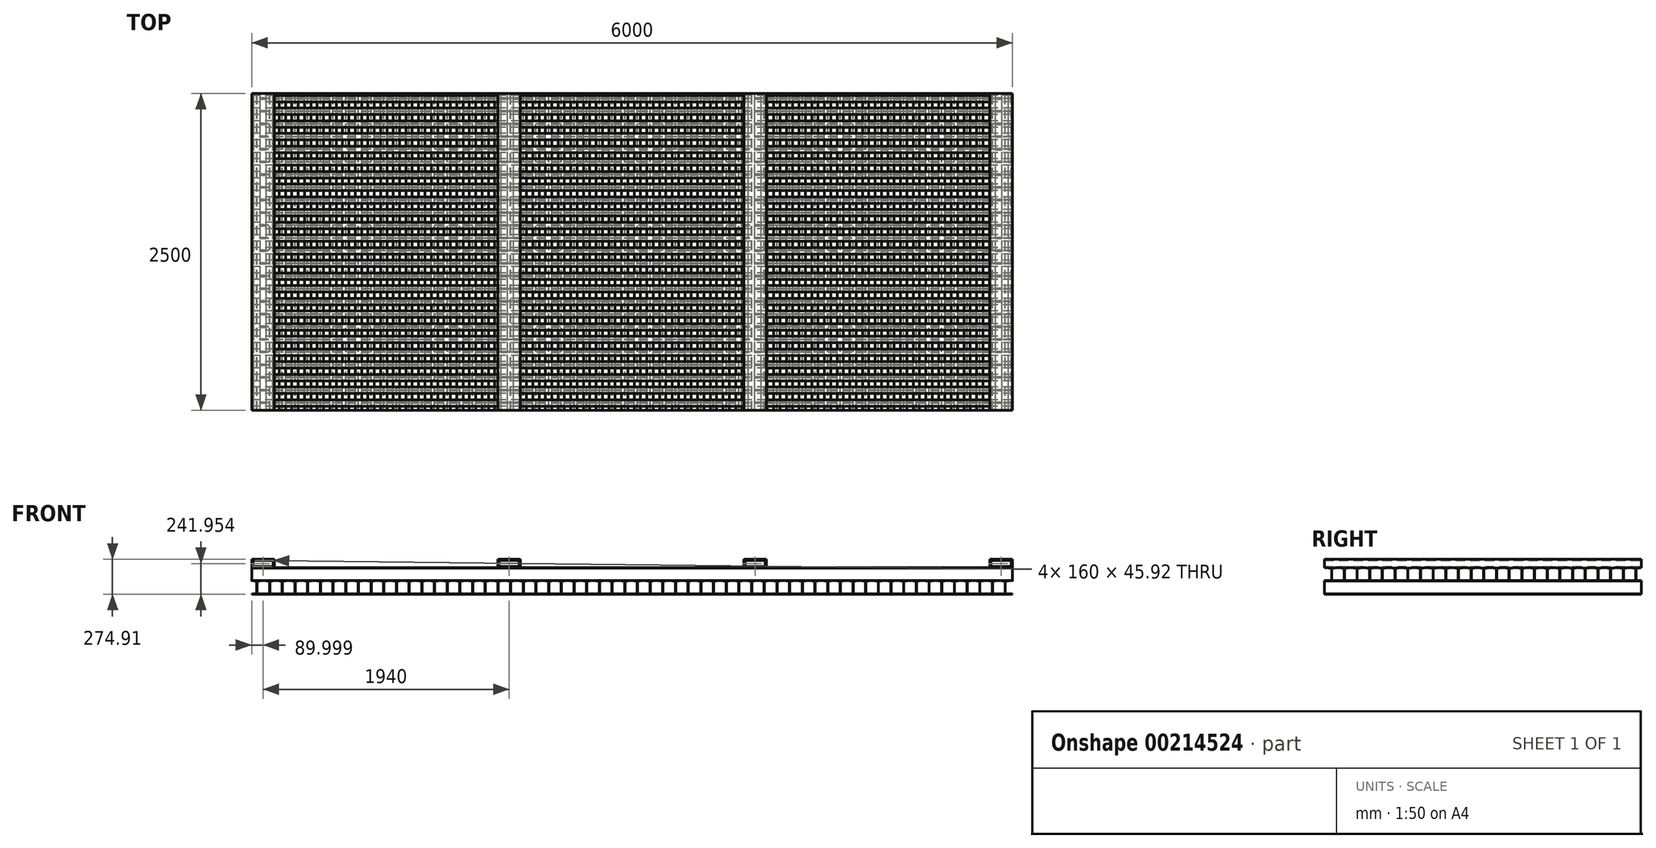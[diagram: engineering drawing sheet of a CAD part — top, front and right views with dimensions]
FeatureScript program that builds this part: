
annotation { "Feature Type Name" : "Feature", "Feature Type Description" : "" }
export const myFeature = defineFeature(function(context is Context, id is Id, definition is map)
    precondition{}
    {
        {
            var Q0;
            Q0=qCreatedBy(makeId("Front.planeOp"),FACE);
            var sketch = newSketch(context, id + "F0", { "sketchPlane" : qUnion([Q0])});
            skLineSegment(sketch, "E0.bottom", {"start": v(-13.61, -0.15) * mm, "end": v(5939.39, -0.15) * mm});
            skLineSegment(sketch, "E0.top", {"start": v(-60.61, -3.15) * mm, "end": v(5939.39, -3.15) * mm});
            skLineSegment(sketch, "E0.left", {"start": v(-60.61, -0.15) * mm, "end": v(-60.61, -3.15) * mm});
            skLineSegment(sketch, "E0.right", {"start": v(5939.39, -0.15) * mm, "end": v(5939.39, -3.15) * mm});
            skLineSegment(sketch, "E1.bottom", {"start": v(-44.11, 99.85) * mm, "end": v(-24.61, 99.85) * mm});
            skLineSegment(sketch, "E1.top", {"start": v(-60.61, -0.15) * mm, "end": v(-24.61, -0.15) * mm});
            skLineSegment(sketch, "E1.left", {"start": v(-20.61, 95.85) * mm, "end": v(-20.61, 3.85) * mm});
            skLineSegment(sketch, "E1.right", {"start": v(-17.61, 95.85) * mm, "end": v(-17.61, 3.85) * mm});
            skLineSegment(sketch, "E2.bottom", {"start": v(-13.61, 99.85) * mm, "end": v(5.89, 99.85) * mm});
            skLineSegment(sketch, "E2.top", {"start": v(-44.11, 102.85) * mm, "end": v(5.89, 102.85) * mm});
            skLineSegment(sketch, "E2.left", {"start": v(-44.11, 99.85) * mm, "end": v(-44.11, 102.85) * mm});
            skLineSegment(sketch, "E2.right", {"start": v(5.89, 99.85) * mm, "end": v(5.89, 102.85) * mm});
            skPoint(sketch, "E3.newPointB", {"position": v(-17.61, 96.07) * mm});
            skArc(sketch, "E3.filletArc", {"start": v(-13.61, 99.85) * mm, "mid": v(-16.44, 98.67) * mm, "end": v(-17.61, 95.85) * mm});
            skPoint(sketch, "E4.visualSharp", {"position": v(-20.61, 99.85) * mm});
            skArc(sketch, "E4.filletArc", {"start": v(-20.61, 95.85) * mm, "mid": v(-21.78, 98.67) * mm, "end": v(-24.61, 99.85) * mm});
            skArc(sketch, "E5.filletArc", {"start": v(-17.61, 3.85) * mm, "mid": v(-16.44, 1.02) * mm, "end": v(-13.61, -0.15) * mm});
            skPoint(sketch, "E6.visualSharp", {"position": v(-20.61, -0.15) * mm});
            skArc(sketch, "E6.filletArc", {"start": v(-24.61, -0.15) * mm, "mid": v(-21.78, 1.02) * mm, "end": v(-20.61, 3.85) * mm});
            skPoint(sketch, "E7.1.0.0", {"position": v(79.39, 99.85) * mm});
            skLineSegment(sketch, "E7.1.0.1", {"start": v(55.89, 99.85) * mm, "end": v(75.39, 99.85) * mm});
            skPoint(sketch, "E7.1.0.2", {"position": v(82.39, 96.07) * mm});
            skLineSegment(sketch, "E7.1.0.3", {"start": v(79.39, 95.85) * mm, "end": v(79.39, 3.85) * mm});
            skLineSegment(sketch, "E7.1.0.4", {"start": v(82.39, 95.85) * mm, "end": v(82.39, 3.85) * mm});
            skLineSegment(sketch, "E7.1.0.5", {"start": v(55.89, 102.85) * mm, "end": v(105.89, 102.85) * mm});
            skLineSegment(sketch, "E7.1.0.6", {"start": v(86.39, 99.85) * mm, "end": v(105.89, 99.85) * mm});
            skLineSegment(sketch, "E7.1.0.7", {"start": v(105.89, 99.85) * mm, "end": v(105.89, 102.85) * mm});
            skLineSegment(sketch, "E7.1.0.8", {"start": v(55.89, 99.85) * mm, "end": v(55.89, 102.85) * mm});
            skArc(sketch, "E7.1.0.9", {"start": v(86.39, 99.85) * mm, "mid": v(83.56, 98.67) * mm, "end": v(82.39, 95.85) * mm});
            skArc(sketch, "E7.1.0.10", {"start": v(79.39, 95.85) * mm, "mid": v(78.22, 98.67) * mm, "end": v(75.39, 99.85) * mm});
            skArc(sketch, "E7.1.0.11", {"start": v(75.39, -0.15) * mm, "mid": v(78.22, 1.02) * mm, "end": v(79.39, 3.85) * mm});
            skArc(sketch, "E7.1.0.12", {"start": v(82.39, 3.85) * mm, "mid": v(83.56, 1.02) * mm, "end": v(86.39, -0.15) * mm});
            skPoint(sketch, "E7.2.0.0", {"position": v(179.39, 99.85) * mm});
            skLineSegment(sketch, "E7.2.0.1", {"start": v(155.89, 99.85) * mm, "end": v(175.39, 99.85) * mm});
            skPoint(sketch, "E7.2.0.2", {"position": v(182.39, 96.07) * mm});
            skLineSegment(sketch, "E7.2.0.3", {"start": v(179.39, 95.85) * mm, "end": v(179.39, 3.85) * mm});
            skLineSegment(sketch, "E7.2.0.4", {"start": v(182.39, 95.85) * mm, "end": v(182.39, 3.85) * mm});
            skLineSegment(sketch, "E7.2.0.5", {"start": v(155.89, 102.85) * mm, "end": v(205.89, 102.85) * mm});
            skLineSegment(sketch, "E7.2.0.6", {"start": v(186.39, 99.85) * mm, "end": v(205.89, 99.85) * mm});
            skLineSegment(sketch, "E7.2.0.7", {"start": v(205.89, 99.85) * mm, "end": v(205.89, 102.85) * mm});
            skLineSegment(sketch, "E7.2.0.8", {"start": v(155.89, 99.85) * mm, "end": v(155.89, 102.85) * mm});
            skArc(sketch, "E7.2.0.9", {"start": v(186.39, 99.85) * mm, "mid": v(183.56, 98.67) * mm, "end": v(182.39, 95.85) * mm});
            skArc(sketch, "E7.2.0.10", {"start": v(179.39, 95.85) * mm, "mid": v(178.22, 98.67) * mm, "end": v(175.39, 99.85) * mm});
            skArc(sketch, "E7.2.0.11", {"start": v(175.39, -0.15) * mm, "mid": v(178.22, 1.02) * mm, "end": v(179.39, 3.85) * mm});
            skArc(sketch, "E7.2.0.12", {"start": v(182.39, 3.85) * mm, "mid": v(183.56, 1.02) * mm, "end": v(186.39, -0.15) * mm});
            skPoint(sketch, "E7.3.0.0", {"position": v(279.39, 99.85) * mm});
            skLineSegment(sketch, "E7.3.0.1", {"start": v(255.89, 99.85) * mm, "end": v(275.39, 99.85) * mm});
            skPoint(sketch, "E7.3.0.2", {"position": v(282.39, 96.07) * mm});
            skLineSegment(sketch, "E7.3.0.3", {"start": v(279.39, 95.85) * mm, "end": v(279.39, 3.85) * mm});
            skLineSegment(sketch, "E7.3.0.4", {"start": v(282.39, 95.85) * mm, "end": v(282.39, 3.85) * mm});
            skLineSegment(sketch, "E7.3.0.5", {"start": v(255.89, 102.85) * mm, "end": v(305.89, 102.85) * mm});
            skLineSegment(sketch, "E7.3.0.6", {"start": v(286.39, 99.85) * mm, "end": v(305.89, 99.85) * mm});
            skLineSegment(sketch, "E7.3.0.7", {"start": v(305.89, 99.85) * mm, "end": v(305.89, 102.85) * mm});
            skLineSegment(sketch, "E7.3.0.8", {"start": v(255.89, 99.85) * mm, "end": v(255.89, 102.85) * mm});
            skArc(sketch, "E7.3.0.9", {"start": v(286.39, 99.85) * mm, "mid": v(283.56, 98.67) * mm, "end": v(282.39, 95.85) * mm});
            skArc(sketch, "E7.3.0.10", {"start": v(279.39, 95.85) * mm, "mid": v(278.22, 98.67) * mm, "end": v(275.39, 99.85) * mm});
            skArc(sketch, "E7.3.0.11", {"start": v(275.39, -0.15) * mm, "mid": v(278.22, 1.02) * mm, "end": v(279.39, 3.85) * mm});
            skArc(sketch, "E7.3.0.12", {"start": v(282.39, 3.85) * mm, "mid": v(283.56, 1.02) * mm, "end": v(286.39, -0.15) * mm});
            skPoint(sketch, "E7.4.0.0", {"position": v(379.39, 99.85) * mm});
            skLineSegment(sketch, "E7.4.0.1", {"start": v(355.89, 99.85) * mm, "end": v(375.39, 99.85) * mm});
            skPoint(sketch, "E7.4.0.2", {"position": v(382.39, 96.07) * mm});
            skLineSegment(sketch, "E7.4.0.3", {"start": v(379.39, 95.85) * mm, "end": v(379.39, 3.85) * mm});
            skLineSegment(sketch, "E7.4.0.4", {"start": v(382.39, 95.85) * mm, "end": v(382.39, 3.85) * mm});
            skLineSegment(sketch, "E7.4.0.5", {"start": v(355.89, 102.85) * mm, "end": v(405.89, 102.85) * mm});
            skLineSegment(sketch, "E7.4.0.6", {"start": v(386.39, 99.85) * mm, "end": v(405.89, 99.85) * mm});
            skLineSegment(sketch, "E7.4.0.7", {"start": v(405.89, 99.85) * mm, "end": v(405.89, 102.85) * mm});
            skLineSegment(sketch, "E7.4.0.8", {"start": v(355.89, 99.85) * mm, "end": v(355.89, 102.85) * mm});
            skArc(sketch, "E7.4.0.9", {"start": v(386.39, 99.85) * mm, "mid": v(383.56, 98.67) * mm, "end": v(382.39, 95.85) * mm});
            skArc(sketch, "E7.4.0.10", {"start": v(379.39, 95.85) * mm, "mid": v(378.22, 98.67) * mm, "end": v(375.39, 99.85) * mm});
            skArc(sketch, "E7.4.0.11", {"start": v(375.39, -0.15) * mm, "mid": v(378.22, 1.02) * mm, "end": v(379.39, 3.85) * mm});
            skArc(sketch, "E7.4.0.12", {"start": v(382.39, 3.85) * mm, "mid": v(383.56, 1.02) * mm, "end": v(386.39, -0.15) * mm});
            skPoint(sketch, "E7.5.0.0", {"position": v(479.39, 99.85) * mm});
            skLineSegment(sketch, "E7.5.0.1", {"start": v(455.89, 99.85) * mm, "end": v(475.39, 99.85) * mm});
            skPoint(sketch, "E7.5.0.2", {"position": v(482.39, 96.07) * mm});
            skLineSegment(sketch, "E7.5.0.3", {"start": v(479.39, 95.85) * mm, "end": v(479.39, 3.85) * mm});
            skLineSegment(sketch, "E7.5.0.4", {"start": v(482.39, 95.85) * mm, "end": v(482.39, 3.85) * mm});
            skLineSegment(sketch, "E7.5.0.5", {"start": v(455.89, 102.85) * mm, "end": v(505.89, 102.85) * mm});
            skLineSegment(sketch, "E7.5.0.6", {"start": v(486.39, 99.85) * mm, "end": v(505.89, 99.85) * mm});
            skLineSegment(sketch, "E7.5.0.7", {"start": v(505.89, 99.85) * mm, "end": v(505.89, 102.85) * mm});
            skLineSegment(sketch, "E7.5.0.8", {"start": v(455.89, 99.85) * mm, "end": v(455.89, 102.85) * mm});
            skArc(sketch, "E7.5.0.9", {"start": v(486.39, 99.85) * mm, "mid": v(483.56, 98.67) * mm, "end": v(482.39, 95.85) * mm});
            skArc(sketch, "E7.5.0.10", {"start": v(479.39, 95.85) * mm, "mid": v(478.22, 98.67) * mm, "end": v(475.39, 99.85) * mm});
            skArc(sketch, "E7.5.0.11", {"start": v(475.39, -0.15) * mm, "mid": v(478.22, 1.02) * mm, "end": v(479.39, 3.85) * mm});
            skArc(sketch, "E7.5.0.12", {"start": v(482.39, 3.85) * mm, "mid": v(483.56, 1.02) * mm, "end": v(486.39, -0.15) * mm});
            skPoint(sketch, "E7.6.0.0", {"position": v(579.39, 99.85) * mm});
            skLineSegment(sketch, "E7.6.0.1", {"start": v(555.89, 99.85) * mm, "end": v(575.39, 99.85) * mm});
            skPoint(sketch, "E7.6.0.2", {"position": v(582.39, 96.07) * mm});
            skLineSegment(sketch, "E7.6.0.3", {"start": v(579.39, 95.85) * mm, "end": v(579.39, 3.85) * mm});
            skLineSegment(sketch, "E7.6.0.4", {"start": v(582.39, 95.85) * mm, "end": v(582.39, 3.85) * mm});
            skLineSegment(sketch, "E7.6.0.5", {"start": v(555.89, 102.85) * mm, "end": v(605.89, 102.85) * mm});
            skLineSegment(sketch, "E7.6.0.6", {"start": v(586.39, 99.85) * mm, "end": v(605.89, 99.85) * mm});
            skLineSegment(sketch, "E7.6.0.7", {"start": v(605.89, 99.85) * mm, "end": v(605.89, 102.85) * mm});
            skLineSegment(sketch, "E7.6.0.8", {"start": v(555.89, 99.85) * mm, "end": v(555.89, 102.85) * mm});
            skArc(sketch, "E7.6.0.9", {"start": v(586.39, 99.85) * mm, "mid": v(583.56, 98.67) * mm, "end": v(582.39, 95.85) * mm});
            skArc(sketch, "E7.6.0.10", {"start": v(579.39, 95.85) * mm, "mid": v(578.22, 98.67) * mm, "end": v(575.39, 99.85) * mm});
            skArc(sketch, "E7.6.0.11", {"start": v(575.39, -0.15) * mm, "mid": v(578.22, 1.02) * mm, "end": v(579.39, 3.85) * mm});
            skArc(sketch, "E7.6.0.12", {"start": v(582.39, 3.85) * mm, "mid": v(583.56, 1.02) * mm, "end": v(586.39, -0.15) * mm});
            skPoint(sketch, "E7.7.0.0", {"position": v(679.39, 99.85) * mm});
            skLineSegment(sketch, "E7.7.0.1", {"start": v(655.89, 99.85) * mm, "end": v(675.39, 99.85) * mm});
            skPoint(sketch, "E7.7.0.2", {"position": v(682.39, 96.07) * mm});
            skLineSegment(sketch, "E7.7.0.3", {"start": v(679.39, 95.85) * mm, "end": v(679.39, 3.85) * mm});
            skLineSegment(sketch, "E7.7.0.4", {"start": v(682.39, 95.85) * mm, "end": v(682.39, 3.85) * mm});
            skLineSegment(sketch, "E7.7.0.5", {"start": v(655.89, 102.85) * mm, "end": v(705.89, 102.85) * mm});
            skLineSegment(sketch, "E7.7.0.6", {"start": v(686.39, 99.85) * mm, "end": v(705.89, 99.85) * mm});
            skLineSegment(sketch, "E7.7.0.7", {"start": v(705.89, 99.85) * mm, "end": v(705.89, 102.85) * mm});
            skLineSegment(sketch, "E7.7.0.8", {"start": v(655.89, 99.85) * mm, "end": v(655.89, 102.85) * mm});
            skArc(sketch, "E7.7.0.9", {"start": v(686.39, 99.85) * mm, "mid": v(683.56, 98.67) * mm, "end": v(682.39, 95.85) * mm});
            skArc(sketch, "E7.7.0.10", {"start": v(679.39, 95.85) * mm, "mid": v(678.22, 98.67) * mm, "end": v(675.39, 99.85) * mm});
            skArc(sketch, "E7.7.0.11", {"start": v(675.39, -0.15) * mm, "mid": v(678.22, 1.02) * mm, "end": v(679.39, 3.85) * mm});
            skArc(sketch, "E7.7.0.12", {"start": v(682.39, 3.85) * mm, "mid": v(683.56, 1.02) * mm, "end": v(686.39, -0.15) * mm});
            skPoint(sketch, "E7.8.0.0", {"position": v(779.39, 99.85) * mm});
            skLineSegment(sketch, "E7.8.0.1", {"start": v(755.89, 99.85) * mm, "end": v(775.39, 99.85) * mm});
            skPoint(sketch, "E7.8.0.2", {"position": v(782.39, 96.07) * mm});
            skLineSegment(sketch, "E7.8.0.3", {"start": v(779.39, 95.85) * mm, "end": v(779.39, 3.85) * mm});
            skLineSegment(sketch, "E7.8.0.4", {"start": v(782.39, 95.85) * mm, "end": v(782.39, 3.85) * mm});
            skLineSegment(sketch, "E7.8.0.5", {"start": v(755.89, 102.85) * mm, "end": v(805.89, 102.85) * mm});
            skLineSegment(sketch, "E7.8.0.6", {"start": v(786.39, 99.85) * mm, "end": v(805.89, 99.85) * mm});
            skLineSegment(sketch, "E7.8.0.7", {"start": v(805.89, 99.85) * mm, "end": v(805.89, 102.85) * mm});
            skLineSegment(sketch, "E7.8.0.8", {"start": v(755.89, 99.85) * mm, "end": v(755.89, 102.85) * mm});
            skArc(sketch, "E7.8.0.9", {"start": v(786.39, 99.85) * mm, "mid": v(783.56, 98.67) * mm, "end": v(782.39, 95.85) * mm});
            skArc(sketch, "E7.8.0.10", {"start": v(779.39, 95.85) * mm, "mid": v(778.22, 98.67) * mm, "end": v(775.39, 99.85) * mm});
            skArc(sketch, "E7.8.0.11", {"start": v(775.39, -0.15) * mm, "mid": v(778.22, 1.02) * mm, "end": v(779.39, 3.85) * mm});
            skArc(sketch, "E7.8.0.12", {"start": v(782.39, 3.85) * mm, "mid": v(783.56, 1.02) * mm, "end": v(786.39, -0.15) * mm});
            skPoint(sketch, "E7.9.0.0", {"position": v(879.39, 99.85) * mm});
            skLineSegment(sketch, "E7.9.0.1", {"start": v(855.89, 99.85) * mm, "end": v(875.39, 99.85) * mm});
            skPoint(sketch, "E7.9.0.2", {"position": v(882.39, 96.07) * mm});
            skLineSegment(sketch, "E7.9.0.3", {"start": v(879.39, 95.85) * mm, "end": v(879.39, 3.85) * mm});
            skLineSegment(sketch, "E7.9.0.4", {"start": v(882.39, 95.85) * mm, "end": v(882.39, 3.85) * mm});
            skLineSegment(sketch, "E7.9.0.5", {"start": v(855.89, 102.85) * mm, "end": v(905.89, 102.85) * mm});
            skLineSegment(sketch, "E7.9.0.6", {"start": v(886.39, 99.85) * mm, "end": v(905.89, 99.85) * mm});
            skLineSegment(sketch, "E7.9.0.7", {"start": v(905.89, 99.85) * mm, "end": v(905.89, 102.85) * mm});
            skLineSegment(sketch, "E7.9.0.8", {"start": v(855.89, 99.85) * mm, "end": v(855.89, 102.85) * mm});
            skArc(sketch, "E7.9.0.9", {"start": v(886.39, 99.85) * mm, "mid": v(883.56, 98.67) * mm, "end": v(882.39, 95.85) * mm});
            skArc(sketch, "E7.9.0.10", {"start": v(879.39, 95.85) * mm, "mid": v(878.22, 98.67) * mm, "end": v(875.39, 99.85) * mm});
            skArc(sketch, "E7.9.0.11", {"start": v(875.39, -0.15) * mm, "mid": v(878.22, 1.02) * mm, "end": v(879.39, 3.85) * mm});
            skArc(sketch, "E7.9.0.12", {"start": v(882.39, 3.85) * mm, "mid": v(883.56, 1.02) * mm, "end": v(886.39, -0.15) * mm});
            skPoint(sketch, "E7.10.0.0", {"position": v(979.39, 99.85) * mm});
            skLineSegment(sketch, "E7.10.0.1", {"start": v(955.89, 99.85) * mm, "end": v(975.39, 99.85) * mm});
            skPoint(sketch, "E7.10.0.2", {"position": v(982.39, 96.07) * mm});
            skLineSegment(sketch, "E7.10.0.3", {"start": v(979.39, 95.85) * mm, "end": v(979.39, 3.85) * mm});
            skLineSegment(sketch, "E7.10.0.4", {"start": v(982.39, 95.85) * mm, "end": v(982.39, 3.85) * mm});
            skLineSegment(sketch, "E7.10.0.5", {"start": v(955.89, 102.85) * mm, "end": v(1005.89, 102.85) * mm});
            skLineSegment(sketch, "E7.10.0.6", {"start": v(986.39, 99.85) * mm, "end": v(1005.89, 99.85) * mm});
            skLineSegment(sketch, "E7.10.0.7", {"start": v(1005.89, 99.85) * mm, "end": v(1005.89, 102.85) * mm});
            skLineSegment(sketch, "E7.10.0.8", {"start": v(955.89, 99.85) * mm, "end": v(955.89, 102.85) * mm});
            skArc(sketch, "E7.10.0.9", {"start": v(986.39, 99.85) * mm, "mid": v(983.56, 98.67) * mm, "end": v(982.39, 95.85) * mm});
            skArc(sketch, "E7.10.0.10", {"start": v(979.39, 95.85) * mm, "mid": v(978.22, 98.67) * mm, "end": v(975.39, 99.85) * mm});
            skArc(sketch, "E7.10.0.11", {"start": v(975.39, -0.15) * mm, "mid": v(978.22, 1.02) * mm, "end": v(979.39, 3.85) * mm});
            skArc(sketch, "E7.10.0.12", {"start": v(982.39, 3.85) * mm, "mid": v(983.56, 1.02) * mm, "end": v(986.39, -0.15) * mm});
            skPoint(sketch, "E7.11.0.0", {"position": v(1079.39, 99.85) * mm});
            skLineSegment(sketch, "E7.11.0.1", {"start": v(1055.89, 99.85) * mm, "end": v(1075.39, 99.85) * mm});
            skPoint(sketch, "E7.11.0.2", {"position": v(1082.39, 96.07) * mm});
            skLineSegment(sketch, "E7.11.0.3", {"start": v(1079.39, 95.85) * mm, "end": v(1079.39, 3.85) * mm});
            skLineSegment(sketch, "E7.11.0.4", {"start": v(1082.39, 95.85) * mm, "end": v(1082.39, 3.85) * mm});
            skLineSegment(sketch, "E7.11.0.5", {"start": v(1055.89, 102.85) * mm, "end": v(1105.89, 102.85) * mm});
            skLineSegment(sketch, "E7.11.0.6", {"start": v(1086.39, 99.85) * mm, "end": v(1105.89, 99.85) * mm});
            skLineSegment(sketch, "E7.11.0.7", {"start": v(1105.89, 99.85) * mm, "end": v(1105.89, 102.85) * mm});
            skLineSegment(sketch, "E7.11.0.8", {"start": v(1055.89, 99.85) * mm, "end": v(1055.89, 102.85) * mm});
            skArc(sketch, "E7.11.0.9", {"start": v(1086.39, 99.85) * mm, "mid": v(1083.56, 98.67) * mm, "end": v(1082.39, 95.85) * mm});
            skArc(sketch, "E7.11.0.10", {"start": v(1079.39, 95.85) * mm, "mid": v(1078.22, 98.67) * mm, "end": v(1075.39, 99.85) * mm});
            skArc(sketch, "E7.11.0.11", {"start": v(1075.39, -0.15) * mm, "mid": v(1078.22, 1.02) * mm, "end": v(1079.39, 3.85) * mm});
            skArc(sketch, "E7.11.0.12", {"start": v(1082.39, 3.85) * mm, "mid": v(1083.56, 1.02) * mm, "end": v(1086.39, -0.15) * mm});
            skPoint(sketch, "E7.12.0.0", {"position": v(1179.39, 99.85) * mm});
            skLineSegment(sketch, "E7.12.0.1", {"start": v(1155.89, 99.85) * mm, "end": v(1175.39, 99.85) * mm});
            skPoint(sketch, "E7.12.0.2", {"position": v(1182.39, 96.07) * mm});
            skLineSegment(sketch, "E7.12.0.3", {"start": v(1179.39, 95.85) * mm, "end": v(1179.39, 3.85) * mm});
            skLineSegment(sketch, "E7.12.0.4", {"start": v(1182.39, 95.85) * mm, "end": v(1182.39, 3.85) * mm});
            skLineSegment(sketch, "E7.12.0.5", {"start": v(1155.89, 102.85) * mm, "end": v(1205.89, 102.85) * mm});
            skLineSegment(sketch, "E7.12.0.6", {"start": v(1186.39, 99.85) * mm, "end": v(1205.89, 99.85) * mm});
            skLineSegment(sketch, "E7.12.0.7", {"start": v(1205.89, 99.85) * mm, "end": v(1205.89, 102.85) * mm});
            skLineSegment(sketch, "E7.12.0.8", {"start": v(1155.89, 99.85) * mm, "end": v(1155.89, 102.85) * mm});
            skArc(sketch, "E7.12.0.9", {"start": v(1186.39, 99.85) * mm, "mid": v(1183.56, 98.67) * mm, "end": v(1182.39, 95.85) * mm});
            skArc(sketch, "E7.12.0.10", {"start": v(1179.39, 95.85) * mm, "mid": v(1178.22, 98.67) * mm, "end": v(1175.39, 99.85) * mm});
            skArc(sketch, "E7.12.0.11", {"start": v(1175.39, -0.15) * mm, "mid": v(1178.22, 1.02) * mm, "end": v(1179.39, 3.85) * mm});
            skArc(sketch, "E7.12.0.12", {"start": v(1182.39, 3.85) * mm, "mid": v(1183.56, 1.02) * mm, "end": v(1186.39, -0.15) * mm});
            skPoint(sketch, "E7.13.0.0", {"position": v(1279.39, 99.85) * mm});
            skLineSegment(sketch, "E7.13.0.1", {"start": v(1255.89, 99.85) * mm, "end": v(1275.39, 99.85) * mm});
            skPoint(sketch, "E7.13.0.2", {"position": v(1282.39, 96.07) * mm});
            skLineSegment(sketch, "E7.13.0.3", {"start": v(1279.39, 95.85) * mm, "end": v(1279.39, 3.85) * mm});
            skLineSegment(sketch, "E7.13.0.4", {"start": v(1282.39, 95.85) * mm, "end": v(1282.39, 3.85) * mm});
            skLineSegment(sketch, "E7.13.0.5", {"start": v(1255.89, 102.85) * mm, "end": v(1305.89, 102.85) * mm});
            skLineSegment(sketch, "E7.13.0.6", {"start": v(1286.39, 99.85) * mm, "end": v(1305.89, 99.85) * mm});
            skLineSegment(sketch, "E7.13.0.7", {"start": v(1305.89, 99.85) * mm, "end": v(1305.89, 102.85) * mm});
            skLineSegment(sketch, "E7.13.0.8", {"start": v(1255.89, 99.85) * mm, "end": v(1255.89, 102.85) * mm});
            skArc(sketch, "E7.13.0.9", {"start": v(1286.39, 99.85) * mm, "mid": v(1283.56, 98.67) * mm, "end": v(1282.39, 95.85) * mm});
            skArc(sketch, "E7.13.0.10", {"start": v(1279.39, 95.85) * mm, "mid": v(1278.22, 98.67) * mm, "end": v(1275.39, 99.85) * mm});
            skArc(sketch, "E7.13.0.11", {"start": v(1275.39, -0.15) * mm, "mid": v(1278.22, 1.02) * mm, "end": v(1279.39, 3.85) * mm});
            skArc(sketch, "E7.13.0.12", {"start": v(1282.39, 3.85) * mm, "mid": v(1283.56, 1.02) * mm, "end": v(1286.39, -0.15) * mm});
            skPoint(sketch, "E7.14.0.0", {"position": v(1379.39, 99.85) * mm});
            skLineSegment(sketch, "E7.14.0.1", {"start": v(1355.89, 99.85) * mm, "end": v(1375.39, 99.85) * mm});
            skPoint(sketch, "E7.14.0.2", {"position": v(1382.39, 96.07) * mm});
            skLineSegment(sketch, "E7.14.0.3", {"start": v(1379.39, 95.85) * mm, "end": v(1379.39, 3.85) * mm});
            skLineSegment(sketch, "E7.14.0.4", {"start": v(1382.39, 95.85) * mm, "end": v(1382.39, 3.85) * mm});
            skLineSegment(sketch, "E7.14.0.5", {"start": v(1355.89, 102.85) * mm, "end": v(1405.89, 102.85) * mm});
            skLineSegment(sketch, "E7.14.0.6", {"start": v(1386.39, 99.85) * mm, "end": v(1405.89, 99.85) * mm});
            skLineSegment(sketch, "E7.14.0.7", {"start": v(1405.89, 99.85) * mm, "end": v(1405.89, 102.85) * mm});
            skLineSegment(sketch, "E7.14.0.8", {"start": v(1355.89, 99.85) * mm, "end": v(1355.89, 102.85) * mm});
            skArc(sketch, "E7.14.0.9", {"start": v(1386.39, 99.85) * mm, "mid": v(1383.56, 98.67) * mm, "end": v(1382.39, 95.85) * mm});
            skArc(sketch, "E7.14.0.10", {"start": v(1379.39, 95.85) * mm, "mid": v(1378.22, 98.67) * mm, "end": v(1375.39, 99.85) * mm});
            skArc(sketch, "E7.14.0.11", {"start": v(1375.39, -0.15) * mm, "mid": v(1378.22, 1.02) * mm, "end": v(1379.39, 3.85) * mm});
            skArc(sketch, "E7.14.0.12", {"start": v(1382.39, 3.85) * mm, "mid": v(1383.56, 1.02) * mm, "end": v(1386.39, -0.15) * mm});
            skPoint(sketch, "E7.15.0.0", {"position": v(1479.39, 99.85) * mm});
            skLineSegment(sketch, "E7.15.0.1", {"start": v(1455.89, 99.85) * mm, "end": v(1475.39, 99.85) * mm});
            skPoint(sketch, "E7.15.0.2", {"position": v(1482.39, 96.07) * mm});
            skLineSegment(sketch, "E7.15.0.3", {"start": v(1479.39, 95.85) * mm, "end": v(1479.39, 3.85) * mm});
            skLineSegment(sketch, "E7.15.0.4", {"start": v(1482.39, 95.85) * mm, "end": v(1482.39, 3.85) * mm});
            skLineSegment(sketch, "E7.15.0.5", {"start": v(1455.89, 102.85) * mm, "end": v(1505.89, 102.85) * mm});
            skLineSegment(sketch, "E7.15.0.6", {"start": v(1486.39, 99.85) * mm, "end": v(1505.89, 99.85) * mm});
            skLineSegment(sketch, "E7.15.0.7", {"start": v(1505.89, 99.85) * mm, "end": v(1505.89, 102.85) * mm});
            skLineSegment(sketch, "E7.15.0.8", {"start": v(1455.89, 99.85) * mm, "end": v(1455.89, 102.85) * mm});
            skArc(sketch, "E7.15.0.9", {"start": v(1486.39, 99.85) * mm, "mid": v(1483.56, 98.67) * mm, "end": v(1482.39, 95.85) * mm});
            skArc(sketch, "E7.15.0.10", {"start": v(1479.39, 95.85) * mm, "mid": v(1478.22, 98.67) * mm, "end": v(1475.39, 99.85) * mm});
            skArc(sketch, "E7.15.0.11", {"start": v(1475.39, -0.15) * mm, "mid": v(1478.22, 1.02) * mm, "end": v(1479.39, 3.85) * mm});
            skArc(sketch, "E7.15.0.12", {"start": v(1482.39, 3.85) * mm, "mid": v(1483.56, 1.02) * mm, "end": v(1486.39, -0.15) * mm});
            skPoint(sketch, "E7.16.0.0", {"position": v(1579.39, 99.85) * mm});
            skLineSegment(sketch, "E7.16.0.1", {"start": v(1555.89, 99.85) * mm, "end": v(1575.39, 99.85) * mm});
            skPoint(sketch, "E7.16.0.2", {"position": v(1582.39, 96.07) * mm});
            skLineSegment(sketch, "E7.16.0.3", {"start": v(1579.39, 95.85) * mm, "end": v(1579.39, 3.85) * mm});
            skLineSegment(sketch, "E7.16.0.4", {"start": v(1582.39, 95.85) * mm, "end": v(1582.39, 3.85) * mm});
            skLineSegment(sketch, "E7.16.0.5", {"start": v(1555.89, 102.85) * mm, "end": v(1605.89, 102.85) * mm});
            skLineSegment(sketch, "E7.16.0.6", {"start": v(1586.39, 99.85) * mm, "end": v(1605.89, 99.85) * mm});
            skLineSegment(sketch, "E7.16.0.7", {"start": v(1605.89, 99.85) * mm, "end": v(1605.89, 102.85) * mm});
            skLineSegment(sketch, "E7.16.0.8", {"start": v(1555.89, 99.85) * mm, "end": v(1555.89, 102.85) * mm});
            skArc(sketch, "E7.16.0.9", {"start": v(1586.39, 99.85) * mm, "mid": v(1583.56, 98.67) * mm, "end": v(1582.39, 95.85) * mm});
            skArc(sketch, "E7.16.0.10", {"start": v(1579.39, 95.85) * mm, "mid": v(1578.22, 98.67) * mm, "end": v(1575.39, 99.85) * mm});
            skArc(sketch, "E7.16.0.11", {"start": v(1575.39, -0.15) * mm, "mid": v(1578.22, 1.02) * mm, "end": v(1579.39, 3.85) * mm});
            skArc(sketch, "E7.16.0.12", {"start": v(1582.39, 3.85) * mm, "mid": v(1583.56, 1.02) * mm, "end": v(1586.39, -0.15) * mm});
            skPoint(sketch, "E7.17.0.0", {"position": v(1679.39, 99.85) * mm});
            skLineSegment(sketch, "E7.17.0.1", {"start": v(1655.89, 99.85) * mm, "end": v(1675.39, 99.85) * mm});
            skPoint(sketch, "E7.17.0.2", {"position": v(1682.39, 96.07) * mm});
            skLineSegment(sketch, "E7.17.0.3", {"start": v(1679.39, 95.85) * mm, "end": v(1679.39, 3.85) * mm});
            skLineSegment(sketch, "E7.17.0.4", {"start": v(1682.39, 95.85) * mm, "end": v(1682.39, 3.85) * mm});
            skLineSegment(sketch, "E7.17.0.5", {"start": v(1655.89, 102.85) * mm, "end": v(1705.89, 102.85) * mm});
            skLineSegment(sketch, "E7.17.0.6", {"start": v(1686.39, 99.85) * mm, "end": v(1705.89, 99.85) * mm});
            skLineSegment(sketch, "E7.17.0.7", {"start": v(1705.89, 99.85) * mm, "end": v(1705.89, 102.85) * mm});
            skLineSegment(sketch, "E7.17.0.8", {"start": v(1655.89, 99.85) * mm, "end": v(1655.89, 102.85) * mm});
            skArc(sketch, "E7.17.0.9", {"start": v(1686.39, 99.85) * mm, "mid": v(1683.56, 98.67) * mm, "end": v(1682.39, 95.85) * mm});
            skArc(sketch, "E7.17.0.10", {"start": v(1679.39, 95.85) * mm, "mid": v(1678.22, 98.67) * mm, "end": v(1675.39, 99.85) * mm});
            skArc(sketch, "E7.17.0.11", {"start": v(1675.39, -0.15) * mm, "mid": v(1678.22, 1.02) * mm, "end": v(1679.39, 3.85) * mm});
            skArc(sketch, "E7.17.0.12", {"start": v(1682.39, 3.85) * mm, "mid": v(1683.56, 1.02) * mm, "end": v(1686.39, -0.15) * mm});
            skPoint(sketch, "E7.18.0.0", {"position": v(1779.39, 99.85) * mm});
            skLineSegment(sketch, "E7.18.0.1", {"start": v(1755.89, 99.85) * mm, "end": v(1775.39, 99.85) * mm});
            skPoint(sketch, "E7.18.0.2", {"position": v(1782.39, 96.07) * mm});
            skLineSegment(sketch, "E7.18.0.3", {"start": v(1779.39, 95.85) * mm, "end": v(1779.39, 3.85) * mm});
            skLineSegment(sketch, "E7.18.0.4", {"start": v(1782.39, 95.85) * mm, "end": v(1782.39, 3.85) * mm});
            skLineSegment(sketch, "E7.18.0.5", {"start": v(1755.89, 102.85) * mm, "end": v(1805.89, 102.85) * mm});
            skLineSegment(sketch, "E7.18.0.6", {"start": v(1786.39, 99.85) * mm, "end": v(1805.89, 99.85) * mm});
            skLineSegment(sketch, "E7.18.0.7", {"start": v(1805.89, 99.85) * mm, "end": v(1805.89, 102.85) * mm});
            skLineSegment(sketch, "E7.18.0.8", {"start": v(1755.89, 99.85) * mm, "end": v(1755.89, 102.85) * mm});
            skArc(sketch, "E7.18.0.9", {"start": v(1786.39, 99.85) * mm, "mid": v(1783.56, 98.67) * mm, "end": v(1782.39, 95.85) * mm});
            skArc(sketch, "E7.18.0.10", {"start": v(1779.39, 95.85) * mm, "mid": v(1778.22, 98.67) * mm, "end": v(1775.39, 99.85) * mm});
            skArc(sketch, "E7.18.0.11", {"start": v(1775.39, -0.15) * mm, "mid": v(1778.22, 1.02) * mm, "end": v(1779.39, 3.85) * mm});
            skArc(sketch, "E7.18.0.12", {"start": v(1782.39, 3.85) * mm, "mid": v(1783.56, 1.02) * mm, "end": v(1786.39, -0.15) * mm});
            skPoint(sketch, "E7.19.0.0", {"position": v(1879.39, 99.85) * mm});
            skLineSegment(sketch, "E7.19.0.1", {"start": v(1855.89, 99.85) * mm, "end": v(1875.39, 99.85) * mm});
            skPoint(sketch, "E7.19.0.2", {"position": v(1882.39, 96.07) * mm});
            skLineSegment(sketch, "E7.19.0.3", {"start": v(1879.39, 95.85) * mm, "end": v(1879.39, 3.85) * mm});
            skLineSegment(sketch, "E7.19.0.4", {"start": v(1882.39, 95.85) * mm, "end": v(1882.39, 3.85) * mm});
            skLineSegment(sketch, "E7.19.0.5", {"start": v(1855.89, 102.85) * mm, "end": v(1905.89, 102.85) * mm});
            skLineSegment(sketch, "E7.19.0.6", {"start": v(1886.39, 99.85) * mm, "end": v(1905.89, 99.85) * mm});
            skLineSegment(sketch, "E7.19.0.7", {"start": v(1905.89, 99.85) * mm, "end": v(1905.89, 102.85) * mm});
            skLineSegment(sketch, "E7.19.0.8", {"start": v(1855.89, 99.85) * mm, "end": v(1855.89, 102.85) * mm});
            skArc(sketch, "E7.19.0.9", {"start": v(1886.39, 99.85) * mm, "mid": v(1883.56, 98.67) * mm, "end": v(1882.39, 95.85) * mm});
            skArc(sketch, "E7.19.0.10", {"start": v(1879.39, 95.85) * mm, "mid": v(1878.22, 98.67) * mm, "end": v(1875.39, 99.85) * mm});
            skArc(sketch, "E7.19.0.11", {"start": v(1875.39, -0.15) * mm, "mid": v(1878.22, 1.02) * mm, "end": v(1879.39, 3.85) * mm});
            skArc(sketch, "E7.19.0.12", {"start": v(1882.39, 3.85) * mm, "mid": v(1883.56, 1.02) * mm, "end": v(1886.39, -0.15) * mm});
            skPoint(sketch, "E7.20.0.0", {"position": v(1979.39, 99.85) * mm});
            skLineSegment(sketch, "E7.20.0.1", {"start": v(1955.89, 99.85) * mm, "end": v(1975.39, 99.85) * mm});
            skPoint(sketch, "E7.20.0.2", {"position": v(1982.39, 96.07) * mm});
            skLineSegment(sketch, "E7.20.0.3", {"start": v(1979.39, 95.85) * mm, "end": v(1979.39, 3.85) * mm});
            skLineSegment(sketch, "E7.20.0.4", {"start": v(1982.39, 95.85) * mm, "end": v(1982.39, 3.85) * mm});
            skLineSegment(sketch, "E7.20.0.5", {"start": v(1955.89, 102.85) * mm, "end": v(2005.89, 102.85) * mm});
            skLineSegment(sketch, "E7.20.0.6", {"start": v(1986.39, 99.85) * mm, "end": v(2005.89, 99.85) * mm});
            skLineSegment(sketch, "E7.20.0.7", {"start": v(2005.89, 99.85) * mm, "end": v(2005.89, 102.85) * mm});
            skLineSegment(sketch, "E7.20.0.8", {"start": v(1955.89, 99.85) * mm, "end": v(1955.89, 102.85) * mm});
            skArc(sketch, "E7.20.0.9", {"start": v(1986.39, 99.85) * mm, "mid": v(1983.56, 98.67) * mm, "end": v(1982.39, 95.85) * mm});
            skArc(sketch, "E7.20.0.10", {"start": v(1979.39, 95.85) * mm, "mid": v(1978.22, 98.67) * mm, "end": v(1975.39, 99.85) * mm});
            skArc(sketch, "E7.20.0.11", {"start": v(1975.39, -0.15) * mm, "mid": v(1978.22, 1.02) * mm, "end": v(1979.39, 3.85) * mm});
            skArc(sketch, "E7.20.0.12", {"start": v(1982.39, 3.85) * mm, "mid": v(1983.56, 1.02) * mm, "end": v(1986.39, -0.15) * mm});
            skPoint(sketch, "E7.21.0.0", {"position": v(2079.39, 99.85) * mm});
            skLineSegment(sketch, "E7.21.0.1", {"start": v(2055.89, 99.85) * mm, "end": v(2075.39, 99.85) * mm});
            skPoint(sketch, "E7.21.0.2", {"position": v(2082.39, 96.07) * mm});
            skLineSegment(sketch, "E7.21.0.3", {"start": v(2079.39, 95.85) * mm, "end": v(2079.39, 3.85) * mm});
            skLineSegment(sketch, "E7.21.0.4", {"start": v(2082.39, 95.85) * mm, "end": v(2082.39, 3.85) * mm});
            skLineSegment(sketch, "E7.21.0.5", {"start": v(2055.89, 102.85) * mm, "end": v(2105.89, 102.85) * mm});
            skLineSegment(sketch, "E7.21.0.6", {"start": v(2086.39, 99.85) * mm, "end": v(2105.89, 99.85) * mm});
            skLineSegment(sketch, "E7.21.0.7", {"start": v(2105.89, 99.85) * mm, "end": v(2105.89, 102.85) * mm});
            skLineSegment(sketch, "E7.21.0.8", {"start": v(2055.89, 99.85) * mm, "end": v(2055.89, 102.85) * mm});
            skArc(sketch, "E7.21.0.9", {"start": v(2086.39, 99.85) * mm, "mid": v(2083.56, 98.67) * mm, "end": v(2082.39, 95.85) * mm});
            skArc(sketch, "E7.21.0.10", {"start": v(2079.39, 95.85) * mm, "mid": v(2078.22, 98.67) * mm, "end": v(2075.39, 99.85) * mm});
            skArc(sketch, "E7.21.0.11", {"start": v(2075.39, -0.15) * mm, "mid": v(2078.22, 1.02) * mm, "end": v(2079.39, 3.85) * mm});
            skArc(sketch, "E7.21.0.12", {"start": v(2082.39, 3.85) * mm, "mid": v(2083.56, 1.02) * mm, "end": v(2086.39, -0.15) * mm});
            skPoint(sketch, "E7.22.0.0", {"position": v(2179.39, 99.85) * mm});
            skLineSegment(sketch, "E7.22.0.1", {"start": v(2155.89, 99.85) * mm, "end": v(2175.39, 99.85) * mm});
            skPoint(sketch, "E7.22.0.2", {"position": v(2182.39, 96.07) * mm});
            skLineSegment(sketch, "E7.22.0.3", {"start": v(2179.39, 95.85) * mm, "end": v(2179.39, 3.85) * mm});
            skLineSegment(sketch, "E7.22.0.4", {"start": v(2182.39, 95.85) * mm, "end": v(2182.39, 3.85) * mm});
            skLineSegment(sketch, "E7.22.0.5", {"start": v(2155.89, 102.85) * mm, "end": v(2205.89, 102.85) * mm});
            skLineSegment(sketch, "E7.22.0.6", {"start": v(2186.39, 99.85) * mm, "end": v(2205.89, 99.85) * mm});
            skLineSegment(sketch, "E7.22.0.7", {"start": v(2205.89, 99.85) * mm, "end": v(2205.89, 102.85) * mm});
            skLineSegment(sketch, "E7.22.0.8", {"start": v(2155.89, 99.85) * mm, "end": v(2155.89, 102.85) * mm});
            skArc(sketch, "E7.22.0.9", {"start": v(2186.39, 99.85) * mm, "mid": v(2183.56, 98.67) * mm, "end": v(2182.39, 95.85) * mm});
            skArc(sketch, "E7.22.0.10", {"start": v(2179.39, 95.85) * mm, "mid": v(2178.22, 98.67) * mm, "end": v(2175.39, 99.85) * mm});
            skArc(sketch, "E7.22.0.11", {"start": v(2175.39, -0.15) * mm, "mid": v(2178.22, 1.02) * mm, "end": v(2179.39, 3.85) * mm});
            skArc(sketch, "E7.22.0.12", {"start": v(2182.39, 3.85) * mm, "mid": v(2183.56, 1.02) * mm, "end": v(2186.39, -0.15) * mm});
            skPoint(sketch, "E7.23.0.0", {"position": v(2279.39, 99.85) * mm});
            skLineSegment(sketch, "E7.23.0.1", {"start": v(2255.89, 99.85) * mm, "end": v(2275.39, 99.85) * mm});
            skPoint(sketch, "E7.23.0.2", {"position": v(2282.39, 96.07) * mm});
            skLineSegment(sketch, "E7.23.0.3", {"start": v(2279.39, 95.85) * mm, "end": v(2279.39, 3.85) * mm});
            skLineSegment(sketch, "E7.23.0.4", {"start": v(2282.39, 95.85) * mm, "end": v(2282.39, 3.85) * mm});
            skLineSegment(sketch, "E7.23.0.5", {"start": v(2255.89, 102.85) * mm, "end": v(2305.89, 102.85) * mm});
            skLineSegment(sketch, "E7.23.0.6", {"start": v(2286.39, 99.85) * mm, "end": v(2305.89, 99.85) * mm});
            skLineSegment(sketch, "E7.23.0.7", {"start": v(2305.89, 99.85) * mm, "end": v(2305.89, 102.85) * mm});
            skLineSegment(sketch, "E7.23.0.8", {"start": v(2255.89, 99.85) * mm, "end": v(2255.89, 102.85) * mm});
            skArc(sketch, "E7.23.0.9", {"start": v(2286.39, 99.85) * mm, "mid": v(2283.56, 98.67) * mm, "end": v(2282.39, 95.85) * mm});
            skArc(sketch, "E7.23.0.10", {"start": v(2279.39, 95.85) * mm, "mid": v(2278.22, 98.67) * mm, "end": v(2275.39, 99.85) * mm});
            skArc(sketch, "E7.23.0.11", {"start": v(2275.39, -0.15) * mm, "mid": v(2278.22, 1.02) * mm, "end": v(2279.39, 3.85) * mm});
            skArc(sketch, "E7.23.0.12", {"start": v(2282.39, 3.85) * mm, "mid": v(2283.56, 1.02) * mm, "end": v(2286.39, -0.15) * mm});
            skPoint(sketch, "E7.24.0.0", {"position": v(2379.39, 99.85) * mm});
            skLineSegment(sketch, "E7.24.0.1", {"start": v(2355.89, 99.85) * mm, "end": v(2375.39, 99.85) * mm});
            skPoint(sketch, "E7.24.0.2", {"position": v(2382.39, 96.07) * mm});
            skLineSegment(sketch, "E7.24.0.3", {"start": v(2379.39, 95.85) * mm, "end": v(2379.39, 3.85) * mm});
            skLineSegment(sketch, "E7.24.0.4", {"start": v(2382.39, 95.85) * mm, "end": v(2382.39, 3.85) * mm});
            skLineSegment(sketch, "E7.24.0.5", {"start": v(2355.89, 102.85) * mm, "end": v(2405.89, 102.85) * mm});
            skLineSegment(sketch, "E7.24.0.6", {"start": v(2386.39, 99.85) * mm, "end": v(2405.89, 99.85) * mm});
            skLineSegment(sketch, "E7.24.0.7", {"start": v(2405.89, 99.85) * mm, "end": v(2405.89, 102.85) * mm});
            skLineSegment(sketch, "E7.24.0.8", {"start": v(2355.89, 99.85) * mm, "end": v(2355.89, 102.85) * mm});
            skArc(sketch, "E7.24.0.9", {"start": v(2386.39, 99.85) * mm, "mid": v(2383.56, 98.67) * mm, "end": v(2382.39, 95.85) * mm});
            skArc(sketch, "E7.24.0.10", {"start": v(2379.39, 95.85) * mm, "mid": v(2378.22, 98.67) * mm, "end": v(2375.39, 99.85) * mm});
            skArc(sketch, "E7.24.0.11", {"start": v(2375.39, -0.15) * mm, "mid": v(2378.22, 1.02) * mm, "end": v(2379.39, 3.85) * mm});
            skArc(sketch, "E7.24.0.12", {"start": v(2382.39, 3.85) * mm, "mid": v(2383.56, 1.02) * mm, "end": v(2386.39, -0.15) * mm});
            skPoint(sketch, "E7.25.0.0", {"position": v(2479.39, 99.85) * mm});
            skLineSegment(sketch, "E7.25.0.1", {"start": v(2455.89, 99.85) * mm, "end": v(2475.39, 99.85) * mm});
            skPoint(sketch, "E7.25.0.2", {"position": v(2482.39, 96.07) * mm});
            skLineSegment(sketch, "E7.25.0.3", {"start": v(2479.39, 95.85) * mm, "end": v(2479.39, 3.85) * mm});
            skLineSegment(sketch, "E7.25.0.4", {"start": v(2482.39, 95.85) * mm, "end": v(2482.39, 3.85) * mm});
            skLineSegment(sketch, "E7.25.0.5", {"start": v(2455.89, 102.85) * mm, "end": v(2505.89, 102.85) * mm});
            skLineSegment(sketch, "E7.25.0.6", {"start": v(2486.39, 99.85) * mm, "end": v(2505.89, 99.85) * mm});
            skLineSegment(sketch, "E7.25.0.7", {"start": v(2505.89, 99.85) * mm, "end": v(2505.89, 102.85) * mm});
            skLineSegment(sketch, "E7.25.0.8", {"start": v(2455.89, 99.85) * mm, "end": v(2455.89, 102.85) * mm});
            skArc(sketch, "E7.25.0.9", {"start": v(2486.39, 99.85) * mm, "mid": v(2483.56, 98.67) * mm, "end": v(2482.39, 95.85) * mm});
            skArc(sketch, "E7.25.0.10", {"start": v(2479.39, 95.85) * mm, "mid": v(2478.22, 98.67) * mm, "end": v(2475.39, 99.85) * mm});
            skArc(sketch, "E7.25.0.11", {"start": v(2475.39, -0.15) * mm, "mid": v(2478.22, 1.02) * mm, "end": v(2479.39, 3.85) * mm});
            skArc(sketch, "E7.25.0.12", {"start": v(2482.39, 3.85) * mm, "mid": v(2483.56, 1.02) * mm, "end": v(2486.39, -0.15) * mm});
            skPoint(sketch, "E7.26.0.0", {"position": v(2579.39, 99.85) * mm});
            skLineSegment(sketch, "E7.26.0.1", {"start": v(2555.89, 99.85) * mm, "end": v(2575.39, 99.85) * mm});
            skPoint(sketch, "E7.26.0.2", {"position": v(2582.39, 96.07) * mm});
            skLineSegment(sketch, "E7.26.0.3", {"start": v(2579.39, 95.85) * mm, "end": v(2579.39, 3.85) * mm});
            skLineSegment(sketch, "E7.26.0.4", {"start": v(2582.39, 95.85) * mm, "end": v(2582.39, 3.85) * mm});
            skLineSegment(sketch, "E7.26.0.5", {"start": v(2555.89, 102.85) * mm, "end": v(2605.89, 102.85) * mm});
            skLineSegment(sketch, "E7.26.0.6", {"start": v(2586.39, 99.85) * mm, "end": v(2605.89, 99.85) * mm});
            skLineSegment(sketch, "E7.26.0.7", {"start": v(2605.89, 99.85) * mm, "end": v(2605.89, 102.85) * mm});
            skLineSegment(sketch, "E7.26.0.8", {"start": v(2555.89, 99.85) * mm, "end": v(2555.89, 102.85) * mm});
            skArc(sketch, "E7.26.0.9", {"start": v(2586.39, 99.85) * mm, "mid": v(2583.56, 98.67) * mm, "end": v(2582.39, 95.85) * mm});
            skArc(sketch, "E7.26.0.10", {"start": v(2579.39, 95.85) * mm, "mid": v(2578.22, 98.67) * mm, "end": v(2575.39, 99.85) * mm});
            skArc(sketch, "E7.26.0.11", {"start": v(2575.39, -0.15) * mm, "mid": v(2578.22, 1.02) * mm, "end": v(2579.39, 3.85) * mm});
            skArc(sketch, "E7.26.0.12", {"start": v(2582.39, 3.85) * mm, "mid": v(2583.56, 1.02) * mm, "end": v(2586.39, -0.15) * mm});
            skPoint(sketch, "E7.27.0.0", {"position": v(2679.39, 99.85) * mm});
            skLineSegment(sketch, "E7.27.0.1", {"start": v(2655.89, 99.85) * mm, "end": v(2675.39, 99.85) * mm});
            skPoint(sketch, "E7.27.0.2", {"position": v(2682.39, 96.07) * mm});
            skLineSegment(sketch, "E7.27.0.3", {"start": v(2679.39, 95.85) * mm, "end": v(2679.39, 3.85) * mm});
            skLineSegment(sketch, "E7.27.0.4", {"start": v(2682.39, 95.85) * mm, "end": v(2682.39, 3.85) * mm});
            skLineSegment(sketch, "E7.27.0.5", {"start": v(2655.89, 102.85) * mm, "end": v(2705.89, 102.85) * mm});
            skLineSegment(sketch, "E7.27.0.6", {"start": v(2686.39, 99.85) * mm, "end": v(2705.89, 99.85) * mm});
            skLineSegment(sketch, "E7.27.0.7", {"start": v(2705.89, 99.85) * mm, "end": v(2705.89, 102.85) * mm});
            skLineSegment(sketch, "E7.27.0.8", {"start": v(2655.89, 99.85) * mm, "end": v(2655.89, 102.85) * mm});
            skArc(sketch, "E7.27.0.9", {"start": v(2686.39, 99.85) * mm, "mid": v(2683.56, 98.67) * mm, "end": v(2682.39, 95.85) * mm});
            skArc(sketch, "E7.27.0.10", {"start": v(2679.39, 95.85) * mm, "mid": v(2678.22, 98.67) * mm, "end": v(2675.39, 99.85) * mm});
            skArc(sketch, "E7.27.0.11", {"start": v(2675.39, -0.15) * mm, "mid": v(2678.22, 1.02) * mm, "end": v(2679.39, 3.85) * mm});
            skArc(sketch, "E7.27.0.12", {"start": v(2682.39, 3.85) * mm, "mid": v(2683.56, 1.02) * mm, "end": v(2686.39, -0.15) * mm});
            skPoint(sketch, "E7.28.0.0", {"position": v(2779.39, 99.85) * mm});
            skLineSegment(sketch, "E7.28.0.1", {"start": v(2755.89, 99.85) * mm, "end": v(2775.39, 99.85) * mm});
            skPoint(sketch, "E7.28.0.2", {"position": v(2782.39, 96.07) * mm});
            skLineSegment(sketch, "E7.28.0.3", {"start": v(2779.39, 95.85) * mm, "end": v(2779.39, 3.85) * mm});
            skLineSegment(sketch, "E7.28.0.4", {"start": v(2782.39, 95.85) * mm, "end": v(2782.39, 3.85) * mm});
            skLineSegment(sketch, "E7.28.0.5", {"start": v(2755.89, 102.85) * mm, "end": v(2805.89, 102.85) * mm});
            skLineSegment(sketch, "E7.28.0.6", {"start": v(2786.39, 99.85) * mm, "end": v(2805.89, 99.85) * mm});
            skLineSegment(sketch, "E7.28.0.7", {"start": v(2805.89, 99.85) * mm, "end": v(2805.89, 102.85) * mm});
            skLineSegment(sketch, "E7.28.0.8", {"start": v(2755.89, 99.85) * mm, "end": v(2755.89, 102.85) * mm});
            skArc(sketch, "E7.28.0.9", {"start": v(2786.39, 99.85) * mm, "mid": v(2783.56, 98.67) * mm, "end": v(2782.39, 95.85) * mm});
            skArc(sketch, "E7.28.0.10", {"start": v(2779.39, 95.85) * mm, "mid": v(2778.22, 98.67) * mm, "end": v(2775.39, 99.85) * mm});
            skArc(sketch, "E7.28.0.11", {"start": v(2775.39, -0.15) * mm, "mid": v(2778.22, 1.02) * mm, "end": v(2779.39, 3.85) * mm});
            skArc(sketch, "E7.28.0.12", {"start": v(2782.39, 3.85) * mm, "mid": v(2783.56, 1.02) * mm, "end": v(2786.39, -0.15) * mm});
            skPoint(sketch, "E7.29.0.0", {"position": v(2879.39, 99.85) * mm});
            skLineSegment(sketch, "E7.29.0.1", {"start": v(2855.89, 99.85) * mm, "end": v(2875.39, 99.85) * mm});
            skPoint(sketch, "E7.29.0.2", {"position": v(2882.39, 96.07) * mm});
            skLineSegment(sketch, "E7.29.0.3", {"start": v(2879.39, 95.85) * mm, "end": v(2879.39, 3.85) * mm});
            skLineSegment(sketch, "E7.29.0.4", {"start": v(2882.39, 95.85) * mm, "end": v(2882.39, 3.85) * mm});
            skLineSegment(sketch, "E7.29.0.5", {"start": v(2855.89, 102.85) * mm, "end": v(2905.89, 102.85) * mm});
            skLineSegment(sketch, "E7.29.0.6", {"start": v(2886.39, 99.85) * mm, "end": v(2905.89, 99.85) * mm});
            skLineSegment(sketch, "E7.29.0.7", {"start": v(2905.89, 99.85) * mm, "end": v(2905.89, 102.85) * mm});
            skLineSegment(sketch, "E7.29.0.8", {"start": v(2855.89, 99.85) * mm, "end": v(2855.89, 102.85) * mm});
            skArc(sketch, "E7.29.0.9", {"start": v(2886.39, 99.85) * mm, "mid": v(2883.56, 98.67) * mm, "end": v(2882.39, 95.85) * mm});
            skArc(sketch, "E7.29.0.10", {"start": v(2879.39, 95.85) * mm, "mid": v(2878.22, 98.67) * mm, "end": v(2875.39, 99.85) * mm});
            skArc(sketch, "E7.29.0.11", {"start": v(2875.39, -0.15) * mm, "mid": v(2878.22, 1.02) * mm, "end": v(2879.39, 3.85) * mm});
            skArc(sketch, "E7.29.0.12", {"start": v(2882.39, 3.85) * mm, "mid": v(2883.56, 1.02) * mm, "end": v(2886.39, -0.15) * mm});
            skPoint(sketch, "E7.30.0.0", {"position": v(2979.39, 99.85) * mm});
            skLineSegment(sketch, "E7.30.0.1", {"start": v(2955.89, 99.85) * mm, "end": v(2975.39, 99.85) * mm});
            skPoint(sketch, "E7.30.0.2", {"position": v(2982.39, 96.07) * mm});
            skLineSegment(sketch, "E7.30.0.3", {"start": v(2979.39, 95.85) * mm, "end": v(2979.39, 3.85) * mm});
            skLineSegment(sketch, "E7.30.0.4", {"start": v(2982.39, 95.85) * mm, "end": v(2982.39, 3.85) * mm});
            skLineSegment(sketch, "E7.30.0.5", {"start": v(2955.89, 102.85) * mm, "end": v(3005.89, 102.85) * mm});
            skLineSegment(sketch, "E7.30.0.6", {"start": v(2986.39, 99.85) * mm, "end": v(3005.89, 99.85) * mm});
            skLineSegment(sketch, "E7.30.0.7", {"start": v(3005.89, 99.85) * mm, "end": v(3005.89, 102.85) * mm});
            skLineSegment(sketch, "E7.30.0.8", {"start": v(2955.89, 99.85) * mm, "end": v(2955.89, 102.85) * mm});
            skArc(sketch, "E7.30.0.9", {"start": v(2986.39, 99.85) * mm, "mid": v(2983.56, 98.67) * mm, "end": v(2982.39, 95.85) * mm});
            skArc(sketch, "E7.30.0.10", {"start": v(2979.39, 95.85) * mm, "mid": v(2978.22, 98.67) * mm, "end": v(2975.39, 99.85) * mm});
            skArc(sketch, "E7.30.0.11", {"start": v(2975.39, -0.15) * mm, "mid": v(2978.22, 1.02) * mm, "end": v(2979.39, 3.85) * mm});
            skArc(sketch, "E7.30.0.12", {"start": v(2982.39, 3.85) * mm, "mid": v(2983.56, 1.02) * mm, "end": v(2986.39, -0.15) * mm});
            skPoint(sketch, "E7.31.0.0", {"position": v(3079.39, 99.85) * mm});
            skLineSegment(sketch, "E7.31.0.1", {"start": v(3055.89, 99.85) * mm, "end": v(3075.39, 99.85) * mm});
            skPoint(sketch, "E7.31.0.2", {"position": v(3082.39, 96.07) * mm});
            skLineSegment(sketch, "E7.31.0.3", {"start": v(3079.39, 95.85) * mm, "end": v(3079.39, 3.85) * mm});
            skLineSegment(sketch, "E7.31.0.4", {"start": v(3082.39, 95.85) * mm, "end": v(3082.39, 3.85) * mm});
            skLineSegment(sketch, "E7.31.0.5", {"start": v(3055.89, 102.85) * mm, "end": v(3105.89, 102.85) * mm});
            skLineSegment(sketch, "E7.31.0.6", {"start": v(3086.39, 99.85) * mm, "end": v(3105.89, 99.85) * mm});
            skLineSegment(sketch, "E7.31.0.7", {"start": v(3105.89, 99.85) * mm, "end": v(3105.89, 102.85) * mm});
            skLineSegment(sketch, "E7.31.0.8", {"start": v(3055.89, 99.85) * mm, "end": v(3055.89, 102.85) * mm});
            skArc(sketch, "E7.31.0.9", {"start": v(3086.39, 99.85) * mm, "mid": v(3083.56, 98.67) * mm, "end": v(3082.39, 95.85) * mm});
            skArc(sketch, "E7.31.0.10", {"start": v(3079.39, 95.85) * mm, "mid": v(3078.22, 98.67) * mm, "end": v(3075.39, 99.85) * mm});
            skArc(sketch, "E7.31.0.11", {"start": v(3075.39, -0.15) * mm, "mid": v(3078.22, 1.02) * mm, "end": v(3079.39, 3.85) * mm});
            skArc(sketch, "E7.31.0.12", {"start": v(3082.39, 3.85) * mm, "mid": v(3083.56, 1.02) * mm, "end": v(3086.39, -0.15) * mm});
            skPoint(sketch, "E7.32.0.0", {"position": v(3179.39, 99.85) * mm});
            skLineSegment(sketch, "E7.32.0.1", {"start": v(3155.89, 99.85) * mm, "end": v(3175.39, 99.85) * mm});
            skPoint(sketch, "E7.32.0.2", {"position": v(3182.39, 96.07) * mm});
            skLineSegment(sketch, "E7.32.0.3", {"start": v(3179.39, 95.85) * mm, "end": v(3179.39, 3.85) * mm});
            skLineSegment(sketch, "E7.32.0.4", {"start": v(3182.39, 95.85) * mm, "end": v(3182.39, 3.85) * mm});
            skLineSegment(sketch, "E7.32.0.5", {"start": v(3155.89, 102.85) * mm, "end": v(3205.89, 102.85) * mm});
            skLineSegment(sketch, "E7.32.0.6", {"start": v(3186.39, 99.85) * mm, "end": v(3205.89, 99.85) * mm});
            skLineSegment(sketch, "E7.32.0.7", {"start": v(3205.89, 99.85) * mm, "end": v(3205.89, 102.85) * mm});
            skLineSegment(sketch, "E7.32.0.8", {"start": v(3155.89, 99.85) * mm, "end": v(3155.89, 102.85) * mm});
            skArc(sketch, "E7.32.0.9", {"start": v(3186.39, 99.85) * mm, "mid": v(3183.56, 98.67) * mm, "end": v(3182.39, 95.85) * mm});
            skArc(sketch, "E7.32.0.10", {"start": v(3179.39, 95.85) * mm, "mid": v(3178.22, 98.67) * mm, "end": v(3175.39, 99.85) * mm});
            skArc(sketch, "E7.32.0.11", {"start": v(3175.39, -0.15) * mm, "mid": v(3178.22, 1.02) * mm, "end": v(3179.39, 3.85) * mm});
            skArc(sketch, "E7.32.0.12", {"start": v(3182.39, 3.85) * mm, "mid": v(3183.56, 1.02) * mm, "end": v(3186.39, -0.15) * mm});
            skPoint(sketch, "E7.33.0.0", {"position": v(3279.39, 99.85) * mm});
            skLineSegment(sketch, "E7.33.0.1", {"start": v(3255.89, 99.85) * mm, "end": v(3275.39, 99.85) * mm});
            skPoint(sketch, "E7.33.0.2", {"position": v(3282.39, 96.07) * mm});
            skLineSegment(sketch, "E7.33.0.3", {"start": v(3279.39, 95.85) * mm, "end": v(3279.39, 3.85) * mm});
            skLineSegment(sketch, "E7.33.0.4", {"start": v(3282.39, 95.85) * mm, "end": v(3282.39, 3.85) * mm});
            skLineSegment(sketch, "E7.33.0.5", {"start": v(3255.89, 102.85) * mm, "end": v(3305.89, 102.85) * mm});
            skLineSegment(sketch, "E7.33.0.6", {"start": v(3286.39, 99.85) * mm, "end": v(3305.89, 99.85) * mm});
            skLineSegment(sketch, "E7.33.0.7", {"start": v(3305.89, 99.85) * mm, "end": v(3305.89, 102.85) * mm});
            skLineSegment(sketch, "E7.33.0.8", {"start": v(3255.89, 99.85) * mm, "end": v(3255.89, 102.85) * mm});
            skArc(sketch, "E7.33.0.9", {"start": v(3286.39, 99.85) * mm, "mid": v(3283.56, 98.67) * mm, "end": v(3282.39, 95.85) * mm});
            skArc(sketch, "E7.33.0.10", {"start": v(3279.39, 95.85) * mm, "mid": v(3278.22, 98.67) * mm, "end": v(3275.39, 99.85) * mm});
            skArc(sketch, "E7.33.0.11", {"start": v(3275.39, -0.15) * mm, "mid": v(3278.22, 1.02) * mm, "end": v(3279.39, 3.85) * mm});
            skArc(sketch, "E7.33.0.12", {"start": v(3282.39, 3.85) * mm, "mid": v(3283.56, 1.02) * mm, "end": v(3286.39, -0.15) * mm});
            skPoint(sketch, "E7.34.0.0", {"position": v(3379.39, 99.85) * mm});
            skLineSegment(sketch, "E7.34.0.1", {"start": v(3355.89, 99.85) * mm, "end": v(3375.39, 99.85) * mm});
            skPoint(sketch, "E7.34.0.2", {"position": v(3382.39, 96.07) * mm});
            skLineSegment(sketch, "E7.34.0.3", {"start": v(3379.39, 95.85) * mm, "end": v(3379.39, 3.85) * mm});
            skLineSegment(sketch, "E7.34.0.4", {"start": v(3382.39, 95.85) * mm, "end": v(3382.39, 3.85) * mm});
            skLineSegment(sketch, "E7.34.0.5", {"start": v(3355.89, 102.85) * mm, "end": v(3405.89, 102.85) * mm});
            skLineSegment(sketch, "E7.34.0.6", {"start": v(3386.39, 99.85) * mm, "end": v(3405.89, 99.85) * mm});
            skLineSegment(sketch, "E7.34.0.7", {"start": v(3405.89, 99.85) * mm, "end": v(3405.89, 102.85) * mm});
            skLineSegment(sketch, "E7.34.0.8", {"start": v(3355.89, 99.85) * mm, "end": v(3355.89, 102.85) * mm});
            skArc(sketch, "E7.34.0.9", {"start": v(3386.39, 99.85) * mm, "mid": v(3383.56, 98.67) * mm, "end": v(3382.39, 95.85) * mm});
            skArc(sketch, "E7.34.0.10", {"start": v(3379.39, 95.85) * mm, "mid": v(3378.22, 98.67) * mm, "end": v(3375.39, 99.85) * mm});
            skArc(sketch, "E7.34.0.11", {"start": v(3375.39, -0.15) * mm, "mid": v(3378.22, 1.02) * mm, "end": v(3379.39, 3.85) * mm});
            skArc(sketch, "E7.34.0.12", {"start": v(3382.39, 3.85) * mm, "mid": v(3383.56, 1.02) * mm, "end": v(3386.39, -0.15) * mm});
            skPoint(sketch, "E7.35.0.0", {"position": v(3479.39, 99.85) * mm});
            skLineSegment(sketch, "E7.35.0.1", {"start": v(3455.89, 99.85) * mm, "end": v(3475.39, 99.85) * mm});
            skPoint(sketch, "E7.35.0.2", {"position": v(3482.39, 96.07) * mm});
            skLineSegment(sketch, "E7.35.0.3", {"start": v(3479.39, 95.85) * mm, "end": v(3479.39, 3.85) * mm});
            skLineSegment(sketch, "E7.35.0.4", {"start": v(3482.39, 95.85) * mm, "end": v(3482.39, 3.85) * mm});
            skLineSegment(sketch, "E7.35.0.5", {"start": v(3455.89, 102.85) * mm, "end": v(3505.89, 102.85) * mm});
            skLineSegment(sketch, "E7.35.0.6", {"start": v(3486.39, 99.85) * mm, "end": v(3505.89, 99.85) * mm});
            skLineSegment(sketch, "E7.35.0.7", {"start": v(3505.89, 99.85) * mm, "end": v(3505.89, 102.85) * mm});
            skLineSegment(sketch, "E7.35.0.8", {"start": v(3455.89, 99.85) * mm, "end": v(3455.89, 102.85) * mm});
            skArc(sketch, "E7.35.0.9", {"start": v(3486.39, 99.85) * mm, "mid": v(3483.56, 98.67) * mm, "end": v(3482.39, 95.85) * mm});
            skArc(sketch, "E7.35.0.10", {"start": v(3479.39, 95.85) * mm, "mid": v(3478.22, 98.67) * mm, "end": v(3475.39, 99.85) * mm});
            skArc(sketch, "E7.35.0.11", {"start": v(3475.39, -0.15) * mm, "mid": v(3478.22, 1.02) * mm, "end": v(3479.39, 3.85) * mm});
            skArc(sketch, "E7.35.0.12", {"start": v(3482.39, 3.85) * mm, "mid": v(3483.56, 1.02) * mm, "end": v(3486.39, -0.15) * mm});
            skPoint(sketch, "E7.36.0.0", {"position": v(3579.39, 99.85) * mm});
            skLineSegment(sketch, "E7.36.0.1", {"start": v(3555.89, 99.85) * mm, "end": v(3575.39, 99.85) * mm});
            skPoint(sketch, "E7.36.0.2", {"position": v(3582.39, 96.07) * mm});
            skLineSegment(sketch, "E7.36.0.3", {"start": v(3579.39, 95.85) * mm, "end": v(3579.39, 3.85) * mm});
            skLineSegment(sketch, "E7.36.0.4", {"start": v(3582.39, 95.85) * mm, "end": v(3582.39, 3.85) * mm});
            skLineSegment(sketch, "E7.36.0.5", {"start": v(3555.89, 102.85) * mm, "end": v(3605.89, 102.85) * mm});
            skLineSegment(sketch, "E7.36.0.6", {"start": v(3586.39, 99.85) * mm, "end": v(3605.89, 99.85) * mm});
            skLineSegment(sketch, "E7.36.0.7", {"start": v(3605.89, 99.85) * mm, "end": v(3605.89, 102.85) * mm});
            skLineSegment(sketch, "E7.36.0.8", {"start": v(3555.89, 99.85) * mm, "end": v(3555.89, 102.85) * mm});
            skArc(sketch, "E7.36.0.9", {"start": v(3586.39, 99.85) * mm, "mid": v(3583.56, 98.67) * mm, "end": v(3582.39, 95.85) * mm});
            skArc(sketch, "E7.36.0.10", {"start": v(3579.39, 95.85) * mm, "mid": v(3578.22, 98.67) * mm, "end": v(3575.39, 99.85) * mm});
            skArc(sketch, "E7.36.0.11", {"start": v(3575.39, -0.15) * mm, "mid": v(3578.22, 1.02) * mm, "end": v(3579.39, 3.85) * mm});
            skArc(sketch, "E7.36.0.12", {"start": v(3582.39, 3.85) * mm, "mid": v(3583.56, 1.02) * mm, "end": v(3586.39, -0.15) * mm});
            skPoint(sketch, "E7.37.0.0", {"position": v(3679.39, 99.85) * mm});
            skLineSegment(sketch, "E7.37.0.1", {"start": v(3655.89, 99.85) * mm, "end": v(3675.39, 99.85) * mm});
            skPoint(sketch, "E7.37.0.2", {"position": v(3682.39, 96.07) * mm});
            skLineSegment(sketch, "E7.37.0.3", {"start": v(3679.39, 95.85) * mm, "end": v(3679.39, 3.85) * mm});
            skLineSegment(sketch, "E7.37.0.4", {"start": v(3682.39, 95.85) * mm, "end": v(3682.39, 3.85) * mm});
            skLineSegment(sketch, "E7.37.0.5", {"start": v(3655.89, 102.85) * mm, "end": v(3705.89, 102.85) * mm});
            skLineSegment(sketch, "E7.37.0.6", {"start": v(3686.39, 99.85) * mm, "end": v(3705.89, 99.85) * mm});
            skLineSegment(sketch, "E7.37.0.7", {"start": v(3705.89, 99.85) * mm, "end": v(3705.89, 102.85) * mm});
            skLineSegment(sketch, "E7.37.0.8", {"start": v(3655.89, 99.85) * mm, "end": v(3655.89, 102.85) * mm});
            skArc(sketch, "E7.37.0.9", {"start": v(3686.39, 99.85) * mm, "mid": v(3683.56, 98.67) * mm, "end": v(3682.39, 95.85) * mm});
            skArc(sketch, "E7.37.0.10", {"start": v(3679.39, 95.85) * mm, "mid": v(3678.22, 98.67) * mm, "end": v(3675.39, 99.85) * mm});
            skArc(sketch, "E7.37.0.11", {"start": v(3675.39, -0.15) * mm, "mid": v(3678.22, 1.02) * mm, "end": v(3679.39, 3.85) * mm});
            skArc(sketch, "E7.37.0.12", {"start": v(3682.39, 3.85) * mm, "mid": v(3683.56, 1.02) * mm, "end": v(3686.39, -0.15) * mm});
            skPoint(sketch, "E7.38.0.0", {"position": v(3779.39, 99.85) * mm});
            skLineSegment(sketch, "E7.38.0.1", {"start": v(3755.89, 99.85) * mm, "end": v(3775.39, 99.85) * mm});
            skPoint(sketch, "E7.38.0.2", {"position": v(3782.39, 96.07) * mm});
            skLineSegment(sketch, "E7.38.0.3", {"start": v(3779.39, 95.85) * mm, "end": v(3779.39, 3.85) * mm});
            skLineSegment(sketch, "E7.38.0.4", {"start": v(3782.39, 95.85) * mm, "end": v(3782.39, 3.85) * mm});
            skLineSegment(sketch, "E7.38.0.5", {"start": v(3755.89, 102.85) * mm, "end": v(3805.89, 102.85) * mm});
            skLineSegment(sketch, "E7.38.0.6", {"start": v(3786.39, 99.85) * mm, "end": v(3805.89, 99.85) * mm});
            skLineSegment(sketch, "E7.38.0.7", {"start": v(3805.89, 99.85) * mm, "end": v(3805.89, 102.85) * mm});
            skLineSegment(sketch, "E7.38.0.8", {"start": v(3755.89, 99.85) * mm, "end": v(3755.89, 102.85) * mm});
            skArc(sketch, "E7.38.0.9", {"start": v(3786.39, 99.85) * mm, "mid": v(3783.56, 98.67) * mm, "end": v(3782.39, 95.85) * mm});
            skArc(sketch, "E7.38.0.10", {"start": v(3779.39, 95.85) * mm, "mid": v(3778.22, 98.67) * mm, "end": v(3775.39, 99.85) * mm});
            skArc(sketch, "E7.38.0.11", {"start": v(3775.39, -0.15) * mm, "mid": v(3778.22, 1.02) * mm, "end": v(3779.39, 3.85) * mm});
            skArc(sketch, "E7.38.0.12", {"start": v(3782.39, 3.85) * mm, "mid": v(3783.56, 1.02) * mm, "end": v(3786.39, -0.15) * mm});
            skPoint(sketch, "E7.39.0.0", {"position": v(3879.39, 99.85) * mm});
            skLineSegment(sketch, "E7.39.0.1", {"start": v(3855.89, 99.85) * mm, "end": v(3875.39, 99.85) * mm});
            skPoint(sketch, "E7.39.0.2", {"position": v(3882.39, 96.07) * mm});
            skLineSegment(sketch, "E7.39.0.3", {"start": v(3879.39, 95.85) * mm, "end": v(3879.39, 3.85) * mm});
            skLineSegment(sketch, "E7.39.0.4", {"start": v(3882.39, 95.85) * mm, "end": v(3882.39, 3.85) * mm});
            skLineSegment(sketch, "E7.39.0.5", {"start": v(3855.89, 102.85) * mm, "end": v(3905.89, 102.85) * mm});
            skLineSegment(sketch, "E7.39.0.6", {"start": v(3886.39, 99.85) * mm, "end": v(3905.89, 99.85) * mm});
            skLineSegment(sketch, "E7.39.0.7", {"start": v(3905.89, 99.85) * mm, "end": v(3905.89, 102.85) * mm});
            skLineSegment(sketch, "E7.39.0.8", {"start": v(3855.89, 99.85) * mm, "end": v(3855.89, 102.85) * mm});
            skArc(sketch, "E7.39.0.9", {"start": v(3886.39, 99.85) * mm, "mid": v(3883.56, 98.67) * mm, "end": v(3882.39, 95.85) * mm});
            skArc(sketch, "E7.39.0.10", {"start": v(3879.39, 95.85) * mm, "mid": v(3878.22, 98.67) * mm, "end": v(3875.39, 99.85) * mm});
            skArc(sketch, "E7.39.0.11", {"start": v(3875.39, -0.15) * mm, "mid": v(3878.22, 1.02) * mm, "end": v(3879.39, 3.85) * mm});
            skArc(sketch, "E7.39.0.12", {"start": v(3882.39, 3.85) * mm, "mid": v(3883.56, 1.02) * mm, "end": v(3886.39, -0.15) * mm});
            skPoint(sketch, "E7.40.0.0", {"position": v(3979.39, 99.85) * mm});
            skLineSegment(sketch, "E7.40.0.1", {"start": v(3955.89, 99.85) * mm, "end": v(3975.39, 99.85) * mm});
            skPoint(sketch, "E7.40.0.2", {"position": v(3982.39, 96.07) * mm});
            skLineSegment(sketch, "E7.40.0.3", {"start": v(3979.39, 95.85) * mm, "end": v(3979.39, 3.85) * mm});
            skLineSegment(sketch, "E7.40.0.4", {"start": v(3982.39, 95.85) * mm, "end": v(3982.39, 3.85) * mm});
            skLineSegment(sketch, "E7.40.0.5", {"start": v(3955.89, 102.85) * mm, "end": v(4005.89, 102.85) * mm});
            skLineSegment(sketch, "E7.40.0.6", {"start": v(3986.39, 99.85) * mm, "end": v(4005.89, 99.85) * mm});
            skLineSegment(sketch, "E7.40.0.7", {"start": v(4005.89, 99.85) * mm, "end": v(4005.89, 102.85) * mm});
            skLineSegment(sketch, "E7.40.0.8", {"start": v(3955.89, 99.85) * mm, "end": v(3955.89, 102.85) * mm});
            skArc(sketch, "E7.40.0.9", {"start": v(3986.39, 99.85) * mm, "mid": v(3983.56, 98.67) * mm, "end": v(3982.39, 95.85) * mm});
            skArc(sketch, "E7.40.0.10", {"start": v(3979.39, 95.85) * mm, "mid": v(3978.22, 98.67) * mm, "end": v(3975.39, 99.85) * mm});
            skArc(sketch, "E7.40.0.11", {"start": v(3975.39, -0.15) * mm, "mid": v(3978.22, 1.02) * mm, "end": v(3979.39, 3.85) * mm});
            skArc(sketch, "E7.40.0.12", {"start": v(3982.39, 3.85) * mm, "mid": v(3983.56, 1.02) * mm, "end": v(3986.39, -0.15) * mm});
            skPoint(sketch, "E7.41.0.0", {"position": v(4079.39, 99.85) * mm});
            skLineSegment(sketch, "E7.41.0.1", {"start": v(4055.89, 99.85) * mm, "end": v(4075.39, 99.85) * mm});
            skPoint(sketch, "E7.41.0.2", {"position": v(4082.39, 96.07) * mm});
            skLineSegment(sketch, "E7.41.0.3", {"start": v(4079.39, 95.85) * mm, "end": v(4079.39, 3.85) * mm});
            skLineSegment(sketch, "E7.41.0.4", {"start": v(4082.39, 95.85) * mm, "end": v(4082.39, 3.85) * mm});
            skLineSegment(sketch, "E7.41.0.5", {"start": v(4055.89, 102.85) * mm, "end": v(4105.89, 102.85) * mm});
            skLineSegment(sketch, "E7.41.0.6", {"start": v(4086.39, 99.85) * mm, "end": v(4105.89, 99.85) * mm});
            skLineSegment(sketch, "E7.41.0.7", {"start": v(4105.89, 99.85) * mm, "end": v(4105.89, 102.85) * mm});
            skLineSegment(sketch, "E7.41.0.8", {"start": v(4055.89, 99.85) * mm, "end": v(4055.89, 102.85) * mm});
            skArc(sketch, "E7.41.0.9", {"start": v(4086.39, 99.85) * mm, "mid": v(4083.56, 98.67) * mm, "end": v(4082.39, 95.85) * mm});
            skArc(sketch, "E7.41.0.10", {"start": v(4079.39, 95.85) * mm, "mid": v(4078.22, 98.67) * mm, "end": v(4075.39, 99.85) * mm});
            skArc(sketch, "E7.41.0.11", {"start": v(4075.39, -0.15) * mm, "mid": v(4078.22, 1.02) * mm, "end": v(4079.39, 3.85) * mm});
            skArc(sketch, "E7.41.0.12", {"start": v(4082.39, 3.85) * mm, "mid": v(4083.56, 1.02) * mm, "end": v(4086.39, -0.15) * mm});
            skPoint(sketch, "E7.42.0.0", {"position": v(4179.39, 99.85) * mm});
            skLineSegment(sketch, "E7.42.0.1", {"start": v(4155.89, 99.85) * mm, "end": v(4175.39, 99.85) * mm});
            skPoint(sketch, "E7.42.0.2", {"position": v(4182.39, 96.07) * mm});
            skLineSegment(sketch, "E7.42.0.3", {"start": v(4179.39, 95.85) * mm, "end": v(4179.39, 3.85) * mm});
            skLineSegment(sketch, "E7.42.0.4", {"start": v(4182.39, 95.85) * mm, "end": v(4182.39, 3.85) * mm});
            skLineSegment(sketch, "E7.42.0.5", {"start": v(4155.89, 102.85) * mm, "end": v(4205.89, 102.85) * mm});
            skLineSegment(sketch, "E7.42.0.6", {"start": v(4186.39, 99.85) * mm, "end": v(4205.89, 99.85) * mm});
            skLineSegment(sketch, "E7.42.0.7", {"start": v(4205.89, 99.85) * mm, "end": v(4205.89, 102.85) * mm});
            skLineSegment(sketch, "E7.42.0.8", {"start": v(4155.89, 99.85) * mm, "end": v(4155.89, 102.85) * mm});
            skArc(sketch, "E7.42.0.9", {"start": v(4186.39, 99.85) * mm, "mid": v(4183.56, 98.67) * mm, "end": v(4182.39, 95.85) * mm});
            skArc(sketch, "E7.42.0.10", {"start": v(4179.39, 95.85) * mm, "mid": v(4178.22, 98.67) * mm, "end": v(4175.39, 99.85) * mm});
            skArc(sketch, "E7.42.0.11", {"start": v(4175.39, -0.15) * mm, "mid": v(4178.22, 1.02) * mm, "end": v(4179.39, 3.85) * mm});
            skArc(sketch, "E7.42.0.12", {"start": v(4182.39, 3.85) * mm, "mid": v(4183.56, 1.02) * mm, "end": v(4186.39, -0.15) * mm});
            skPoint(sketch, "E7.43.0.0", {"position": v(4279.39, 99.85) * mm});
            skLineSegment(sketch, "E7.43.0.1", {"start": v(4255.89, 99.85) * mm, "end": v(4275.39, 99.85) * mm});
            skPoint(sketch, "E7.43.0.2", {"position": v(4282.39, 96.07) * mm});
            skLineSegment(sketch, "E7.43.0.3", {"start": v(4279.39, 95.85) * mm, "end": v(4279.39, 3.85) * mm});
            skLineSegment(sketch, "E7.43.0.4", {"start": v(4282.39, 95.85) * mm, "end": v(4282.39, 3.85) * mm});
            skLineSegment(sketch, "E7.43.0.5", {"start": v(4255.89, 102.85) * mm, "end": v(4305.89, 102.85) * mm});
            skLineSegment(sketch, "E7.43.0.6", {"start": v(4286.39, 99.85) * mm, "end": v(4305.89, 99.85) * mm});
            skLineSegment(sketch, "E7.43.0.7", {"start": v(4305.89, 99.85) * mm, "end": v(4305.89, 102.85) * mm});
            skLineSegment(sketch, "E7.43.0.8", {"start": v(4255.89, 99.85) * mm, "end": v(4255.89, 102.85) * mm});
            skArc(sketch, "E7.43.0.9", {"start": v(4286.39, 99.85) * mm, "mid": v(4283.56, 98.67) * mm, "end": v(4282.39, 95.85) * mm});
            skArc(sketch, "E7.43.0.10", {"start": v(4279.39, 95.85) * mm, "mid": v(4278.22, 98.67) * mm, "end": v(4275.39, 99.85) * mm});
            skArc(sketch, "E7.43.0.11", {"start": v(4275.39, -0.15) * mm, "mid": v(4278.22, 1.02) * mm, "end": v(4279.39, 3.85) * mm});
            skArc(sketch, "E7.43.0.12", {"start": v(4282.39, 3.85) * mm, "mid": v(4283.56, 1.02) * mm, "end": v(4286.39, -0.15) * mm});
            skPoint(sketch, "E7.44.0.0", {"position": v(4379.39, 99.85) * mm});
            skLineSegment(sketch, "E7.44.0.1", {"start": v(4355.89, 99.85) * mm, "end": v(4375.39, 99.85) * mm});
            skPoint(sketch, "E7.44.0.2", {"position": v(4382.39, 96.07) * mm});
            skLineSegment(sketch, "E7.44.0.3", {"start": v(4379.39, 95.85) * mm, "end": v(4379.39, 3.85) * mm});
            skLineSegment(sketch, "E7.44.0.4", {"start": v(4382.39, 95.85) * mm, "end": v(4382.39, 3.85) * mm});
            skLineSegment(sketch, "E7.44.0.5", {"start": v(4355.89, 102.85) * mm, "end": v(4405.89, 102.85) * mm});
            skLineSegment(sketch, "E7.44.0.6", {"start": v(4386.39, 99.85) * mm, "end": v(4405.89, 99.85) * mm});
            skLineSegment(sketch, "E7.44.0.7", {"start": v(4405.89, 99.85) * mm, "end": v(4405.89, 102.85) * mm});
            skLineSegment(sketch, "E7.44.0.8", {"start": v(4355.89, 99.85) * mm, "end": v(4355.89, 102.85) * mm});
            skArc(sketch, "E7.44.0.9", {"start": v(4386.39, 99.85) * mm, "mid": v(4383.56, 98.67) * mm, "end": v(4382.39, 95.85) * mm});
            skArc(sketch, "E7.44.0.10", {"start": v(4379.39, 95.85) * mm, "mid": v(4378.22, 98.67) * mm, "end": v(4375.39, 99.85) * mm});
            skArc(sketch, "E7.44.0.11", {"start": v(4375.39, -0.15) * mm, "mid": v(4378.22, 1.02) * mm, "end": v(4379.39, 3.85) * mm});
            skArc(sketch, "E7.44.0.12", {"start": v(4382.39, 3.85) * mm, "mid": v(4383.56, 1.02) * mm, "end": v(4386.39, -0.15) * mm});
            skPoint(sketch, "E7.45.0.0", {"position": v(4479.39, 99.85) * mm});
            skLineSegment(sketch, "E7.45.0.1", {"start": v(4455.89, 99.85) * mm, "end": v(4475.39, 99.85) * mm});
            skPoint(sketch, "E7.45.0.2", {"position": v(4482.39, 96.07) * mm});
            skLineSegment(sketch, "E7.45.0.3", {"start": v(4479.39, 95.85) * mm, "end": v(4479.39, 3.85) * mm});
            skLineSegment(sketch, "E7.45.0.4", {"start": v(4482.39, 95.85) * mm, "end": v(4482.39, 3.85) * mm});
            skLineSegment(sketch, "E7.45.0.5", {"start": v(4455.89, 102.85) * mm, "end": v(4505.89, 102.85) * mm});
            skLineSegment(sketch, "E7.45.0.6", {"start": v(4486.39, 99.85) * mm, "end": v(4505.89, 99.85) * mm});
            skLineSegment(sketch, "E7.45.0.7", {"start": v(4505.89, 99.85) * mm, "end": v(4505.89, 102.85) * mm});
            skLineSegment(sketch, "E7.45.0.8", {"start": v(4455.89, 99.85) * mm, "end": v(4455.89, 102.85) * mm});
            skArc(sketch, "E7.45.0.9", {"start": v(4486.39, 99.85) * mm, "mid": v(4483.56, 98.67) * mm, "end": v(4482.39, 95.85) * mm});
            skArc(sketch, "E7.45.0.10", {"start": v(4479.39, 95.85) * mm, "mid": v(4478.22, 98.67) * mm, "end": v(4475.39, 99.85) * mm});
            skArc(sketch, "E7.45.0.11", {"start": v(4475.39, -0.15) * mm, "mid": v(4478.22, 1.02) * mm, "end": v(4479.39, 3.85) * mm});
            skArc(sketch, "E7.45.0.12", {"start": v(4482.39, 3.85) * mm, "mid": v(4483.56, 1.02) * mm, "end": v(4486.39, -0.15) * mm});
            skPoint(sketch, "E7.46.0.0", {"position": v(4579.39, 99.85) * mm});
            skLineSegment(sketch, "E7.46.0.1", {"start": v(4555.89, 99.85) * mm, "end": v(4575.39, 99.85) * mm});
            skPoint(sketch, "E7.46.0.2", {"position": v(4582.39, 96.07) * mm});
            skLineSegment(sketch, "E7.46.0.3", {"start": v(4579.39, 95.85) * mm, "end": v(4579.39, 3.85) * mm});
            skLineSegment(sketch, "E7.46.0.4", {"start": v(4582.39, 95.85) * mm, "end": v(4582.39, 3.85) * mm});
            skLineSegment(sketch, "E7.46.0.5", {"start": v(4555.89, 102.85) * mm, "end": v(4605.89, 102.85) * mm});
            skLineSegment(sketch, "E7.46.0.6", {"start": v(4586.39, 99.85) * mm, "end": v(4605.89, 99.85) * mm});
            skLineSegment(sketch, "E7.46.0.7", {"start": v(4605.89, 99.85) * mm, "end": v(4605.89, 102.85) * mm});
            skLineSegment(sketch, "E7.46.0.8", {"start": v(4555.89, 99.85) * mm, "end": v(4555.89, 102.85) * mm});
            skArc(sketch, "E7.46.0.9", {"start": v(4586.39, 99.85) * mm, "mid": v(4583.56, 98.67) * mm, "end": v(4582.39, 95.85) * mm});
            skArc(sketch, "E7.46.0.10", {"start": v(4579.39, 95.85) * mm, "mid": v(4578.22, 98.67) * mm, "end": v(4575.39, 99.85) * mm});
            skArc(sketch, "E7.46.0.11", {"start": v(4575.39, -0.15) * mm, "mid": v(4578.22, 1.02) * mm, "end": v(4579.39, 3.85) * mm});
            skArc(sketch, "E7.46.0.12", {"start": v(4582.39, 3.85) * mm, "mid": v(4583.56, 1.02) * mm, "end": v(4586.39, -0.15) * mm});
            skPoint(sketch, "E7.47.0.0", {"position": v(4679.39, 99.85) * mm});
            skLineSegment(sketch, "E7.47.0.1", {"start": v(4655.89, 99.85) * mm, "end": v(4675.39, 99.85) * mm});
            skPoint(sketch, "E7.47.0.2", {"position": v(4682.39, 96.07) * mm});
            skLineSegment(sketch, "E7.47.0.3", {"start": v(4679.39, 95.85) * mm, "end": v(4679.39, 3.85) * mm});
            skLineSegment(sketch, "E7.47.0.4", {"start": v(4682.39, 95.85) * mm, "end": v(4682.39, 3.85) * mm});
            skLineSegment(sketch, "E7.47.0.5", {"start": v(4655.89, 102.85) * mm, "end": v(4705.89, 102.85) * mm});
            skLineSegment(sketch, "E7.47.0.6", {"start": v(4686.39, 99.85) * mm, "end": v(4705.89, 99.85) * mm});
            skLineSegment(sketch, "E7.47.0.7", {"start": v(4705.89, 99.85) * mm, "end": v(4705.89, 102.85) * mm});
            skLineSegment(sketch, "E7.47.0.8", {"start": v(4655.89, 99.85) * mm, "end": v(4655.89, 102.85) * mm});
            skArc(sketch, "E7.47.0.9", {"start": v(4686.39, 99.85) * mm, "mid": v(4683.56, 98.67) * mm, "end": v(4682.39, 95.85) * mm});
            skArc(sketch, "E7.47.0.10", {"start": v(4679.39, 95.85) * mm, "mid": v(4678.22, 98.67) * mm, "end": v(4675.39, 99.85) * mm});
            skArc(sketch, "E7.47.0.11", {"start": v(4675.39, -0.15) * mm, "mid": v(4678.22, 1.02) * mm, "end": v(4679.39, 3.85) * mm});
            skArc(sketch, "E7.47.0.12", {"start": v(4682.39, 3.85) * mm, "mid": v(4683.56, 1.02) * mm, "end": v(4686.39, -0.15) * mm});
            skPoint(sketch, "E7.48.0.0", {"position": v(4779.39, 99.85) * mm});
            skLineSegment(sketch, "E7.48.0.1", {"start": v(4755.89, 99.85) * mm, "end": v(4775.39, 99.85) * mm});
            skPoint(sketch, "E7.48.0.2", {"position": v(4782.39, 96.07) * mm});
            skLineSegment(sketch, "E7.48.0.3", {"start": v(4779.39, 95.85) * mm, "end": v(4779.39, 3.85) * mm});
            skLineSegment(sketch, "E7.48.0.4", {"start": v(4782.39, 95.85) * mm, "end": v(4782.39, 3.85) * mm});
            skLineSegment(sketch, "E7.48.0.5", {"start": v(4755.89, 102.85) * mm, "end": v(4805.89, 102.85) * mm});
            skLineSegment(sketch, "E7.48.0.6", {"start": v(4786.39, 99.85) * mm, "end": v(4805.89, 99.85) * mm});
            skLineSegment(sketch, "E7.48.0.7", {"start": v(4805.89, 99.85) * mm, "end": v(4805.89, 102.85) * mm});
            skLineSegment(sketch, "E7.48.0.8", {"start": v(4755.89, 99.85) * mm, "end": v(4755.89, 102.85) * mm});
            skArc(sketch, "E7.48.0.9", {"start": v(4786.39, 99.85) * mm, "mid": v(4783.56, 98.67) * mm, "end": v(4782.39, 95.85) * mm});
            skArc(sketch, "E7.48.0.10", {"start": v(4779.39, 95.85) * mm, "mid": v(4778.22, 98.67) * mm, "end": v(4775.39, 99.85) * mm});
            skArc(sketch, "E7.48.0.11", {"start": v(4775.39, -0.15) * mm, "mid": v(4778.22, 1.02) * mm, "end": v(4779.39, 3.85) * mm});
            skArc(sketch, "E7.48.0.12", {"start": v(4782.39, 3.85) * mm, "mid": v(4783.56, 1.02) * mm, "end": v(4786.39, -0.15) * mm});
            skPoint(sketch, "E7.49.0.0", {"position": v(4879.39, 99.85) * mm});
            skLineSegment(sketch, "E7.49.0.1", {"start": v(4855.89, 99.85) * mm, "end": v(4875.39, 99.85) * mm});
            skPoint(sketch, "E7.49.0.2", {"position": v(4882.39, 96.07) * mm});
            skLineSegment(sketch, "E7.49.0.3", {"start": v(4879.39, 95.85) * mm, "end": v(4879.39, 3.85) * mm});
            skLineSegment(sketch, "E7.49.0.4", {"start": v(4882.39, 95.85) * mm, "end": v(4882.39, 3.85) * mm});
            skLineSegment(sketch, "E7.49.0.5", {"start": v(4855.89, 102.85) * mm, "end": v(4905.89, 102.85) * mm});
            skLineSegment(sketch, "E7.49.0.6", {"start": v(4886.39, 99.85) * mm, "end": v(4905.89, 99.85) * mm});
            skLineSegment(sketch, "E7.49.0.7", {"start": v(4905.89, 99.85) * mm, "end": v(4905.89, 102.85) * mm});
            skLineSegment(sketch, "E7.49.0.8", {"start": v(4855.89, 99.85) * mm, "end": v(4855.89, 102.85) * mm});
            skArc(sketch, "E7.49.0.9", {"start": v(4886.39, 99.85) * mm, "mid": v(4883.56, 98.67) * mm, "end": v(4882.39, 95.85) * mm});
            skArc(sketch, "E7.49.0.10", {"start": v(4879.39, 95.85) * mm, "mid": v(4878.22, 98.67) * mm, "end": v(4875.39, 99.85) * mm});
            skArc(sketch, "E7.49.0.11", {"start": v(4875.39, -0.15) * mm, "mid": v(4878.22, 1.02) * mm, "end": v(4879.39, 3.85) * mm});
            skArc(sketch, "E7.49.0.12", {"start": v(4882.39, 3.85) * mm, "mid": v(4883.56, 1.02) * mm, "end": v(4886.39, -0.15) * mm});
            skPoint(sketch, "E7.50.0.0", {"position": v(4979.39, 99.85) * mm});
            skLineSegment(sketch, "E7.50.0.1", {"start": v(4955.89, 99.85) * mm, "end": v(4975.39, 99.85) * mm});
            skPoint(sketch, "E7.50.0.2", {"position": v(4982.39, 96.07) * mm});
            skLineSegment(sketch, "E7.50.0.3", {"start": v(4979.39, 95.85) * mm, "end": v(4979.39, 3.85) * mm});
            skLineSegment(sketch, "E7.50.0.4", {"start": v(4982.39, 95.85) * mm, "end": v(4982.39, 3.85) * mm});
            skLineSegment(sketch, "E7.50.0.5", {"start": v(4955.89, 102.85) * mm, "end": v(5005.89, 102.85) * mm});
            skLineSegment(sketch, "E7.50.0.6", {"start": v(4986.39, 99.85) * mm, "end": v(5005.89, 99.85) * mm});
            skLineSegment(sketch, "E7.50.0.7", {"start": v(5005.89, 99.85) * mm, "end": v(5005.89, 102.85) * mm});
            skLineSegment(sketch, "E7.50.0.8", {"start": v(4955.89, 99.85) * mm, "end": v(4955.89, 102.85) * mm});
            skArc(sketch, "E7.50.0.9", {"start": v(4986.39, 99.85) * mm, "mid": v(4983.56, 98.67) * mm, "end": v(4982.39, 95.85) * mm});
            skArc(sketch, "E7.50.0.10", {"start": v(4979.39, 95.85) * mm, "mid": v(4978.22, 98.67) * mm, "end": v(4975.39, 99.85) * mm});
            skArc(sketch, "E7.50.0.11", {"start": v(4975.39, -0.15) * mm, "mid": v(4978.22, 1.02) * mm, "end": v(4979.39, 3.85) * mm});
            skArc(sketch, "E7.50.0.12", {"start": v(4982.39, 3.85) * mm, "mid": v(4983.56, 1.02) * mm, "end": v(4986.39, -0.15) * mm});
            skPoint(sketch, "E7.51.0.0", {"position": v(5079.39, 99.85) * mm});
            skLineSegment(sketch, "E7.51.0.1", {"start": v(5055.89, 99.85) * mm, "end": v(5075.39, 99.85) * mm});
            skPoint(sketch, "E7.51.0.2", {"position": v(5082.39, 96.07) * mm});
            skLineSegment(sketch, "E7.51.0.3", {"start": v(5079.39, 95.85) * mm, "end": v(5079.39, 3.85) * mm});
            skLineSegment(sketch, "E7.51.0.4", {"start": v(5082.39, 95.85) * mm, "end": v(5082.39, 3.85) * mm});
            skLineSegment(sketch, "E7.51.0.5", {"start": v(5055.89, 102.85) * mm, "end": v(5105.89, 102.85) * mm});
            skLineSegment(sketch, "E7.51.0.6", {"start": v(5086.39, 99.85) * mm, "end": v(5105.89, 99.85) * mm});
            skLineSegment(sketch, "E7.51.0.7", {"start": v(5105.89, 99.85) * mm, "end": v(5105.89, 102.85) * mm});
            skLineSegment(sketch, "E7.51.0.8", {"start": v(5055.89, 99.85) * mm, "end": v(5055.89, 102.85) * mm});
            skArc(sketch, "E7.51.0.9", {"start": v(5086.39, 99.85) * mm, "mid": v(5083.56, 98.67) * mm, "end": v(5082.39, 95.85) * mm});
            skArc(sketch, "E7.51.0.10", {"start": v(5079.39, 95.85) * mm, "mid": v(5078.22, 98.67) * mm, "end": v(5075.39, 99.85) * mm});
            skArc(sketch, "E7.51.0.11", {"start": v(5075.39, -0.15) * mm, "mid": v(5078.22, 1.02) * mm, "end": v(5079.39, 3.85) * mm});
            skArc(sketch, "E7.51.0.12", {"start": v(5082.39, 3.85) * mm, "mid": v(5083.56, 1.02) * mm, "end": v(5086.39, -0.15) * mm});
            skPoint(sketch, "E7.52.0.0", {"position": v(5179.39, 99.85) * mm});
            skLineSegment(sketch, "E7.52.0.1", {"start": v(5155.89, 99.85) * mm, "end": v(5175.39, 99.85) * mm});
            skPoint(sketch, "E7.52.0.2", {"position": v(5182.39, 96.07) * mm});
            skLineSegment(sketch, "E7.52.0.3", {"start": v(5179.39, 95.85) * mm, "end": v(5179.39, 3.85) * mm});
            skLineSegment(sketch, "E7.52.0.4", {"start": v(5182.39, 95.85) * mm, "end": v(5182.39, 3.85) * mm});
            skLineSegment(sketch, "E7.52.0.5", {"start": v(5155.89, 102.85) * mm, "end": v(5205.89, 102.85) * mm});
            skLineSegment(sketch, "E7.52.0.6", {"start": v(5186.39, 99.85) * mm, "end": v(5205.89, 99.85) * mm});
            skLineSegment(sketch, "E7.52.0.7", {"start": v(5205.89, 99.85) * mm, "end": v(5205.89, 102.85) * mm});
            skLineSegment(sketch, "E7.52.0.8", {"start": v(5155.89, 99.85) * mm, "end": v(5155.89, 102.85) * mm});
            skArc(sketch, "E7.52.0.9", {"start": v(5186.39, 99.85) * mm, "mid": v(5183.56, 98.67) * mm, "end": v(5182.39, 95.85) * mm});
            skArc(sketch, "E7.52.0.10", {"start": v(5179.39, 95.85) * mm, "mid": v(5178.22, 98.67) * mm, "end": v(5175.39, 99.85) * mm});
            skArc(sketch, "E7.52.0.11", {"start": v(5175.39, -0.15) * mm, "mid": v(5178.22, 1.02) * mm, "end": v(5179.39, 3.85) * mm});
            skArc(sketch, "E7.52.0.12", {"start": v(5182.39, 3.85) * mm, "mid": v(5183.56, 1.02) * mm, "end": v(5186.39, -0.15) * mm});
            skPoint(sketch, "E7.53.0.0", {"position": v(5279.39, 99.85) * mm});
            skLineSegment(sketch, "E7.53.0.1", {"start": v(5255.89, 99.85) * mm, "end": v(5275.39, 99.85) * mm});
            skPoint(sketch, "E7.53.0.2", {"position": v(5282.39, 96.07) * mm});
            skLineSegment(sketch, "E7.53.0.3", {"start": v(5279.39, 95.85) * mm, "end": v(5279.39, 3.85) * mm});
            skLineSegment(sketch, "E7.53.0.4", {"start": v(5282.39, 95.85) * mm, "end": v(5282.39, 3.85) * mm});
            skLineSegment(sketch, "E7.53.0.5", {"start": v(5255.89, 102.85) * mm, "end": v(5305.89, 102.85) * mm});
            skLineSegment(sketch, "E7.53.0.6", {"start": v(5286.39, 99.85) * mm, "end": v(5305.89, 99.85) * mm});
            skLineSegment(sketch, "E7.53.0.7", {"start": v(5305.89, 99.85) * mm, "end": v(5305.89, 102.85) * mm});
            skLineSegment(sketch, "E7.53.0.8", {"start": v(5255.89, 99.85) * mm, "end": v(5255.89, 102.85) * mm});
            skArc(sketch, "E7.53.0.9", {"start": v(5286.39, 99.85) * mm, "mid": v(5283.56, 98.67) * mm, "end": v(5282.39, 95.85) * mm});
            skArc(sketch, "E7.53.0.10", {"start": v(5279.39, 95.85) * mm, "mid": v(5278.22, 98.67) * mm, "end": v(5275.39, 99.85) * mm});
            skArc(sketch, "E7.53.0.11", {"start": v(5275.39, -0.15) * mm, "mid": v(5278.22, 1.02) * mm, "end": v(5279.39, 3.85) * mm});
            skArc(sketch, "E7.53.0.12", {"start": v(5282.39, 3.85) * mm, "mid": v(5283.56, 1.02) * mm, "end": v(5286.39, -0.15) * mm});
            skPoint(sketch, "E7.54.0.0", {"position": v(5379.39, 99.85) * mm});
            skLineSegment(sketch, "E7.54.0.1", {"start": v(5355.89, 99.85) * mm, "end": v(5375.39, 99.85) * mm});
            skPoint(sketch, "E7.54.0.2", {"position": v(5382.39, 96.07) * mm});
            skLineSegment(sketch, "E7.54.0.3", {"start": v(5379.39, 95.85) * mm, "end": v(5379.39, 3.85) * mm});
            skLineSegment(sketch, "E7.54.0.4", {"start": v(5382.39, 95.85) * mm, "end": v(5382.39, 3.85) * mm});
            skLineSegment(sketch, "E7.54.0.5", {"start": v(5355.89, 102.85) * mm, "end": v(5405.89, 102.85) * mm});
            skLineSegment(sketch, "E7.54.0.6", {"start": v(5386.39, 99.85) * mm, "end": v(5405.89, 99.85) * mm});
            skLineSegment(sketch, "E7.54.0.7", {"start": v(5405.89, 99.85) * mm, "end": v(5405.89, 102.85) * mm});
            skLineSegment(sketch, "E7.54.0.8", {"start": v(5355.89, 99.85) * mm, "end": v(5355.89, 102.85) * mm});
            skArc(sketch, "E7.54.0.9", {"start": v(5386.39, 99.85) * mm, "mid": v(5383.56, 98.67) * mm, "end": v(5382.39, 95.85) * mm});
            skArc(sketch, "E7.54.0.10", {"start": v(5379.39, 95.85) * mm, "mid": v(5378.22, 98.67) * mm, "end": v(5375.39, 99.85) * mm});
            skArc(sketch, "E7.54.0.11", {"start": v(5375.39, -0.15) * mm, "mid": v(5378.22, 1.02) * mm, "end": v(5379.39, 3.85) * mm});
            skArc(sketch, "E7.54.0.12", {"start": v(5382.39, 3.85) * mm, "mid": v(5383.56, 1.02) * mm, "end": v(5386.39, -0.15) * mm});
            skPoint(sketch, "E7.55.0.0", {"position": v(5479.39, 99.85) * mm});
            skLineSegment(sketch, "E7.55.0.1", {"start": v(5455.89, 99.85) * mm, "end": v(5475.39, 99.85) * mm});
            skPoint(sketch, "E7.55.0.2", {"position": v(5482.39, 96.07) * mm});
            skLineSegment(sketch, "E7.55.0.3", {"start": v(5479.39, 95.85) * mm, "end": v(5479.39, 3.85) * mm});
            skLineSegment(sketch, "E7.55.0.4", {"start": v(5482.39, 95.85) * mm, "end": v(5482.39, 3.85) * mm});
            skLineSegment(sketch, "E7.55.0.5", {"start": v(5455.89, 102.85) * mm, "end": v(5505.89, 102.85) * mm});
            skLineSegment(sketch, "E7.55.0.6", {"start": v(5486.39, 99.85) * mm, "end": v(5505.89, 99.85) * mm});
            skLineSegment(sketch, "E7.55.0.7", {"start": v(5505.89, 99.85) * mm, "end": v(5505.89, 102.85) * mm});
            skLineSegment(sketch, "E7.55.0.8", {"start": v(5455.89, 99.85) * mm, "end": v(5455.89, 102.85) * mm});
            skArc(sketch, "E7.55.0.9", {"start": v(5486.39, 99.85) * mm, "mid": v(5483.56, 98.67) * mm, "end": v(5482.39, 95.85) * mm});
            skArc(sketch, "E7.55.0.10", {"start": v(5479.39, 95.85) * mm, "mid": v(5478.22, 98.67) * mm, "end": v(5475.39, 99.85) * mm});
            skArc(sketch, "E7.55.0.11", {"start": v(5475.39, -0.15) * mm, "mid": v(5478.22, 1.02) * mm, "end": v(5479.39, 3.85) * mm});
            skArc(sketch, "E7.55.0.12", {"start": v(5482.39, 3.85) * mm, "mid": v(5483.56, 1.02) * mm, "end": v(5486.39, -0.15) * mm});
            skPoint(sketch, "E7.56.0.0", {"position": v(5579.39, 99.85) * mm});
            skLineSegment(sketch, "E7.56.0.1", {"start": v(5555.89, 99.85) * mm, "end": v(5575.39, 99.85) * mm});
            skPoint(sketch, "E7.56.0.2", {"position": v(5582.39, 96.07) * mm});
            skLineSegment(sketch, "E7.56.0.3", {"start": v(5579.39, 95.85) * mm, "end": v(5579.39, 3.85) * mm});
            skLineSegment(sketch, "E7.56.0.4", {"start": v(5582.39, 95.85) * mm, "end": v(5582.39, 3.85) * mm});
            skLineSegment(sketch, "E7.56.0.5", {"start": v(5555.89, 102.85) * mm, "end": v(5605.89, 102.85) * mm});
            skLineSegment(sketch, "E7.56.0.6", {"start": v(5586.39, 99.85) * mm, "end": v(5605.89, 99.85) * mm});
            skLineSegment(sketch, "E7.56.0.7", {"start": v(5605.89, 99.85) * mm, "end": v(5605.89, 102.85) * mm});
            skLineSegment(sketch, "E7.56.0.8", {"start": v(5555.89, 99.85) * mm, "end": v(5555.89, 102.85) * mm});
            skArc(sketch, "E7.56.0.9", {"start": v(5586.39, 99.85) * mm, "mid": v(5583.56, 98.67) * mm, "end": v(5582.39, 95.85) * mm});
            skArc(sketch, "E7.56.0.10", {"start": v(5579.39, 95.85) * mm, "mid": v(5578.22, 98.67) * mm, "end": v(5575.39, 99.85) * mm});
            skArc(sketch, "E7.56.0.11", {"start": v(5575.39, -0.15) * mm, "mid": v(5578.22, 1.02) * mm, "end": v(5579.39, 3.85) * mm});
            skArc(sketch, "E7.56.0.12", {"start": v(5582.39, 3.85) * mm, "mid": v(5583.56, 1.02) * mm, "end": v(5586.39, -0.15) * mm});
            skPoint(sketch, "E7.57.0.0", {"position": v(5679.39, 99.85) * mm});
            skLineSegment(sketch, "E7.57.0.1", {"start": v(5655.89, 99.85) * mm, "end": v(5675.39, 99.85) * mm});
            skPoint(sketch, "E7.57.0.2", {"position": v(5682.39, 96.07) * mm});
            skLineSegment(sketch, "E7.57.0.3", {"start": v(5679.39, 95.85) * mm, "end": v(5679.39, 3.85) * mm});
            skLineSegment(sketch, "E7.57.0.4", {"start": v(5682.39, 95.85) * mm, "end": v(5682.39, 3.85) * mm});
            skLineSegment(sketch, "E7.57.0.5", {"start": v(5655.89, 102.85) * mm, "end": v(5705.89, 102.85) * mm});
            skLineSegment(sketch, "E7.57.0.6", {"start": v(5686.39, 99.85) * mm, "end": v(5705.89, 99.85) * mm});
            skLineSegment(sketch, "E7.57.0.7", {"start": v(5705.89, 99.85) * mm, "end": v(5705.89, 102.85) * mm});
            skLineSegment(sketch, "E7.57.0.8", {"start": v(5655.89, 99.85) * mm, "end": v(5655.89, 102.85) * mm});
            skArc(sketch, "E7.57.0.9", {"start": v(5686.39, 99.85) * mm, "mid": v(5683.56, 98.67) * mm, "end": v(5682.39, 95.85) * mm});
            skArc(sketch, "E7.57.0.10", {"start": v(5679.39, 95.85) * mm, "mid": v(5678.22, 98.67) * mm, "end": v(5675.39, 99.85) * mm});
            skArc(sketch, "E7.57.0.11", {"start": v(5675.39, -0.15) * mm, "mid": v(5678.22, 1.02) * mm, "end": v(5679.39, 3.85) * mm});
            skArc(sketch, "E7.57.0.12", {"start": v(5682.39, 3.85) * mm, "mid": v(5683.56, 1.02) * mm, "end": v(5686.39, -0.15) * mm});
            skPoint(sketch, "E7.58.0.0", {"position": v(5779.39, 99.85) * mm});
            skLineSegment(sketch, "E7.58.0.1", {"start": v(5755.89, 99.85) * mm, "end": v(5775.39, 99.85) * mm});
            skPoint(sketch, "E7.58.0.2", {"position": v(5782.39, 96.07) * mm});
            skLineSegment(sketch, "E7.58.0.3", {"start": v(5779.39, 95.85) * mm, "end": v(5779.39, 3.85) * mm});
            skLineSegment(sketch, "E7.58.0.4", {"start": v(5782.39, 95.85) * mm, "end": v(5782.39, 3.85) * mm});
            skLineSegment(sketch, "E7.58.0.5", {"start": v(5755.89, 102.85) * mm, "end": v(5805.89, 102.85) * mm});
            skLineSegment(sketch, "E7.58.0.6", {"start": v(5786.39, 99.85) * mm, "end": v(5805.89, 99.85) * mm});
            skLineSegment(sketch, "E7.58.0.7", {"start": v(5805.89, 99.85) * mm, "end": v(5805.89, 102.85) * mm});
            skLineSegment(sketch, "E7.58.0.8", {"start": v(5755.89, 99.85) * mm, "end": v(5755.89, 102.85) * mm});
            skArc(sketch, "E7.58.0.9", {"start": v(5786.39, 99.85) * mm, "mid": v(5783.56, 98.67) * mm, "end": v(5782.39, 95.85) * mm});
            skArc(sketch, "E7.58.0.10", {"start": v(5779.39, 95.85) * mm, "mid": v(5778.22, 98.67) * mm, "end": v(5775.39, 99.85) * mm});
            skArc(sketch, "E7.58.0.11", {"start": v(5775.39, -0.15) * mm, "mid": v(5778.22, 1.02) * mm, "end": v(5779.39, 3.85) * mm});
            skArc(sketch, "E7.58.0.12", {"start": v(5782.39, 3.85) * mm, "mid": v(5783.56, 1.02) * mm, "end": v(5786.39, -0.15) * mm});
            skPoint(sketch, "E7.59.0.0", {"position": v(5879.39, 99.85) * mm});
            skLineSegment(sketch, "E7.59.0.1", {"start": v(5855.89, 99.85) * mm, "end": v(5875.39, 99.85) * mm});
            skPoint(sketch, "E7.59.0.2", {"position": v(5882.39, 96.07) * mm});
            skLineSegment(sketch, "E7.59.0.3", {"start": v(5879.39, 95.85) * mm, "end": v(5879.39, 3.85) * mm});
            skLineSegment(sketch, "E7.59.0.4", {"start": v(5882.39, 95.85) * mm, "end": v(5882.39, 3.85) * mm});
            skLineSegment(sketch, "E7.59.0.5", {"start": v(5855.89, 102.85) * mm, "end": v(5905.89, 102.85) * mm});
            skLineSegment(sketch, "E7.59.0.6", {"start": v(5886.39, 99.85) * mm, "end": v(5905.89, 99.85) * mm});
            skLineSegment(sketch, "E7.59.0.7", {"start": v(5905.89, 99.85) * mm, "end": v(5905.89, 102.85) * mm});
            skLineSegment(sketch, "E7.59.0.8", {"start": v(5855.89, 99.85) * mm, "end": v(5855.89, 102.85) * mm});
            skArc(sketch, "E7.59.0.9", {"start": v(5886.39, 99.85) * mm, "mid": v(5883.56, 98.67) * mm, "end": v(5882.39, 95.85) * mm});
            skArc(sketch, "E7.59.0.10", {"start": v(5879.39, 95.85) * mm, "mid": v(5878.22, 98.67) * mm, "end": v(5875.39, 99.85) * mm});
            skArc(sketch, "E7.59.0.11", {"start": v(5875.39, -0.15) * mm, "mid": v(5878.22, 1.02) * mm, "end": v(5879.39, 3.85) * mm});
            skArc(sketch, "E7.59.0.12", {"start": v(5882.39, 3.85) * mm, "mid": v(5883.56, 1.02) * mm, "end": v(5886.39, -0.15) * mm});
            skLineSegment(sketch, "E7.direction1", {"start": v(-24.61, -0.15) * mm, "end": v(75.39, -0.15) * mm, "construction": true});
            skLineSegment(sketch, "E8.bottom", {"start": v(5939.39, -0.15) * mm, "end": v(5936.39, -0.15) * mm});
            skLineSegment(sketch, "E9.bottom", {"start": v(-60.61, -0.15) * mm, "end": v(-57.61, -0.15) * mm});
            skSolve(sketch);
        }
        {
            var Q0;
            Q0 = qSketchRegion(id + "F0", true);
            extrude(context, id + "F1", {"entities" : qUnion([Q0]), "depth" : 2500 * mm});
        }
        {
            var Q0;
            Q0=makeQuery(id+"F1.opExtrude","SWEPT_FACE",FACE,{"disambiguationData":[OSD([sQuery(id+"F0.wireOp",EDGE,"E0.left")])]});
            var sketch = newSketch(context, id + "F2", { "sketchPlane" : qUnion([Q0])});
            skLineSegment(sketch, "E10.bottom", {"start": v(40, 102.85) * mm, "end": v(43, 102.85) * mm});
            skLineSegment(sketch, "E10.top", {"start": v(47, 202.85) * mm, "end": v(66.5, 202.85) * mm});
            skLineSegment(sketch, "E10.left", {"start": v(40, 106.85) * mm, "end": v(40, 198.85) * mm});
            skLineSegment(sketch, "E10.right", {"start": v(43, 106.85) * mm, "end": v(43, 198.85) * mm});
            skLineSegment(sketch, "E11.bottom", {"start": v(16.5, 202.85) * mm, "end": v(36, 202.85) * mm});
            skLineSegment(sketch, "E11.top", {"start": v(16.5, 205.85) * mm, "end": v(66.5, 205.85) * mm});
            skLineSegment(sketch, "E11.left", {"start": v(16.5, 202.85) * mm, "end": v(16.5, 205.85) * mm});
            skLineSegment(sketch, "E11.right", {"start": v(66.5, 202.85) * mm, "end": v(66.5, 205.85) * mm});
            skArc(sketch, "E12.filletArc", {"start": v(40, 198.85) * mm, "mid": v(38.83, 201.67) * mm, "end": v(36, 202.85) * mm});
            skPoint(sketch, "E13.visualSharp", {"position": v(43, 202.85) * mm});
            skArc(sketch, "E13.filletArc", {"start": v(47, 202.85) * mm, "mid": v(44.17, 201.67) * mm, "end": v(43, 198.85) * mm});
            skLineSegment(sketch, "E14", {"start": v(36, 102.85) * mm, "end": v(0, 102.85) * mm});
            skLineSegment(sketch, "E15", {"start": v(47, 102.85) * mm, "end": v(2500, 102.85) * mm});
            skPoint(sketch, "E16.visualSharp", {"position": v(40, 102.85) * mm});
            skArc(sketch, "E16.filletArc", {"start": v(36, 102.85) * mm, "mid": v(38.83, 104.02) * mm, "end": v(40, 106.85) * mm});
            skPoint(sketch, "E17.visualSharp", {"position": v(43, 102.85) * mm});
            skArc(sketch, "E17.filletArc", {"start": v(43, 106.85) * mm, "mid": v(44.17, 104.02) * mm, "end": v(47, 102.85) * mm});
            skLineSegment(sketch, "E18.1.0.0", {"start": v(116.5, 202.85) * mm, "end": v(136, 202.85) * mm});
            skLineSegment(sketch, "E18.1.0.1", {"start": v(143, 106.85) * mm, "end": v(143, 198.85) * mm});
            skLineSegment(sketch, "E18.1.0.2", {"start": v(140, 106.85) * mm, "end": v(140, 198.85) * mm});
            skPoint(sketch, "E18.1.0.3", {"position": v(143, 202.85) * mm});
            skLineSegment(sketch, "E18.1.0.4", {"start": v(116.5, 202.85) * mm, "end": v(116.5, 205.85) * mm});
            skArc(sketch, "E18.1.0.5", {"start": v(140, 198.85) * mm, "mid": v(138.83, 201.67) * mm, "end": v(136, 202.85) * mm});
            skArc(sketch, "E18.1.0.6", {"start": v(147, 202.85) * mm, "mid": v(144.17, 201.67) * mm, "end": v(143, 198.85) * mm});
            skLineSegment(sketch, "E18.1.0.7", {"start": v(166.5, 202.85) * mm, "end": v(166.5, 205.85) * mm});
            skLineSegment(sketch, "E18.1.0.8", {"start": v(116.5, 205.85) * mm, "end": v(166.5, 205.85) * mm});
            skLineSegment(sketch, "E18.1.0.9", {"start": v(147, 202.85) * mm, "end": v(166.5, 202.85) * mm});
            skArc(sketch, "E18.1.0.10", {"start": v(136, 102.85) * mm, "mid": v(138.83, 104.02) * mm, "end": v(140, 106.85) * mm});
            skArc(sketch, "E18.1.0.11", {"start": v(143, 106.85) * mm, "mid": v(144.17, 104.02) * mm, "end": v(147, 102.85) * mm});
            skLineSegment(sketch, "E18.2.0.0", {"start": v(216.5, 202.85) * mm, "end": v(236, 202.85) * mm});
            skLineSegment(sketch, "E18.2.0.1", {"start": v(243, 106.85) * mm, "end": v(243, 198.85) * mm});
            skLineSegment(sketch, "E18.2.0.2", {"start": v(240, 106.85) * mm, "end": v(240, 198.85) * mm});
            skPoint(sketch, "E18.2.0.3", {"position": v(243, 202.85) * mm});
            skLineSegment(sketch, "E18.2.0.4", {"start": v(216.5, 202.85) * mm, "end": v(216.5, 205.85) * mm});
            skArc(sketch, "E18.2.0.5", {"start": v(240, 198.85) * mm, "mid": v(238.83, 201.67) * mm, "end": v(236, 202.85) * mm});
            skArc(sketch, "E18.2.0.6", {"start": v(247, 202.85) * mm, "mid": v(244.17, 201.67) * mm, "end": v(243, 198.85) * mm});
            skLineSegment(sketch, "E18.2.0.7", {"start": v(266.5, 202.85) * mm, "end": v(266.5, 205.85) * mm});
            skLineSegment(sketch, "E18.2.0.8", {"start": v(216.5, 205.85) * mm, "end": v(266.5, 205.85) * mm});
            skLineSegment(sketch, "E18.2.0.9", {"start": v(247, 202.85) * mm, "end": v(266.5, 202.85) * mm});
            skArc(sketch, "E18.2.0.10", {"start": v(236, 102.85) * mm, "mid": v(238.83, 104.02) * mm, "end": v(240, 106.85) * mm});
            skArc(sketch, "E18.2.0.11", {"start": v(243, 106.85) * mm, "mid": v(244.17, 104.02) * mm, "end": v(247, 102.85) * mm});
            skLineSegment(sketch, "E18.3.0.0", {"start": v(316.5, 202.85) * mm, "end": v(336, 202.85) * mm});
            skLineSegment(sketch, "E18.3.0.1", {"start": v(343, 106.85) * mm, "end": v(343, 198.85) * mm});
            skLineSegment(sketch, "E18.3.0.2", {"start": v(340, 106.85) * mm, "end": v(340, 198.85) * mm});
            skPoint(sketch, "E18.3.0.3", {"position": v(343, 202.85) * mm});
            skLineSegment(sketch, "E18.3.0.4", {"start": v(316.5, 202.85) * mm, "end": v(316.5, 205.85) * mm});
            skArc(sketch, "E18.3.0.5", {"start": v(340, 198.85) * mm, "mid": v(338.83, 201.67) * mm, "end": v(336, 202.85) * mm});
            skArc(sketch, "E18.3.0.6", {"start": v(347, 202.85) * mm, "mid": v(344.17, 201.67) * mm, "end": v(343, 198.85) * mm});
            skLineSegment(sketch, "E18.3.0.7", {"start": v(366.5, 202.85) * mm, "end": v(366.5, 205.85) * mm});
            skLineSegment(sketch, "E18.3.0.8", {"start": v(316.5, 205.85) * mm, "end": v(366.5, 205.85) * mm});
            skLineSegment(sketch, "E18.3.0.9", {"start": v(347, 202.85) * mm, "end": v(366.5, 202.85) * mm});
            skArc(sketch, "E18.3.0.10", {"start": v(336, 102.85) * mm, "mid": v(338.83, 104.02) * mm, "end": v(340, 106.85) * mm});
            skArc(sketch, "E18.3.0.11", {"start": v(343, 106.85) * mm, "mid": v(344.17, 104.02) * mm, "end": v(347, 102.85) * mm});
            skLineSegment(sketch, "E18.4.0.0", {"start": v(416.5, 202.85) * mm, "end": v(436, 202.85) * mm});
            skLineSegment(sketch, "E18.4.0.1", {"start": v(443, 106.85) * mm, "end": v(443, 198.85) * mm});
            skLineSegment(sketch, "E18.4.0.2", {"start": v(440, 106.85) * mm, "end": v(440, 198.85) * mm});
            skPoint(sketch, "E18.4.0.3", {"position": v(443, 202.85) * mm});
            skLineSegment(sketch, "E18.4.0.4", {"start": v(416.5, 202.85) * mm, "end": v(416.5, 205.85) * mm});
            skArc(sketch, "E18.4.0.5", {"start": v(440, 198.85) * mm, "mid": v(438.83, 201.67) * mm, "end": v(436, 202.85) * mm});
            skArc(sketch, "E18.4.0.6", {"start": v(447, 202.85) * mm, "mid": v(444.17, 201.67) * mm, "end": v(443, 198.85) * mm});
            skLineSegment(sketch, "E18.4.0.7", {"start": v(466.5, 202.85) * mm, "end": v(466.5, 205.85) * mm});
            skLineSegment(sketch, "E18.4.0.8", {"start": v(416.5, 205.85) * mm, "end": v(466.5, 205.85) * mm});
            skLineSegment(sketch, "E18.4.0.9", {"start": v(447, 202.85) * mm, "end": v(466.5, 202.85) * mm});
            skArc(sketch, "E18.4.0.10", {"start": v(436, 102.85) * mm, "mid": v(438.83, 104.02) * mm, "end": v(440, 106.85) * mm});
            skArc(sketch, "E18.4.0.11", {"start": v(443, 106.85) * mm, "mid": v(444.17, 104.02) * mm, "end": v(447, 102.85) * mm});
            skLineSegment(sketch, "E18.5.0.0", {"start": v(516.5, 202.85) * mm, "end": v(536, 202.85) * mm});
            skLineSegment(sketch, "E18.5.0.1", {"start": v(543, 106.85) * mm, "end": v(543, 198.85) * mm});
            skLineSegment(sketch, "E18.5.0.2", {"start": v(540, 106.85) * mm, "end": v(540, 198.85) * mm});
            skPoint(sketch, "E18.5.0.3", {"position": v(543, 202.85) * mm});
            skLineSegment(sketch, "E18.5.0.4", {"start": v(516.5, 202.85) * mm, "end": v(516.5, 205.85) * mm});
            skArc(sketch, "E18.5.0.5", {"start": v(540, 198.85) * mm, "mid": v(538.83, 201.67) * mm, "end": v(536, 202.85) * mm});
            skArc(sketch, "E18.5.0.6", {"start": v(547, 202.85) * mm, "mid": v(544.17, 201.67) * mm, "end": v(543, 198.85) * mm});
            skLineSegment(sketch, "E18.5.0.7", {"start": v(566.5, 202.85) * mm, "end": v(566.5, 205.85) * mm});
            skLineSegment(sketch, "E18.5.0.8", {"start": v(516.5, 205.85) * mm, "end": v(566.5, 205.85) * mm});
            skLineSegment(sketch, "E18.5.0.9", {"start": v(547, 202.85) * mm, "end": v(566.5, 202.85) * mm});
            skArc(sketch, "E18.5.0.10", {"start": v(536, 102.85) * mm, "mid": v(538.83, 104.02) * mm, "end": v(540, 106.85) * mm});
            skArc(sketch, "E18.5.0.11", {"start": v(543, 106.85) * mm, "mid": v(544.17, 104.02) * mm, "end": v(547, 102.85) * mm});
            skLineSegment(sketch, "E18.6.0.0", {"start": v(616.5, 202.85) * mm, "end": v(636, 202.85) * mm});
            skLineSegment(sketch, "E18.6.0.1", {"start": v(643, 106.85) * mm, "end": v(643, 198.85) * mm});
            skLineSegment(sketch, "E18.6.0.2", {"start": v(640, 106.85) * mm, "end": v(640, 198.85) * mm});
            skPoint(sketch, "E18.6.0.3", {"position": v(643, 202.85) * mm});
            skLineSegment(sketch, "E18.6.0.4", {"start": v(616.5, 202.85) * mm, "end": v(616.5, 205.85) * mm});
            skArc(sketch, "E18.6.0.5", {"start": v(640, 198.85) * mm, "mid": v(638.83, 201.67) * mm, "end": v(636, 202.85) * mm});
            skArc(sketch, "E18.6.0.6", {"start": v(647, 202.85) * mm, "mid": v(644.17, 201.67) * mm, "end": v(643, 198.85) * mm});
            skLineSegment(sketch, "E18.6.0.7", {"start": v(666.5, 202.85) * mm, "end": v(666.5, 205.85) * mm});
            skLineSegment(sketch, "E18.6.0.8", {"start": v(616.5, 205.85) * mm, "end": v(666.5, 205.85) * mm});
            skLineSegment(sketch, "E18.6.0.9", {"start": v(647, 202.85) * mm, "end": v(666.5, 202.85) * mm});
            skArc(sketch, "E18.6.0.10", {"start": v(636, 102.85) * mm, "mid": v(638.83, 104.02) * mm, "end": v(640, 106.85) * mm});
            skArc(sketch, "E18.6.0.11", {"start": v(643, 106.85) * mm, "mid": v(644.17, 104.02) * mm, "end": v(647, 102.85) * mm});
            skLineSegment(sketch, "E18.7.0.0", {"start": v(716.5, 202.85) * mm, "end": v(736, 202.85) * mm});
            skLineSegment(sketch, "E18.7.0.1", {"start": v(743, 106.85) * mm, "end": v(743, 198.85) * mm});
            skLineSegment(sketch, "E18.7.0.2", {"start": v(740, 106.85) * mm, "end": v(740, 198.85) * mm});
            skPoint(sketch, "E18.7.0.3", {"position": v(743, 202.85) * mm});
            skLineSegment(sketch, "E18.7.0.4", {"start": v(716.5, 202.85) * mm, "end": v(716.5, 205.85) * mm});
            skArc(sketch, "E18.7.0.5", {"start": v(740, 198.85) * mm, "mid": v(738.83, 201.67) * mm, "end": v(736, 202.85) * mm});
            skArc(sketch, "E18.7.0.6", {"start": v(747, 202.85) * mm, "mid": v(744.17, 201.67) * mm, "end": v(743, 198.85) * mm});
            skLineSegment(sketch, "E18.7.0.7", {"start": v(766.5, 202.85) * mm, "end": v(766.5, 205.85) * mm});
            skLineSegment(sketch, "E18.7.0.8", {"start": v(716.5, 205.85) * mm, "end": v(766.5, 205.85) * mm});
            skLineSegment(sketch, "E18.7.0.9", {"start": v(747, 202.85) * mm, "end": v(766.5, 202.85) * mm});
            skArc(sketch, "E18.7.0.10", {"start": v(736, 102.85) * mm, "mid": v(738.83, 104.02) * mm, "end": v(740, 106.85) * mm});
            skArc(sketch, "E18.7.0.11", {"start": v(743, 106.85) * mm, "mid": v(744.17, 104.02) * mm, "end": v(747, 102.85) * mm});
            skLineSegment(sketch, "E18.8.0.0", {"start": v(816.5, 202.85) * mm, "end": v(836, 202.85) * mm});
            skLineSegment(sketch, "E18.8.0.1", {"start": v(843, 106.85) * mm, "end": v(843, 198.85) * mm});
            skLineSegment(sketch, "E18.8.0.2", {"start": v(840, 106.85) * mm, "end": v(840, 198.85) * mm});
            skPoint(sketch, "E18.8.0.3", {"position": v(843, 202.85) * mm});
            skLineSegment(sketch, "E18.8.0.4", {"start": v(816.5, 202.85) * mm, "end": v(816.5, 205.85) * mm});
            skArc(sketch, "E18.8.0.5", {"start": v(840, 198.85) * mm, "mid": v(838.83, 201.67) * mm, "end": v(836, 202.85) * mm});
            skArc(sketch, "E18.8.0.6", {"start": v(847, 202.85) * mm, "mid": v(844.17, 201.67) * mm, "end": v(843, 198.85) * mm});
            skLineSegment(sketch, "E18.8.0.7", {"start": v(866.5, 202.85) * mm, "end": v(866.5, 205.85) * mm});
            skLineSegment(sketch, "E18.8.0.8", {"start": v(816.5, 205.85) * mm, "end": v(866.5, 205.85) * mm});
            skLineSegment(sketch, "E18.8.0.9", {"start": v(847, 202.85) * mm, "end": v(866.5, 202.85) * mm});
            skArc(sketch, "E18.8.0.10", {"start": v(836, 102.85) * mm, "mid": v(838.83, 104.02) * mm, "end": v(840, 106.85) * mm});
            skArc(sketch, "E18.8.0.11", {"start": v(843, 106.85) * mm, "mid": v(844.17, 104.02) * mm, "end": v(847, 102.85) * mm});
            skLineSegment(sketch, "E18.9.0.0", {"start": v(916.5, 202.85) * mm, "end": v(936, 202.85) * mm});
            skLineSegment(sketch, "E18.9.0.1", {"start": v(943, 106.85) * mm, "end": v(943, 198.85) * mm});
            skLineSegment(sketch, "E18.9.0.2", {"start": v(940, 106.85) * mm, "end": v(940, 198.85) * mm});
            skPoint(sketch, "E18.9.0.3", {"position": v(943, 202.85) * mm});
            skLineSegment(sketch, "E18.9.0.4", {"start": v(916.5, 202.85) * mm, "end": v(916.5, 205.85) * mm});
            skArc(sketch, "E18.9.0.5", {"start": v(940, 198.85) * mm, "mid": v(938.83, 201.67) * mm, "end": v(936, 202.85) * mm});
            skArc(sketch, "E18.9.0.6", {"start": v(947, 202.85) * mm, "mid": v(944.17, 201.67) * mm, "end": v(943, 198.85) * mm});
            skLineSegment(sketch, "E18.9.0.7", {"start": v(966.5, 202.85) * mm, "end": v(966.5, 205.85) * mm});
            skLineSegment(sketch, "E18.9.0.8", {"start": v(916.5, 205.85) * mm, "end": v(966.5, 205.85) * mm});
            skLineSegment(sketch, "E18.9.0.9", {"start": v(947, 202.85) * mm, "end": v(966.5, 202.85) * mm});
            skArc(sketch, "E18.9.0.10", {"start": v(936, 102.85) * mm, "mid": v(938.83, 104.02) * mm, "end": v(940, 106.85) * mm});
            skArc(sketch, "E18.9.0.11", {"start": v(943, 106.85) * mm, "mid": v(944.17, 104.02) * mm, "end": v(947, 102.85) * mm});
            skLineSegment(sketch, "E18.10.0.0", {"start": v(1016.5, 202.85) * mm, "end": v(1036, 202.85) * mm});
            skLineSegment(sketch, "E18.10.0.1", {"start": v(1043, 106.85) * mm, "end": v(1043, 198.85) * mm});
            skLineSegment(sketch, "E18.10.0.2", {"start": v(1040, 106.85) * mm, "end": v(1040, 198.85) * mm});
            skPoint(sketch, "E18.10.0.3", {"position": v(1043, 202.85) * mm});
            skLineSegment(sketch, "E18.10.0.4", {"start": v(1016.5, 202.85) * mm, "end": v(1016.5, 205.85) * mm});
            skArc(sketch, "E18.10.0.5", {"start": v(1040, 198.85) * mm, "mid": v(1038.83, 201.67) * mm, "end": v(1036, 202.85) * mm});
            skArc(sketch, "E18.10.0.6", {"start": v(1047, 202.85) * mm, "mid": v(1044.17, 201.67) * mm, "end": v(1043, 198.85) * mm});
            skLineSegment(sketch, "E18.10.0.7", {"start": v(1066.5, 202.85) * mm, "end": v(1066.5, 205.85) * mm});
            skLineSegment(sketch, "E18.10.0.8", {"start": v(1016.5, 205.85) * mm, "end": v(1066.5, 205.85) * mm});
            skLineSegment(sketch, "E18.10.0.9", {"start": v(1047, 202.85) * mm, "end": v(1066.5, 202.85) * mm});
            skArc(sketch, "E18.10.0.10", {"start": v(1036, 102.85) * mm, "mid": v(1038.83, 104.02) * mm, "end": v(1040, 106.85) * mm});
            skArc(sketch, "E18.10.0.11", {"start": v(1043, 106.85) * mm, "mid": v(1044.17, 104.02) * mm, "end": v(1047, 102.85) * mm});
            skLineSegment(sketch, "E18.11.0.0", {"start": v(1116.5, 202.85) * mm, "end": v(1136, 202.85) * mm});
            skLineSegment(sketch, "E18.11.0.1", {"start": v(1143, 106.85) * mm, "end": v(1143, 198.85) * mm});
            skLineSegment(sketch, "E18.11.0.2", {"start": v(1140, 106.85) * mm, "end": v(1140, 198.85) * mm});
            skPoint(sketch, "E18.11.0.3", {"position": v(1143, 202.85) * mm});
            skLineSegment(sketch, "E18.11.0.4", {"start": v(1116.5, 202.85) * mm, "end": v(1116.5, 205.85) * mm});
            skArc(sketch, "E18.11.0.5", {"start": v(1140, 198.85) * mm, "mid": v(1138.83, 201.67) * mm, "end": v(1136, 202.85) * mm});
            skArc(sketch, "E18.11.0.6", {"start": v(1147, 202.85) * mm, "mid": v(1144.17, 201.67) * mm, "end": v(1143, 198.85) * mm});
            skLineSegment(sketch, "E18.11.0.7", {"start": v(1166.5, 202.85) * mm, "end": v(1166.5, 205.85) * mm});
            skLineSegment(sketch, "E18.11.0.8", {"start": v(1116.5, 205.85) * mm, "end": v(1166.5, 205.85) * mm});
            skLineSegment(sketch, "E18.11.0.9", {"start": v(1147, 202.85) * mm, "end": v(1166.5, 202.85) * mm});
            skArc(sketch, "E18.11.0.10", {"start": v(1136, 102.85) * mm, "mid": v(1138.83, 104.02) * mm, "end": v(1140, 106.85) * mm});
            skArc(sketch, "E18.11.0.11", {"start": v(1143, 106.85) * mm, "mid": v(1144.17, 104.02) * mm, "end": v(1147, 102.85) * mm});
            skLineSegment(sketch, "E18.12.0.0", {"start": v(1216.5, 202.85) * mm, "end": v(1236, 202.85) * mm});
            skLineSegment(sketch, "E18.12.0.1", {"start": v(1243, 106.85) * mm, "end": v(1243, 198.85) * mm});
            skLineSegment(sketch, "E18.12.0.2", {"start": v(1240, 106.85) * mm, "end": v(1240, 198.85) * mm});
            skPoint(sketch, "E18.12.0.3", {"position": v(1243, 202.85) * mm});
            skLineSegment(sketch, "E18.12.0.4", {"start": v(1216.5, 202.85) * mm, "end": v(1216.5, 205.85) * mm});
            skArc(sketch, "E18.12.0.5", {"start": v(1240, 198.85) * mm, "mid": v(1238.83, 201.67) * mm, "end": v(1236, 202.85) * mm});
            skArc(sketch, "E18.12.0.6", {"start": v(1247, 202.85) * mm, "mid": v(1244.17, 201.67) * mm, "end": v(1243, 198.85) * mm});
            skLineSegment(sketch, "E18.12.0.7", {"start": v(1266.5, 202.85) * mm, "end": v(1266.5, 205.85) * mm});
            skLineSegment(sketch, "E18.12.0.8", {"start": v(1216.5, 205.85) * mm, "end": v(1266.5, 205.85) * mm});
            skLineSegment(sketch, "E18.12.0.9", {"start": v(1247, 202.85) * mm, "end": v(1266.5, 202.85) * mm});
            skArc(sketch, "E18.12.0.10", {"start": v(1236, 102.85) * mm, "mid": v(1238.83, 104.02) * mm, "end": v(1240, 106.85) * mm});
            skArc(sketch, "E18.12.0.11", {"start": v(1243, 106.85) * mm, "mid": v(1244.17, 104.02) * mm, "end": v(1247, 102.85) * mm});
            skLineSegment(sketch, "E18.13.0.0", {"start": v(1316.5, 202.85) * mm, "end": v(1336, 202.85) * mm});
            skLineSegment(sketch, "E18.13.0.1", {"start": v(1343, 106.85) * mm, "end": v(1343, 198.85) * mm});
            skLineSegment(sketch, "E18.13.0.2", {"start": v(1340, 106.85) * mm, "end": v(1340, 198.85) * mm});
            skPoint(sketch, "E18.13.0.3", {"position": v(1343, 202.85) * mm});
            skLineSegment(sketch, "E18.13.0.4", {"start": v(1316.5, 202.85) * mm, "end": v(1316.5, 205.85) * mm});
            skArc(sketch, "E18.13.0.5", {"start": v(1340, 198.85) * mm, "mid": v(1338.83, 201.67) * mm, "end": v(1336, 202.85) * mm});
            skArc(sketch, "E18.13.0.6", {"start": v(1347, 202.85) * mm, "mid": v(1344.17, 201.67) * mm, "end": v(1343, 198.85) * mm});
            skLineSegment(sketch, "E18.13.0.7", {"start": v(1366.5, 202.85) * mm, "end": v(1366.5, 205.85) * mm});
            skLineSegment(sketch, "E18.13.0.8", {"start": v(1316.5, 205.85) * mm, "end": v(1366.5, 205.85) * mm});
            skLineSegment(sketch, "E18.13.0.9", {"start": v(1347, 202.85) * mm, "end": v(1366.5, 202.85) * mm});
            skArc(sketch, "E18.13.0.10", {"start": v(1336, 102.85) * mm, "mid": v(1338.83, 104.02) * mm, "end": v(1340, 106.85) * mm});
            skArc(sketch, "E18.13.0.11", {"start": v(1343, 106.85) * mm, "mid": v(1344.17, 104.02) * mm, "end": v(1347, 102.85) * mm});
            skLineSegment(sketch, "E18.14.0.0", {"start": v(1416.5, 202.85) * mm, "end": v(1436, 202.85) * mm});
            skLineSegment(sketch, "E18.14.0.1", {"start": v(1443, 106.85) * mm, "end": v(1443, 198.85) * mm});
            skLineSegment(sketch, "E18.14.0.2", {"start": v(1440, 106.85) * mm, "end": v(1440, 198.85) * mm});
            skPoint(sketch, "E18.14.0.3", {"position": v(1443, 202.85) * mm});
            skLineSegment(sketch, "E18.14.0.4", {"start": v(1416.5, 202.85) * mm, "end": v(1416.5, 205.85) * mm});
            skArc(sketch, "E18.14.0.5", {"start": v(1440, 198.85) * mm, "mid": v(1438.83, 201.67) * mm, "end": v(1436, 202.85) * mm});
            skArc(sketch, "E18.14.0.6", {"start": v(1447, 202.85) * mm, "mid": v(1444.17, 201.67) * mm, "end": v(1443, 198.85) * mm});
            skLineSegment(sketch, "E18.14.0.7", {"start": v(1466.5, 202.85) * mm, "end": v(1466.5, 205.85) * mm});
            skLineSegment(sketch, "E18.14.0.8", {"start": v(1416.5, 205.85) * mm, "end": v(1466.5, 205.85) * mm});
            skLineSegment(sketch, "E18.14.0.9", {"start": v(1447, 202.85) * mm, "end": v(1466.5, 202.85) * mm});
            skArc(sketch, "E18.14.0.10", {"start": v(1436, 102.85) * mm, "mid": v(1438.83, 104.02) * mm, "end": v(1440, 106.85) * mm});
            skArc(sketch, "E18.14.0.11", {"start": v(1443, 106.85) * mm, "mid": v(1444.17, 104.02) * mm, "end": v(1447, 102.85) * mm});
            skLineSegment(sketch, "E18.15.0.0", {"start": v(1516.5, 202.85) * mm, "end": v(1536, 202.85) * mm});
            skLineSegment(sketch, "E18.15.0.1", {"start": v(1543, 106.85) * mm, "end": v(1543, 198.85) * mm});
            skLineSegment(sketch, "E18.15.0.2", {"start": v(1540, 106.85) * mm, "end": v(1540, 198.85) * mm});
            skPoint(sketch, "E18.15.0.3", {"position": v(1543, 202.85) * mm});
            skLineSegment(sketch, "E18.15.0.4", {"start": v(1516.5, 202.85) * mm, "end": v(1516.5, 205.85) * mm});
            skArc(sketch, "E18.15.0.5", {"start": v(1540, 198.85) * mm, "mid": v(1538.83, 201.67) * mm, "end": v(1536, 202.85) * mm});
            skArc(sketch, "E18.15.0.6", {"start": v(1547, 202.85) * mm, "mid": v(1544.17, 201.67) * mm, "end": v(1543, 198.85) * mm});
            skLineSegment(sketch, "E18.15.0.7", {"start": v(1566.5, 202.85) * mm, "end": v(1566.5, 205.85) * mm});
            skLineSegment(sketch, "E18.15.0.8", {"start": v(1516.5, 205.85) * mm, "end": v(1566.5, 205.85) * mm});
            skLineSegment(sketch, "E18.15.0.9", {"start": v(1547, 202.85) * mm, "end": v(1566.5, 202.85) * mm});
            skArc(sketch, "E18.15.0.10", {"start": v(1536, 102.85) * mm, "mid": v(1538.83, 104.02) * mm, "end": v(1540, 106.85) * mm});
            skArc(sketch, "E18.15.0.11", {"start": v(1543, 106.85) * mm, "mid": v(1544.17, 104.02) * mm, "end": v(1547, 102.85) * mm});
            skLineSegment(sketch, "E18.16.0.0", {"start": v(1616.5, 202.85) * mm, "end": v(1636, 202.85) * mm});
            skLineSegment(sketch, "E18.16.0.1", {"start": v(1643, 106.85) * mm, "end": v(1643, 198.85) * mm});
            skLineSegment(sketch, "E18.16.0.2", {"start": v(1640, 106.85) * mm, "end": v(1640, 198.85) * mm});
            skPoint(sketch, "E18.16.0.3", {"position": v(1643, 202.85) * mm});
            skLineSegment(sketch, "E18.16.0.4", {"start": v(1616.5, 202.85) * mm, "end": v(1616.5, 205.85) * mm});
            skArc(sketch, "E18.16.0.5", {"start": v(1640, 198.85) * mm, "mid": v(1638.83, 201.67) * mm, "end": v(1636, 202.85) * mm});
            skArc(sketch, "E18.16.0.6", {"start": v(1647, 202.85) * mm, "mid": v(1644.17, 201.67) * mm, "end": v(1643, 198.85) * mm});
            skLineSegment(sketch, "E18.16.0.7", {"start": v(1666.5, 202.85) * mm, "end": v(1666.5, 205.85) * mm});
            skLineSegment(sketch, "E18.16.0.8", {"start": v(1616.5, 205.85) * mm, "end": v(1666.5, 205.85) * mm});
            skLineSegment(sketch, "E18.16.0.9", {"start": v(1647, 202.85) * mm, "end": v(1666.5, 202.85) * mm});
            skArc(sketch, "E18.16.0.10", {"start": v(1636, 102.85) * mm, "mid": v(1638.83, 104.02) * mm, "end": v(1640, 106.85) * mm});
            skArc(sketch, "E18.16.0.11", {"start": v(1643, 106.85) * mm, "mid": v(1644.17, 104.02) * mm, "end": v(1647, 102.85) * mm});
            skLineSegment(sketch, "E18.17.0.0", {"start": v(1716.5, 202.85) * mm, "end": v(1736, 202.85) * mm});
            skLineSegment(sketch, "E18.17.0.1", {"start": v(1743, 106.85) * mm, "end": v(1743, 198.85) * mm});
            skLineSegment(sketch, "E18.17.0.2", {"start": v(1740, 106.85) * mm, "end": v(1740, 198.85) * mm});
            skPoint(sketch, "E18.17.0.3", {"position": v(1743, 202.85) * mm});
            skLineSegment(sketch, "E18.17.0.4", {"start": v(1716.5, 202.85) * mm, "end": v(1716.5, 205.85) * mm});
            skArc(sketch, "E18.17.0.5", {"start": v(1740, 198.85) * mm, "mid": v(1738.83, 201.67) * mm, "end": v(1736, 202.85) * mm});
            skArc(sketch, "E18.17.0.6", {"start": v(1747, 202.85) * mm, "mid": v(1744.17, 201.67) * mm, "end": v(1743, 198.85) * mm});
            skLineSegment(sketch, "E18.17.0.7", {"start": v(1766.5, 202.85) * mm, "end": v(1766.5, 205.85) * mm});
            skLineSegment(sketch, "E18.17.0.8", {"start": v(1716.5, 205.85) * mm, "end": v(1766.5, 205.85) * mm});
            skLineSegment(sketch, "E18.17.0.9", {"start": v(1747, 202.85) * mm, "end": v(1766.5, 202.85) * mm});
            skArc(sketch, "E18.17.0.10", {"start": v(1736, 102.85) * mm, "mid": v(1738.83, 104.02) * mm, "end": v(1740, 106.85) * mm});
            skArc(sketch, "E18.17.0.11", {"start": v(1743, 106.85) * mm, "mid": v(1744.17, 104.02) * mm, "end": v(1747, 102.85) * mm});
            skLineSegment(sketch, "E18.18.0.0", {"start": v(1816.5, 202.85) * mm, "end": v(1836, 202.85) * mm});
            skLineSegment(sketch, "E18.18.0.1", {"start": v(1843, 106.85) * mm, "end": v(1843, 198.85) * mm});
            skLineSegment(sketch, "E18.18.0.2", {"start": v(1840, 106.85) * mm, "end": v(1840, 198.85) * mm});
            skPoint(sketch, "E18.18.0.3", {"position": v(1843, 202.85) * mm});
            skLineSegment(sketch, "E18.18.0.4", {"start": v(1816.5, 202.85) * mm, "end": v(1816.5, 205.85) * mm});
            skArc(sketch, "E18.18.0.5", {"start": v(1840, 198.85) * mm, "mid": v(1838.83, 201.67) * mm, "end": v(1836, 202.85) * mm});
            skArc(sketch, "E18.18.0.6", {"start": v(1847, 202.85) * mm, "mid": v(1844.17, 201.67) * mm, "end": v(1843, 198.85) * mm});
            skLineSegment(sketch, "E18.18.0.7", {"start": v(1866.5, 202.85) * mm, "end": v(1866.5, 205.85) * mm});
            skLineSegment(sketch, "E18.18.0.8", {"start": v(1816.5, 205.85) * mm, "end": v(1866.5, 205.85) * mm});
            skLineSegment(sketch, "E18.18.0.9", {"start": v(1847, 202.85) * mm, "end": v(1866.5, 202.85) * mm});
            skArc(sketch, "E18.18.0.10", {"start": v(1836, 102.85) * mm, "mid": v(1838.83, 104.02) * mm, "end": v(1840, 106.85) * mm});
            skArc(sketch, "E18.18.0.11", {"start": v(1843, 106.85) * mm, "mid": v(1844.17, 104.02) * mm, "end": v(1847, 102.85) * mm});
            skLineSegment(sketch, "E18.19.0.0", {"start": v(1916.5, 202.85) * mm, "end": v(1936, 202.85) * mm});
            skLineSegment(sketch, "E18.19.0.1", {"start": v(1943, 106.85) * mm, "end": v(1943, 198.85) * mm});
            skLineSegment(sketch, "E18.19.0.2", {"start": v(1940, 106.85) * mm, "end": v(1940, 198.85) * mm});
            skPoint(sketch, "E18.19.0.3", {"position": v(1943, 202.85) * mm});
            skLineSegment(sketch, "E18.19.0.4", {"start": v(1916.5, 202.85) * mm, "end": v(1916.5, 205.85) * mm});
            skArc(sketch, "E18.19.0.5", {"start": v(1940, 198.85) * mm, "mid": v(1938.83, 201.67) * mm, "end": v(1936, 202.85) * mm});
            skArc(sketch, "E18.19.0.6", {"start": v(1947, 202.85) * mm, "mid": v(1944.17, 201.67) * mm, "end": v(1943, 198.85) * mm});
            skLineSegment(sketch, "E18.19.0.7", {"start": v(1966.5, 202.85) * mm, "end": v(1966.5, 205.85) * mm});
            skLineSegment(sketch, "E18.19.0.8", {"start": v(1916.5, 205.85) * mm, "end": v(1966.5, 205.85) * mm});
            skLineSegment(sketch, "E18.19.0.9", {"start": v(1947, 202.85) * mm, "end": v(1966.5, 202.85) * mm});
            skArc(sketch, "E18.19.0.10", {"start": v(1936, 102.85) * mm, "mid": v(1938.83, 104.02) * mm, "end": v(1940, 106.85) * mm});
            skArc(sketch, "E18.19.0.11", {"start": v(1943, 106.85) * mm, "mid": v(1944.17, 104.02) * mm, "end": v(1947, 102.85) * mm});
            skLineSegment(sketch, "E18.20.0.0", {"start": v(2016.5, 202.85) * mm, "end": v(2036, 202.85) * mm});
            skLineSegment(sketch, "E18.20.0.1", {"start": v(2043, 106.85) * mm, "end": v(2043, 198.85) * mm});
            skLineSegment(sketch, "E18.20.0.2", {"start": v(2040, 106.85) * mm, "end": v(2040, 198.85) * mm});
            skPoint(sketch, "E18.20.0.3", {"position": v(2043, 202.85) * mm});
            skLineSegment(sketch, "E18.20.0.4", {"start": v(2016.5, 202.85) * mm, "end": v(2016.5, 205.85) * mm});
            skArc(sketch, "E18.20.0.5", {"start": v(2040, 198.85) * mm, "mid": v(2038.83, 201.67) * mm, "end": v(2036, 202.85) * mm});
            skArc(sketch, "E18.20.0.6", {"start": v(2047, 202.85) * mm, "mid": v(2044.17, 201.67) * mm, "end": v(2043, 198.85) * mm});
            skLineSegment(sketch, "E18.20.0.7", {"start": v(2066.5, 202.85) * mm, "end": v(2066.5, 205.85) * mm});
            skLineSegment(sketch, "E18.20.0.8", {"start": v(2016.5, 205.85) * mm, "end": v(2066.5, 205.85) * mm});
            skLineSegment(sketch, "E18.20.0.9", {"start": v(2047, 202.85) * mm, "end": v(2066.5, 202.85) * mm});
            skArc(sketch, "E18.20.0.10", {"start": v(2036, 102.85) * mm, "mid": v(2038.83, 104.02) * mm, "end": v(2040, 106.85) * mm});
            skArc(sketch, "E18.20.0.11", {"start": v(2043, 106.85) * mm, "mid": v(2044.17, 104.02) * mm, "end": v(2047, 102.85) * mm});
            skLineSegment(sketch, "E18.21.0.0", {"start": v(2116.5, 202.85) * mm, "end": v(2136, 202.85) * mm});
            skLineSegment(sketch, "E18.21.0.1", {"start": v(2143, 106.85) * mm, "end": v(2143, 198.85) * mm});
            skLineSegment(sketch, "E18.21.0.2", {"start": v(2140, 106.85) * mm, "end": v(2140, 198.85) * mm});
            skPoint(sketch, "E18.21.0.3", {"position": v(2143, 202.85) * mm});
            skLineSegment(sketch, "E18.21.0.4", {"start": v(2116.5, 202.85) * mm, "end": v(2116.5, 205.85) * mm});
            skArc(sketch, "E18.21.0.5", {"start": v(2140, 198.85) * mm, "mid": v(2138.83, 201.67) * mm, "end": v(2136, 202.85) * mm});
            skArc(sketch, "E18.21.0.6", {"start": v(2147, 202.85) * mm, "mid": v(2144.17, 201.67) * mm, "end": v(2143, 198.85) * mm});
            skLineSegment(sketch, "E18.21.0.7", {"start": v(2166.5, 202.85) * mm, "end": v(2166.5, 205.85) * mm});
            skLineSegment(sketch, "E18.21.0.8", {"start": v(2116.5, 205.85) * mm, "end": v(2166.5, 205.85) * mm});
            skLineSegment(sketch, "E18.21.0.9", {"start": v(2147, 202.85) * mm, "end": v(2166.5, 202.85) * mm});
            skArc(sketch, "E18.21.0.10", {"start": v(2136, 102.85) * mm, "mid": v(2138.83, 104.02) * mm, "end": v(2140, 106.85) * mm});
            skArc(sketch, "E18.21.0.11", {"start": v(2143, 106.85) * mm, "mid": v(2144.17, 104.02) * mm, "end": v(2147, 102.85) * mm});
            skLineSegment(sketch, "E18.22.0.0", {"start": v(2216.5, 202.85) * mm, "end": v(2236, 202.85) * mm});
            skLineSegment(sketch, "E18.22.0.1", {"start": v(2243, 106.85) * mm, "end": v(2243, 198.85) * mm});
            skLineSegment(sketch, "E18.22.0.2", {"start": v(2240, 106.85) * mm, "end": v(2240, 198.85) * mm});
            skPoint(sketch, "E18.22.0.3", {"position": v(2243, 202.85) * mm});
            skLineSegment(sketch, "E18.22.0.4", {"start": v(2216.5, 202.85) * mm, "end": v(2216.5, 205.85) * mm});
            skArc(sketch, "E18.22.0.5", {"start": v(2240, 198.85) * mm, "mid": v(2238.83, 201.67) * mm, "end": v(2236, 202.85) * mm});
            skArc(sketch, "E18.22.0.6", {"start": v(2247, 202.85) * mm, "mid": v(2244.17, 201.67) * mm, "end": v(2243, 198.85) * mm});
            skLineSegment(sketch, "E18.22.0.7", {"start": v(2266.5, 202.85) * mm, "end": v(2266.5, 205.85) * mm});
            skLineSegment(sketch, "E18.22.0.8", {"start": v(2216.5, 205.85) * mm, "end": v(2266.5, 205.85) * mm});
            skLineSegment(sketch, "E18.22.0.9", {"start": v(2247, 202.85) * mm, "end": v(2266.5, 202.85) * mm});
            skArc(sketch, "E18.22.0.10", {"start": v(2236, 102.85) * mm, "mid": v(2238.83, 104.02) * mm, "end": v(2240, 106.85) * mm});
            skArc(sketch, "E18.22.0.11", {"start": v(2243, 106.85) * mm, "mid": v(2244.17, 104.02) * mm, "end": v(2247, 102.85) * mm});
            skLineSegment(sketch, "E18.23.0.0", {"start": v(2316.5, 202.85) * mm, "end": v(2336, 202.85) * mm});
            skLineSegment(sketch, "E18.23.0.1", {"start": v(2343, 106.85) * mm, "end": v(2343, 198.85) * mm});
            skLineSegment(sketch, "E18.23.0.2", {"start": v(2340, 106.85) * mm, "end": v(2340, 198.85) * mm});
            skPoint(sketch, "E18.23.0.3", {"position": v(2343, 202.85) * mm});
            skLineSegment(sketch, "E18.23.0.4", {"start": v(2316.5, 202.85) * mm, "end": v(2316.5, 205.85) * mm});
            skArc(sketch, "E18.23.0.5", {"start": v(2340, 198.85) * mm, "mid": v(2338.83, 201.67) * mm, "end": v(2336, 202.85) * mm});
            skArc(sketch, "E18.23.0.6", {"start": v(2347, 202.85) * mm, "mid": v(2344.17, 201.67) * mm, "end": v(2343, 198.85) * mm});
            skLineSegment(sketch, "E18.23.0.7", {"start": v(2366.5, 202.85) * mm, "end": v(2366.5, 205.85) * mm});
            skLineSegment(sketch, "E18.23.0.8", {"start": v(2316.5, 205.85) * mm, "end": v(2366.5, 205.85) * mm});
            skLineSegment(sketch, "E18.23.0.9", {"start": v(2347, 202.85) * mm, "end": v(2366.5, 202.85) * mm});
            skArc(sketch, "E18.23.0.10", {"start": v(2336, 102.85) * mm, "mid": v(2338.83, 104.02) * mm, "end": v(2340, 106.85) * mm});
            skArc(sketch, "E18.23.0.11", {"start": v(2343, 106.85) * mm, "mid": v(2344.17, 104.02) * mm, "end": v(2347, 102.85) * mm});
            skLineSegment(sketch, "E18.24.0.0", {"start": v(2416.5, 202.85) * mm, "end": v(2436, 202.85) * mm});
            skLineSegment(sketch, "E18.24.0.1", {"start": v(2443, 106.85) * mm, "end": v(2443, 198.85) * mm});
            skLineSegment(sketch, "E18.24.0.2", {"start": v(2440, 106.85) * mm, "end": v(2440, 198.85) * mm});
            skPoint(sketch, "E18.24.0.3", {"position": v(2443, 202.85) * mm});
            skLineSegment(sketch, "E18.24.0.4", {"start": v(2416.5, 202.85) * mm, "end": v(2416.5, 205.85) * mm});
            skArc(sketch, "E18.24.0.5", {"start": v(2440, 198.85) * mm, "mid": v(2438.83, 201.67) * mm, "end": v(2436, 202.85) * mm});
            skArc(sketch, "E18.24.0.6", {"start": v(2447, 202.85) * mm, "mid": v(2444.17, 201.67) * mm, "end": v(2443, 198.85) * mm});
            skLineSegment(sketch, "E18.24.0.7", {"start": v(2466.5, 202.85) * mm, "end": v(2466.5, 205.85) * mm});
            skLineSegment(sketch, "E18.24.0.8", {"start": v(2416.5, 205.85) * mm, "end": v(2466.5, 205.85) * mm});
            skLineSegment(sketch, "E18.24.0.9", {"start": v(2447, 202.85) * mm, "end": v(2466.5, 202.85) * mm});
            skArc(sketch, "E18.24.0.10", {"start": v(2436, 102.85) * mm, "mid": v(2438.83, 104.02) * mm, "end": v(2440, 106.85) * mm});
            skArc(sketch, "E18.24.0.11", {"start": v(2443, 106.85) * mm, "mid": v(2444.17, 104.02) * mm, "end": v(2447, 102.85) * mm});
            skLineSegment(sketch, "E18.direction1", {"start": v(36, 102.85) * mm, "end": v(136, 102.85) * mm, "construction": true});
            skLineSegment(sketch, "E19", {"start": v(36, 102.85) * mm, "end": v(47, 102.85) * mm});
            skSolve(sketch);
        }
        {
            var Q0;
            Q0 = qSketchRegion(id + "F2", true);
            extrude(context, id + "F3", {"entities" : qUnion([Q0]), "operationType" : NewBodyOperationType.ADD, "oppositeDirection" : true, "depth" : 6000 * mm});
        }
        {
            var Q0;
            Q0=makeQuery(id+"F1.opExtrude","CAP_FACE",FACE,{"disambiguationData":[OSD([sQuery(id+"F0.wireOp",EDGE,"E0.bottom"),sQuery(id+"F0.wireOp",EDGE,"E0.top"),sQuery(id+"F0.wireOp",EDGE,"E0.left"),sQuery(id+"F0.wireOp",EDGE,"E0.right"),sQuery(id+"F0.wireOp",EDGE,"E1.bottom"),sQuery(id+"F0.wireOp",EDGE,"E1.top"),sQuery(id+"F0.wireOp",EDGE,"E1.left"),sQuery(id+"F0.wireOp",EDGE,"E1.right"),sQuery(id+"F0.wireOp",EDGE,"E2.bottom"),sQuery(id+"F0.wireOp",EDGE,"E2.top"),sQuery(id+"F0.wireOp",EDGE,"E2.left"),sQuery(id+"F0.wireOp",EDGE,"E2.right"),sQuery(id+"F0.wireOp",EDGE,"E3.filletArc"),sQuery(id+"F0.wireOp",EDGE,"E4.filletArc"),sQuery(id+"F0.wireOp",EDGE,"E5.filletArc"),sQuery(id+"F0.wireOp",EDGE,"E6.filletArc"),sQuery(id+"F0.wireOp",EDGE,"E7.1.0.1"),sQuery(id+"F0.wireOp",EDGE,"E7.1.0.3"),sQuery(id+"F0.wireOp",EDGE,"E7.1.0.4"),sQuery(id+"F0.wireOp",EDGE,"E7.1.0.5"),sQuery(id+"F0.wireOp",EDGE,"E7.1.0.6"),sQuery(id+"F0.wireOp",EDGE,"E7.1.0.7"),sQuery(id+"F0.wireOp",EDGE,"E7.1.0.8"),sQuery(id+"F0.wireOp",EDGE,"E7.1.0.9"),sQuery(id+"F0.wireOp",EDGE,"E7.1.0.10"),sQuery(id+"F0.wireOp",EDGE,"E7.1.0.11"),sQuery(id+"F0.wireOp",EDGE,"E7.1.0.12"),sQuery(id+"F0.wireOp",EDGE,"E7.2.0.1"),sQuery(id+"F0.wireOp",EDGE,"E7.2.0.3"),sQuery(id+"F0.wireOp",EDGE,"E7.2.0.4"),sQuery(id+"F0.wireOp",EDGE,"E7.2.0.5"),sQuery(id+"F0.wireOp",EDGE,"E7.2.0.6"),sQuery(id+"F0.wireOp",EDGE,"E7.2.0.7"),sQuery(id+"F0.wireOp",EDGE,"E7.2.0.8"),sQuery(id+"F0.wireOp",EDGE,"E7.2.0.9"),sQuery(id+"F0.wireOp",EDGE,"E7.2.0.10"),sQuery(id+"F0.wireOp",EDGE,"E7.2.0.11"),sQuery(id+"F0.wireOp",EDGE,"E7.2.0.12"),sQuery(id+"F0.wireOp",EDGE,"E7.3.0.1"),sQuery(id+"F0.wireOp",EDGE,"E7.3.0.3"),sQuery(id+"F0.wireOp",EDGE,"E7.3.0.4"),sQuery(id+"F0.wireOp",EDGE,"E7.3.0.5"),sQuery(id+"F0.wireOp",EDGE,"E7.3.0.6"),sQuery(id+"F0.wireOp",EDGE,"E7.3.0.7"),sQuery(id+"F0.wireOp",EDGE,"E7.3.0.8"),sQuery(id+"F0.wireOp",EDGE,"E7.3.0.9"),sQuery(id+"F0.wireOp",EDGE,"E7.3.0.10"),sQuery(id+"F0.wireOp",EDGE,"E7.3.0.11"),sQuery(id+"F0.wireOp",EDGE,"E7.3.0.12"),sQuery(id+"F0.wireOp",EDGE,"E7.4.0.1"),sQuery(id+"F0.wireOp",EDGE,"E7.4.0.3"),sQuery(id+"F0.wireOp",EDGE,"E7.4.0.4"),sQuery(id+"F0.wireOp",EDGE,"E7.4.0.5"),sQuery(id+"F0.wireOp",EDGE,"E7.4.0.6"),sQuery(id+"F0.wireOp",EDGE,"E7.4.0.7"),sQuery(id+"F0.wireOp",EDGE,"E7.4.0.8"),sQuery(id+"F0.wireOp",EDGE,"E7.4.0.9"),sQuery(id+"F0.wireOp",EDGE,"E7.4.0.10"),sQuery(id+"F0.wireOp",EDGE,"E7.4.0.11"),sQuery(id+"F0.wireOp",EDGE,"E7.4.0.12"),sQuery(id+"F0.wireOp",EDGE,"E7.5.0.1"),sQuery(id+"F0.wireOp",EDGE,"E7.5.0.3"),sQuery(id+"F0.wireOp",EDGE,"E7.5.0.4"),sQuery(id+"F0.wireOp",EDGE,"E7.5.0.5"),sQuery(id+"F0.wireOp",EDGE,"E7.5.0.6"),sQuery(id+"F0.wireOp",EDGE,"E7.5.0.7"),sQuery(id+"F0.wireOp",EDGE,"E7.5.0.8"),sQuery(id+"F0.wireOp",EDGE,"E7.5.0.9"),sQuery(id+"F0.wireOp",EDGE,"E7.5.0.10"),sQuery(id+"F0.wireOp",EDGE,"E7.5.0.11"),sQuery(id+"F0.wireOp",EDGE,"E7.5.0.12"),sQuery(id+"F0.wireOp",EDGE,"E7.6.0.1"),sQuery(id+"F0.wireOp",EDGE,"E7.6.0.3"),sQuery(id+"F0.wireOp",EDGE,"E7.6.0.4"),sQuery(id+"F0.wireOp",EDGE,"E7.6.0.5"),sQuery(id+"F0.wireOp",EDGE,"E7.6.0.6"),sQuery(id+"F0.wireOp",EDGE,"E7.6.0.7"),sQuery(id+"F0.wireOp",EDGE,"E7.6.0.8"),sQuery(id+"F0.wireOp",EDGE,"E7.6.0.9"),sQuery(id+"F0.wireOp",EDGE,"E7.6.0.10"),sQuery(id+"F0.wireOp",EDGE,"E7.6.0.11"),sQuery(id+"F0.wireOp",EDGE,"E7.6.0.12"),sQuery(id+"F0.wireOp",EDGE,"E7.7.0.1"),sQuery(id+"F0.wireOp",EDGE,"E7.7.0.3"),sQuery(id+"F0.wireOp",EDGE,"E7.7.0.4"),sQuery(id+"F0.wireOp",EDGE,"E7.7.0.5"),sQuery(id+"F0.wireOp",EDGE,"E7.7.0.6"),sQuery(id+"F0.wireOp",EDGE,"E7.7.0.7"),sQuery(id+"F0.wireOp",EDGE,"E7.7.0.8"),sQuery(id+"F0.wireOp",EDGE,"E7.7.0.9"),sQuery(id+"F0.wireOp",EDGE,"E7.7.0.10"),sQuery(id+"F0.wireOp",EDGE,"E7.7.0.11"),sQuery(id+"F0.wireOp",EDGE,"E7.7.0.12"),sQuery(id+"F0.wireOp",EDGE,"E7.8.0.1"),sQuery(id+"F0.wireOp",EDGE,"E7.8.0.3"),sQuery(id+"F0.wireOp",EDGE,"E7.8.0.4"),sQuery(id+"F0.wireOp",EDGE,"E7.8.0.5"),sQuery(id+"F0.wireOp",EDGE,"E7.8.0.6"),sQuery(id+"F0.wireOp",EDGE,"E7.8.0.7"),sQuery(id+"F0.wireOp",EDGE,"E7.8.0.8"),sQuery(id+"F0.wireOp",EDGE,"E7.8.0.9"),sQuery(id+"F0.wireOp",EDGE,"E7.8.0.10"),sQuery(id+"F0.wireOp",EDGE,"E7.8.0.11"),sQuery(id+"F0.wireOp",EDGE,"E7.8.0.12"),sQuery(id+"F0.wireOp",EDGE,"E7.9.0.1"),sQuery(id+"F0.wireOp",EDGE,"E7.9.0.3"),sQuery(id+"F0.wireOp",EDGE,"E7.9.0.4"),sQuery(id+"F0.wireOp",EDGE,"E7.9.0.5"),sQuery(id+"F0.wireOp",EDGE,"E7.9.0.6"),sQuery(id+"F0.wireOp",EDGE,"E7.9.0.7"),sQuery(id+"F0.wireOp",EDGE,"E7.9.0.8"),sQuery(id+"F0.wireOp",EDGE,"E7.9.0.9"),sQuery(id+"F0.wireOp",EDGE,"E7.9.0.10"),sQuery(id+"F0.wireOp",EDGE,"E7.9.0.11"),sQuery(id+"F0.wireOp",EDGE,"E7.9.0.12"),sQuery(id+"F0.wireOp",EDGE,"E7.10.0.1"),sQuery(id+"F0.wireOp",EDGE,"E7.10.0.3"),sQuery(id+"F0.wireOp",EDGE,"E7.10.0.4"),sQuery(id+"F0.wireOp",EDGE,"E7.10.0.5"),sQuery(id+"F0.wireOp",EDGE,"E7.10.0.6"),sQuery(id+"F0.wireOp",EDGE,"E7.10.0.7"),sQuery(id+"F0.wireOp",EDGE,"E7.10.0.8"),sQuery(id+"F0.wireOp",EDGE,"E7.10.0.9"),sQuery(id+"F0.wireOp",EDGE,"E7.10.0.10"),sQuery(id+"F0.wireOp",EDGE,"E7.10.0.11"),sQuery(id+"F0.wireOp",EDGE,"E7.10.0.12"),sQuery(id+"F0.wireOp",EDGE,"E7.11.0.1"),sQuery(id+"F0.wireOp",EDGE,"E7.11.0.3"),sQuery(id+"F0.wireOp",EDGE,"E7.11.0.4"),sQuery(id+"F0.wireOp",EDGE,"E7.11.0.5"),sQuery(id+"F0.wireOp",EDGE,"E7.11.0.6"),sQuery(id+"F0.wireOp",EDGE,"E7.11.0.7"),sQuery(id+"F0.wireOp",EDGE,"E7.11.0.8"),sQuery(id+"F0.wireOp",EDGE,"E7.11.0.9"),sQuery(id+"F0.wireOp",EDGE,"E7.11.0.10"),sQuery(id+"F0.wireOp",EDGE,"E7.11.0.11"),sQuery(id+"F0.wireOp",EDGE,"E7.11.0.12"),sQuery(id+"F0.wireOp",EDGE,"E7.12.0.1"),sQuery(id+"F0.wireOp",EDGE,"E7.12.0.3"),sQuery(id+"F0.wireOp",EDGE,"E7.12.0.4"),sQuery(id+"F0.wireOp",EDGE,"E7.12.0.5"),sQuery(id+"F0.wireOp",EDGE,"E7.12.0.6"),sQuery(id+"F0.wireOp",EDGE,"E7.12.0.7"),sQuery(id+"F0.wireOp",EDGE,"E7.12.0.8"),sQuery(id+"F0.wireOp",EDGE,"E7.12.0.9"),sQuery(id+"F0.wireOp",EDGE,"E7.12.0.10"),sQuery(id+"F0.wireOp",EDGE,"E7.12.0.11"),sQuery(id+"F0.wireOp",EDGE,"E7.12.0.12"),sQuery(id+"F0.wireOp",EDGE,"E7.13.0.1"),sQuery(id+"F0.wireOp",EDGE,"E7.13.0.3"),sQuery(id+"F0.wireOp",EDGE,"E7.13.0.4"),sQuery(id+"F0.wireOp",EDGE,"E7.13.0.5"),sQuery(id+"F0.wireOp",EDGE,"E7.13.0.6"),sQuery(id+"F0.wireOp",EDGE,"E7.13.0.7"),sQuery(id+"F0.wireOp",EDGE,"E7.13.0.8"),sQuery(id+"F0.wireOp",EDGE,"E7.13.0.9"),sQuery(id+"F0.wireOp",EDGE,"E7.13.0.10"),sQuery(id+"F0.wireOp",EDGE,"E7.13.0.11"),sQuery(id+"F0.wireOp",EDGE,"E7.13.0.12"),sQuery(id+"F0.wireOp",EDGE,"E7.14.0.1"),sQuery(id+"F0.wireOp",EDGE,"E7.14.0.3"),sQuery(id+"F0.wireOp",EDGE,"E7.14.0.4"),sQuery(id+"F0.wireOp",EDGE,"E7.14.0.5"),sQuery(id+"F0.wireOp",EDGE,"E7.14.0.6"),sQuery(id+"F0.wireOp",EDGE,"E7.14.0.7"),sQuery(id+"F0.wireOp",EDGE,"E7.14.0.8"),sQuery(id+"F0.wireOp",EDGE,"E7.14.0.9"),sQuery(id+"F0.wireOp",EDGE,"E7.14.0.10"),sQuery(id+"F0.wireOp",EDGE,"E7.14.0.11"),sQuery(id+"F0.wireOp",EDGE,"E7.14.0.12"),sQuery(id+"F0.wireOp",EDGE,"E7.15.0.1"),sQuery(id+"F0.wireOp",EDGE,"E7.15.0.3"),sQuery(id+"F0.wireOp",EDGE,"E7.15.0.4"),sQuery(id+"F0.wireOp",EDGE,"E7.15.0.5"),sQuery(id+"F0.wireOp",EDGE,"E7.15.0.6"),sQuery(id+"F0.wireOp",EDGE,"E7.15.0.7"),sQuery(id+"F0.wireOp",EDGE,"E7.15.0.8"),sQuery(id+"F0.wireOp",EDGE,"E7.15.0.9"),sQuery(id+"F0.wireOp",EDGE,"E7.15.0.10"),sQuery(id+"F0.wireOp",EDGE,"E7.15.0.11"),sQuery(id+"F0.wireOp",EDGE,"E7.15.0.12"),sQuery(id+"F0.wireOp",EDGE,"E7.16.0.1"),sQuery(id+"F0.wireOp",EDGE,"E7.16.0.3"),sQuery(id+"F0.wireOp",EDGE,"E7.16.0.4"),sQuery(id+"F0.wireOp",EDGE,"E7.16.0.5"),sQuery(id+"F0.wireOp",EDGE,"E7.16.0.6"),sQuery(id+"F0.wireOp",EDGE,"E7.16.0.7"),sQuery(id+"F0.wireOp",EDGE,"E7.16.0.8"),sQuery(id+"F0.wireOp",EDGE,"E7.16.0.9"),sQuery(id+"F0.wireOp",EDGE,"E7.16.0.10"),sQuery(id+"F0.wireOp",EDGE,"E7.16.0.11"),sQuery(id+"F0.wireOp",EDGE,"E7.16.0.12"),sQuery(id+"F0.wireOp",EDGE,"E7.17.0.1"),sQuery(id+"F0.wireOp",EDGE,"E7.17.0.3"),sQuery(id+"F0.wireOp",EDGE,"E7.17.0.4"),sQuery(id+"F0.wireOp",EDGE,"E7.17.0.5"),sQuery(id+"F0.wireOp",EDGE,"E7.17.0.6"),sQuery(id+"F0.wireOp",EDGE,"E7.17.0.7"),sQuery(id+"F0.wireOp",EDGE,"E7.17.0.8"),sQuery(id+"F0.wireOp",EDGE,"E7.17.0.9"),sQuery(id+"F0.wireOp",EDGE,"E7.17.0.10"),sQuery(id+"F0.wireOp",EDGE,"E7.17.0.11"),sQuery(id+"F0.wireOp",EDGE,"E7.17.0.12"),sQuery(id+"F0.wireOp",EDGE,"E7.18.0.1"),sQuery(id+"F0.wireOp",EDGE,"E7.18.0.3"),sQuery(id+"F0.wireOp",EDGE,"E7.18.0.4"),sQuery(id+"F0.wireOp",EDGE,"E7.18.0.5"),sQuery(id+"F0.wireOp",EDGE,"E7.18.0.6"),sQuery(id+"F0.wireOp",EDGE,"E7.18.0.7"),sQuery(id+"F0.wireOp",EDGE,"E7.18.0.8"),sQuery(id+"F0.wireOp",EDGE,"E7.18.0.9"),sQuery(id+"F0.wireOp",EDGE,"E7.18.0.10"),sQuery(id+"F0.wireOp",EDGE,"E7.18.0.11"),sQuery(id+"F0.wireOp",EDGE,"E7.18.0.12"),sQuery(id+"F0.wireOp",EDGE,"E7.19.0.1"),sQuery(id+"F0.wireOp",EDGE,"E7.19.0.3"),sQuery(id+"F0.wireOp",EDGE,"E7.19.0.4"),sQuery(id+"F0.wireOp",EDGE,"E7.19.0.5"),sQuery(id+"F0.wireOp",EDGE,"E7.19.0.6"),sQuery(id+"F0.wireOp",EDGE,"E7.19.0.7"),sQuery(id+"F0.wireOp",EDGE,"E7.19.0.8"),sQuery(id+"F0.wireOp",EDGE,"E7.19.0.9"),sQuery(id+"F0.wireOp",EDGE,"E7.19.0.10"),sQuery(id+"F0.wireOp",EDGE,"E7.19.0.11"),sQuery(id+"F0.wireOp",EDGE,"E7.19.0.12"),sQuery(id+"F0.wireOp",EDGE,"E7.20.0.1"),sQuery(id+"F0.wireOp",EDGE,"E7.20.0.3"),sQuery(id+"F0.wireOp",EDGE,"E7.20.0.4"),sQuery(id+"F0.wireOp",EDGE,"E7.20.0.5"),sQuery(id+"F0.wireOp",EDGE,"E7.20.0.6"),sQuery(id+"F0.wireOp",EDGE,"E7.20.0.7"),sQuery(id+"F0.wireOp",EDGE,"E7.20.0.8"),sQuery(id+"F0.wireOp",EDGE,"E7.20.0.9"),sQuery(id+"F0.wireOp",EDGE,"E7.20.0.10"),sQuery(id+"F0.wireOp",EDGE,"E7.20.0.11"),sQuery(id+"F0.wireOp",EDGE,"E7.20.0.12"),sQuery(id+"F0.wireOp",EDGE,"E7.21.0.1"),sQuery(id+"F0.wireOp",EDGE,"E7.21.0.3"),sQuery(id+"F0.wireOp",EDGE,"E7.21.0.4"),sQuery(id+"F0.wireOp",EDGE,"E7.21.0.5"),sQuery(id+"F0.wireOp",EDGE,"E7.21.0.6"),sQuery(id+"F0.wireOp",EDGE,"E7.21.0.7"),sQuery(id+"F0.wireOp",EDGE,"E7.21.0.8"),sQuery(id+"F0.wireOp",EDGE,"E7.21.0.9"),sQuery(id+"F0.wireOp",EDGE,"E7.21.0.10"),sQuery(id+"F0.wireOp",EDGE,"E7.21.0.11"),sQuery(id+"F0.wireOp",EDGE,"E7.21.0.12"),sQuery(id+"F0.wireOp",EDGE,"E7.22.0.1"),sQuery(id+"F0.wireOp",EDGE,"E7.22.0.3"),sQuery(id+"F0.wireOp",EDGE,"E7.22.0.4"),sQuery(id+"F0.wireOp",EDGE,"E7.22.0.5"),sQuery(id+"F0.wireOp",EDGE,"E7.22.0.6"),sQuery(id+"F0.wireOp",EDGE,"E7.22.0.7"),sQuery(id+"F0.wireOp",EDGE,"E7.22.0.8"),sQuery(id+"F0.wireOp",EDGE,"E7.22.0.9"),sQuery(id+"F0.wireOp",EDGE,"E7.22.0.10"),sQuery(id+"F0.wireOp",EDGE,"E7.22.0.11"),sQuery(id+"F0.wireOp",EDGE,"E7.22.0.12"),sQuery(id+"F0.wireOp",EDGE,"E7.23.0.1"),sQuery(id+"F0.wireOp",EDGE,"E7.23.0.3"),sQuery(id+"F0.wireOp",EDGE,"E7.23.0.4"),sQuery(id+"F0.wireOp",EDGE,"E7.23.0.5"),sQuery(id+"F0.wireOp",EDGE,"E7.23.0.6"),sQuery(id+"F0.wireOp",EDGE,"E7.23.0.7"),sQuery(id+"F0.wireOp",EDGE,"E7.23.0.8"),sQuery(id+"F0.wireOp",EDGE,"E7.23.0.9"),sQuery(id+"F0.wireOp",EDGE,"E7.23.0.10"),sQuery(id+"F0.wireOp",EDGE,"E7.23.0.11"),sQuery(id+"F0.wireOp",EDGE,"E7.23.0.12"),sQuery(id+"F0.wireOp",EDGE,"E7.24.0.1"),sQuery(id+"F0.wireOp",EDGE,"E7.24.0.3"),sQuery(id+"F0.wireOp",EDGE,"E7.24.0.4"),sQuery(id+"F0.wireOp",EDGE,"E7.24.0.5"),sQuery(id+"F0.wireOp",EDGE,"E7.24.0.6"),sQuery(id+"F0.wireOp",EDGE,"E7.24.0.7"),sQuery(id+"F0.wireOp",EDGE,"E7.24.0.8"),sQuery(id+"F0.wireOp",EDGE,"E7.24.0.9"),sQuery(id+"F0.wireOp",EDGE,"E7.24.0.10"),sQuery(id+"F0.wireOp",EDGE,"E7.24.0.11"),sQuery(id+"F0.wireOp",EDGE,"E7.24.0.12"),sQuery(id+"F0.wireOp",EDGE,"E7.25.0.1"),sQuery(id+"F0.wireOp",EDGE,"E7.25.0.3"),sQuery(id+"F0.wireOp",EDGE,"E7.25.0.4"),sQuery(id+"F0.wireOp",EDGE,"E7.25.0.5"),sQuery(id+"F0.wireOp",EDGE,"E7.25.0.6"),sQuery(id+"F0.wireOp",EDGE,"E7.25.0.7"),sQuery(id+"F0.wireOp",EDGE,"E7.25.0.8"),sQuery(id+"F0.wireOp",EDGE,"E7.25.0.9"),sQuery(id+"F0.wireOp",EDGE,"E7.25.0.10"),sQuery(id+"F0.wireOp",EDGE,"E7.25.0.11"),sQuery(id+"F0.wireOp",EDGE,"E7.25.0.12"),sQuery(id+"F0.wireOp",EDGE,"E7.26.0.1"),sQuery(id+"F0.wireOp",EDGE,"E7.26.0.3"),sQuery(id+"F0.wireOp",EDGE,"E7.26.0.4"),sQuery(id+"F0.wireOp",EDGE,"E7.26.0.5"),sQuery(id+"F0.wireOp",EDGE,"E7.26.0.6"),sQuery(id+"F0.wireOp",EDGE,"E7.26.0.7"),sQuery(id+"F0.wireOp",EDGE,"E7.26.0.8"),sQuery(id+"F0.wireOp",EDGE,"E7.26.0.9"),sQuery(id+"F0.wireOp",EDGE,"E7.26.0.10"),sQuery(id+"F0.wireOp",EDGE,"E7.26.0.11"),sQuery(id+"F0.wireOp",EDGE,"E7.26.0.12"),sQuery(id+"F0.wireOp",EDGE,"E7.27.0.1"),sQuery(id+"F0.wireOp",EDGE,"E7.27.0.3"),sQuery(id+"F0.wireOp",EDGE,"E7.27.0.4"),sQuery(id+"F0.wireOp",EDGE,"E7.27.0.5"),sQuery(id+"F0.wireOp",EDGE,"E7.27.0.6"),sQuery(id+"F0.wireOp",EDGE,"E7.27.0.7"),sQuery(id+"F0.wireOp",EDGE,"E7.27.0.8"),sQuery(id+"F0.wireOp",EDGE,"E7.27.0.9"),sQuery(id+"F0.wireOp",EDGE,"E7.27.0.10"),sQuery(id+"F0.wireOp",EDGE,"E7.27.0.11"),sQuery(id+"F0.wireOp",EDGE,"E7.27.0.12"),sQuery(id+"F0.wireOp",EDGE,"E7.28.0.1"),sQuery(id+"F0.wireOp",EDGE,"E7.28.0.3"),sQuery(id+"F0.wireOp",EDGE,"E7.28.0.4"),sQuery(id+"F0.wireOp",EDGE,"E7.28.0.5"),sQuery(id+"F0.wireOp",EDGE,"E7.28.0.6"),sQuery(id+"F0.wireOp",EDGE,"E7.28.0.7"),sQuery(id+"F0.wireOp",EDGE,"E7.28.0.8"),sQuery(id+"F0.wireOp",EDGE,"E7.28.0.9"),sQuery(id+"F0.wireOp",EDGE,"E7.28.0.10"),sQuery(id+"F0.wireOp",EDGE,"E7.28.0.11"),sQuery(id+"F0.wireOp",EDGE,"E7.28.0.12"),sQuery(id+"F0.wireOp",EDGE,"E7.29.0.1"),sQuery(id+"F0.wireOp",EDGE,"E7.29.0.3"),sQuery(id+"F0.wireOp",EDGE,"E7.29.0.4"),sQuery(id+"F0.wireOp",EDGE,"E7.29.0.5"),sQuery(id+"F0.wireOp",EDGE,"E7.29.0.6"),sQuery(id+"F0.wireOp",EDGE,"E7.29.0.7"),sQuery(id+"F0.wireOp",EDGE,"E7.29.0.8"),sQuery(id+"F0.wireOp",EDGE,"E7.29.0.9"),sQuery(id+"F0.wireOp",EDGE,"E7.29.0.10"),sQuery(id+"F0.wireOp",EDGE,"E7.29.0.11"),sQuery(id+"F0.wireOp",EDGE,"E7.29.0.12"),sQuery(id+"F0.wireOp",EDGE,"E7.30.0.1"),sQuery(id+"F0.wireOp",EDGE,"E7.30.0.3"),sQuery(id+"F0.wireOp",EDGE,"E7.30.0.4"),sQuery(id+"F0.wireOp",EDGE,"E7.30.0.5"),sQuery(id+"F0.wireOp",EDGE,"E7.30.0.6"),sQuery(id+"F0.wireOp",EDGE,"E7.30.0.7"),sQuery(id+"F0.wireOp",EDGE,"E7.30.0.8"),sQuery(id+"F0.wireOp",EDGE,"E7.30.0.9"),sQuery(id+"F0.wireOp",EDGE,"E7.30.0.10"),sQuery(id+"F0.wireOp",EDGE,"E7.30.0.11"),sQuery(id+"F0.wireOp",EDGE,"E7.30.0.12"),sQuery(id+"F0.wireOp",EDGE,"E7.31.0.1"),sQuery(id+"F0.wireOp",EDGE,"E7.31.0.3"),sQuery(id+"F0.wireOp",EDGE,"E7.31.0.4"),sQuery(id+"F0.wireOp",EDGE,"E7.31.0.5"),sQuery(id+"F0.wireOp",EDGE,"E7.31.0.6"),sQuery(id+"F0.wireOp",EDGE,"E7.31.0.7"),sQuery(id+"F0.wireOp",EDGE,"E7.31.0.8"),sQuery(id+"F0.wireOp",EDGE,"E7.31.0.9"),sQuery(id+"F0.wireOp",EDGE,"E7.31.0.10"),sQuery(id+"F0.wireOp",EDGE,"E7.31.0.11"),sQuery(id+"F0.wireOp",EDGE,"E7.31.0.12"),sQuery(id+"F0.wireOp",EDGE,"E7.32.0.1"),sQuery(id+"F0.wireOp",EDGE,"E7.32.0.3"),sQuery(id+"F0.wireOp",EDGE,"E7.32.0.4"),sQuery(id+"F0.wireOp",EDGE,"E7.32.0.5"),sQuery(id+"F0.wireOp",EDGE,"E7.32.0.6"),sQuery(id+"F0.wireOp",EDGE,"E7.32.0.7"),sQuery(id+"F0.wireOp",EDGE,"E7.32.0.8"),sQuery(id+"F0.wireOp",EDGE,"E7.32.0.9"),sQuery(id+"F0.wireOp",EDGE,"E7.32.0.10"),sQuery(id+"F0.wireOp",EDGE,"E7.32.0.11"),sQuery(id+"F0.wireOp",EDGE,"E7.32.0.12"),sQuery(id+"F0.wireOp",EDGE,"E7.33.0.1"),sQuery(id+"F0.wireOp",EDGE,"E7.33.0.3"),sQuery(id+"F0.wireOp",EDGE,"E7.33.0.4"),sQuery(id+"F0.wireOp",EDGE,"E7.33.0.5"),sQuery(id+"F0.wireOp",EDGE,"E7.33.0.6"),sQuery(id+"F0.wireOp",EDGE,"E7.33.0.7"),sQuery(id+"F0.wireOp",EDGE,"E7.33.0.8"),sQuery(id+"F0.wireOp",EDGE,"E7.33.0.9"),sQuery(id+"F0.wireOp",EDGE,"E7.33.0.10"),sQuery(id+"F0.wireOp",EDGE,"E7.33.0.11"),sQuery(id+"F0.wireOp",EDGE,"E7.33.0.12"),sQuery(id+"F0.wireOp",EDGE,"E7.34.0.1"),sQuery(id+"F0.wireOp",EDGE,"E7.34.0.3"),sQuery(id+"F0.wireOp",EDGE,"E7.34.0.4"),sQuery(id+"F0.wireOp",EDGE,"E7.34.0.5"),sQuery(id+"F0.wireOp",EDGE,"E7.34.0.6"),sQuery(id+"F0.wireOp",EDGE,"E7.34.0.7"),sQuery(id+"F0.wireOp",EDGE,"E7.34.0.8"),sQuery(id+"F0.wireOp",EDGE,"E7.34.0.9"),sQuery(id+"F0.wireOp",EDGE,"E7.34.0.10"),sQuery(id+"F0.wireOp",EDGE,"E7.34.0.11"),sQuery(id+"F0.wireOp",EDGE,"E7.34.0.12"),sQuery(id+"F0.wireOp",EDGE,"E7.35.0.1"),sQuery(id+"F0.wireOp",EDGE,"E7.35.0.3"),sQuery(id+"F0.wireOp",EDGE,"E7.35.0.4"),sQuery(id+"F0.wireOp",EDGE,"E7.35.0.5"),sQuery(id+"F0.wireOp",EDGE,"E7.35.0.6"),sQuery(id+"F0.wireOp",EDGE,"E7.35.0.7"),sQuery(id+"F0.wireOp",EDGE,"E7.35.0.8"),sQuery(id+"F0.wireOp",EDGE,"E7.35.0.9"),sQuery(id+"F0.wireOp",EDGE,"E7.35.0.10"),sQuery(id+"F0.wireOp",EDGE,"E7.35.0.11"),sQuery(id+"F0.wireOp",EDGE,"E7.35.0.12"),sQuery(id+"F0.wireOp",EDGE,"E7.36.0.1"),sQuery(id+"F0.wireOp",EDGE,"E7.36.0.3"),sQuery(id+"F0.wireOp",EDGE,"E7.36.0.4"),sQuery(id+"F0.wireOp",EDGE,"E7.36.0.5"),sQuery(id+"F0.wireOp",EDGE,"E7.36.0.6"),sQuery(id+"F0.wireOp",EDGE,"E7.36.0.7"),sQuery(id+"F0.wireOp",EDGE,"E7.36.0.8"),sQuery(id+"F0.wireOp",EDGE,"E7.36.0.9"),sQuery(id+"F0.wireOp",EDGE,"E7.36.0.10"),sQuery(id+"F0.wireOp",EDGE,"E7.36.0.11"),sQuery(id+"F0.wireOp",EDGE,"E7.36.0.12"),sQuery(id+"F0.wireOp",EDGE,"E7.37.0.1"),sQuery(id+"F0.wireOp",EDGE,"E7.37.0.3"),sQuery(id+"F0.wireOp",EDGE,"E7.37.0.4"),sQuery(id+"F0.wireOp",EDGE,"E7.37.0.5"),sQuery(id+"F0.wireOp",EDGE,"E7.37.0.6"),sQuery(id+"F0.wireOp",EDGE,"E7.37.0.7"),sQuery(id+"F0.wireOp",EDGE,"E7.37.0.8"),sQuery(id+"F0.wireOp",EDGE,"E7.37.0.9"),sQuery(id+"F0.wireOp",EDGE,"E7.37.0.10"),sQuery(id+"F0.wireOp",EDGE,"E7.37.0.11"),sQuery(id+"F0.wireOp",EDGE,"E7.37.0.12"),sQuery(id+"F0.wireOp",EDGE,"E7.38.0.1"),sQuery(id+"F0.wireOp",EDGE,"E7.38.0.3"),sQuery(id+"F0.wireOp",EDGE,"E7.38.0.4"),sQuery(id+"F0.wireOp",EDGE,"E7.38.0.5"),sQuery(id+"F0.wireOp",EDGE,"E7.38.0.6"),sQuery(id+"F0.wireOp",EDGE,"E7.38.0.7"),sQuery(id+"F0.wireOp",EDGE,"E7.38.0.8"),sQuery(id+"F0.wireOp",EDGE,"E7.38.0.9"),sQuery(id+"F0.wireOp",EDGE,"E7.38.0.10"),sQuery(id+"F0.wireOp",EDGE,"E7.38.0.11"),sQuery(id+"F0.wireOp",EDGE,"E7.38.0.12"),sQuery(id+"F0.wireOp",EDGE,"E7.39.0.1"),sQuery(id+"F0.wireOp",EDGE,"E7.39.0.3"),sQuery(id+"F0.wireOp",EDGE,"E7.39.0.4"),sQuery(id+"F0.wireOp",EDGE,"E7.39.0.5"),sQuery(id+"F0.wireOp",EDGE,"E7.39.0.6"),sQuery(id+"F0.wireOp",EDGE,"E7.39.0.7"),sQuery(id+"F0.wireOp",EDGE,"E7.39.0.8"),sQuery(id+"F0.wireOp",EDGE,"E7.39.0.9"),sQuery(id+"F0.wireOp",EDGE,"E7.39.0.10"),sQuery(id+"F0.wireOp",EDGE,"E7.39.0.11"),sQuery(id+"F0.wireOp",EDGE,"E7.39.0.12"),sQuery(id+"F0.wireOp",EDGE,"E7.40.0.1"),sQuery(id+"F0.wireOp",EDGE,"E7.40.0.3"),sQuery(id+"F0.wireOp",EDGE,"E7.40.0.4"),sQuery(id+"F0.wireOp",EDGE,"E7.40.0.5"),sQuery(id+"F0.wireOp",EDGE,"E7.40.0.6"),sQuery(id+"F0.wireOp",EDGE,"E7.40.0.7"),sQuery(id+"F0.wireOp",EDGE,"E7.40.0.8"),sQuery(id+"F0.wireOp",EDGE,"E7.40.0.9"),sQuery(id+"F0.wireOp",EDGE,"E7.40.0.10"),sQuery(id+"F0.wireOp",EDGE,"E7.40.0.11"),sQuery(id+"F0.wireOp",EDGE,"E7.40.0.12"),sQuery(id+"F0.wireOp",EDGE,"E7.41.0.1"),sQuery(id+"F0.wireOp",EDGE,"E7.41.0.3"),sQuery(id+"F0.wireOp",EDGE,"E7.41.0.4"),sQuery(id+"F0.wireOp",EDGE,"E7.41.0.5"),sQuery(id+"F0.wireOp",EDGE,"E7.41.0.6"),sQuery(id+"F0.wireOp",EDGE,"E7.41.0.7"),sQuery(id+"F0.wireOp",EDGE,"E7.41.0.8"),sQuery(id+"F0.wireOp",EDGE,"E7.41.0.9"),sQuery(id+"F0.wireOp",EDGE,"E7.41.0.10"),sQuery(id+"F0.wireOp",EDGE,"E7.41.0.11"),sQuery(id+"F0.wireOp",EDGE,"E7.41.0.12"),sQuery(id+"F0.wireOp",EDGE,"E7.42.0.1"),sQuery(id+"F0.wireOp",EDGE,"E7.42.0.3"),sQuery(id+"F0.wireOp",EDGE,"E7.42.0.4"),sQuery(id+"F0.wireOp",EDGE,"E7.42.0.5"),sQuery(id+"F0.wireOp",EDGE,"E7.42.0.6"),sQuery(id+"F0.wireOp",EDGE,"E7.42.0.7"),sQuery(id+"F0.wireOp",EDGE,"E7.42.0.8"),sQuery(id+"F0.wireOp",EDGE,"E7.42.0.9"),sQuery(id+"F0.wireOp",EDGE,"E7.42.0.10"),sQuery(id+"F0.wireOp",EDGE,"E7.42.0.11"),sQuery(id+"F0.wireOp",EDGE,"E7.42.0.12"),sQuery(id+"F0.wireOp",EDGE,"E7.43.0.1"),sQuery(id+"F0.wireOp",EDGE,"E7.43.0.3"),sQuery(id+"F0.wireOp",EDGE,"E7.43.0.4"),sQuery(id+"F0.wireOp",EDGE,"E7.43.0.5"),sQuery(id+"F0.wireOp",EDGE,"E7.43.0.6"),sQuery(id+"F0.wireOp",EDGE,"E7.43.0.7"),sQuery(id+"F0.wireOp",EDGE,"E7.43.0.8"),sQuery(id+"F0.wireOp",EDGE,"E7.43.0.9"),sQuery(id+"F0.wireOp",EDGE,"E7.43.0.10"),sQuery(id+"F0.wireOp",EDGE,"E7.43.0.11"),sQuery(id+"F0.wireOp",EDGE,"E7.43.0.12"),sQuery(id+"F0.wireOp",EDGE,"E7.44.0.1"),sQuery(id+"F0.wireOp",EDGE,"E7.44.0.3"),sQuery(id+"F0.wireOp",EDGE,"E7.44.0.4"),sQuery(id+"F0.wireOp",EDGE,"E7.44.0.5"),sQuery(id+"F0.wireOp",EDGE,"E7.44.0.6"),sQuery(id+"F0.wireOp",EDGE,"E7.44.0.7"),sQuery(id+"F0.wireOp",EDGE,"E7.44.0.8"),sQuery(id+"F0.wireOp",EDGE,"E7.44.0.9"),sQuery(id+"F0.wireOp",EDGE,"E7.44.0.10"),sQuery(id+"F0.wireOp",EDGE,"E7.44.0.11"),sQuery(id+"F0.wireOp",EDGE,"E7.44.0.12"),sQuery(id+"F0.wireOp",EDGE,"E7.45.0.1"),sQuery(id+"F0.wireOp",EDGE,"E7.45.0.3"),sQuery(id+"F0.wireOp",EDGE,"E7.45.0.4"),sQuery(id+"F0.wireOp",EDGE,"E7.45.0.5"),sQuery(id+"F0.wireOp",EDGE,"E7.45.0.6"),sQuery(id+"F0.wireOp",EDGE,"E7.45.0.7"),sQuery(id+"F0.wireOp",EDGE,"E7.45.0.8"),sQuery(id+"F0.wireOp",EDGE,"E7.45.0.9"),sQuery(id+"F0.wireOp",EDGE,"E7.45.0.10"),sQuery(id+"F0.wireOp",EDGE,"E7.45.0.11"),sQuery(id+"F0.wireOp",EDGE,"E7.45.0.12"),sQuery(id+"F0.wireOp",EDGE,"E7.46.0.1"),sQuery(id+"F0.wireOp",EDGE,"E7.46.0.3"),sQuery(id+"F0.wireOp",EDGE,"E7.46.0.4"),sQuery(id+"F0.wireOp",EDGE,"E7.46.0.5"),sQuery(id+"F0.wireOp",EDGE,"E7.46.0.6"),sQuery(id+"F0.wireOp",EDGE,"E7.46.0.7"),sQuery(id+"F0.wireOp",EDGE,"E7.46.0.8"),sQuery(id+"F0.wireOp",EDGE,"E7.46.0.9"),sQuery(id+"F0.wireOp",EDGE,"E7.46.0.10"),sQuery(id+"F0.wireOp",EDGE,"E7.46.0.11"),sQuery(id+"F0.wireOp",EDGE,"E7.46.0.12"),sQuery(id+"F0.wireOp",EDGE,"E7.47.0.1"),sQuery(id+"F0.wireOp",EDGE,"E7.47.0.3"),sQuery(id+"F0.wireOp",EDGE,"E7.47.0.4"),sQuery(id+"F0.wireOp",EDGE,"E7.47.0.5"),sQuery(id+"F0.wireOp",EDGE,"E7.47.0.6"),sQuery(id+"F0.wireOp",EDGE,"E7.47.0.7"),sQuery(id+"F0.wireOp",EDGE,"E7.47.0.8"),sQuery(id+"F0.wireOp",EDGE,"E7.47.0.9"),sQuery(id+"F0.wireOp",EDGE,"E7.47.0.10"),sQuery(id+"F0.wireOp",EDGE,"E7.47.0.11"),sQuery(id+"F0.wireOp",EDGE,"E7.47.0.12"),sQuery(id+"F0.wireOp",EDGE,"E7.48.0.1"),sQuery(id+"F0.wireOp",EDGE,"E7.48.0.3"),sQuery(id+"F0.wireOp",EDGE,"E7.48.0.4"),sQuery(id+"F0.wireOp",EDGE,"E7.48.0.5"),sQuery(id+"F0.wireOp",EDGE,"E7.48.0.6"),sQuery(id+"F0.wireOp",EDGE,"E7.48.0.7"),sQuery(id+"F0.wireOp",EDGE,"E7.48.0.8"),sQuery(id+"F0.wireOp",EDGE,"E7.48.0.9"),sQuery(id+"F0.wireOp",EDGE,"E7.48.0.10"),sQuery(id+"F0.wireOp",EDGE,"E7.48.0.11"),sQuery(id+"F0.wireOp",EDGE,"E7.48.0.12"),sQuery(id+"F0.wireOp",EDGE,"E7.49.0.1"),sQuery(id+"F0.wireOp",EDGE,"E7.49.0.3"),sQuery(id+"F0.wireOp",EDGE,"E7.49.0.4"),sQuery(id+"F0.wireOp",EDGE,"E7.49.0.5"),sQuery(id+"F0.wireOp",EDGE,"E7.49.0.6"),sQuery(id+"F0.wireOp",EDGE,"E7.49.0.7"),sQuery(id+"F0.wireOp",EDGE,"E7.49.0.8"),sQuery(id+"F0.wireOp",EDGE,"E7.49.0.9"),sQuery(id+"F0.wireOp",EDGE,"E7.49.0.10"),sQuery(id+"F0.wireOp",EDGE,"E7.49.0.11"),sQuery(id+"F0.wireOp",EDGE,"E7.49.0.12"),sQuery(id+"F0.wireOp",EDGE,"E7.50.0.1"),sQuery(id+"F0.wireOp",EDGE,"E7.50.0.3"),sQuery(id+"F0.wireOp",EDGE,"E7.50.0.4"),sQuery(id+"F0.wireOp",EDGE,"E7.50.0.5"),sQuery(id+"F0.wireOp",EDGE,"E7.50.0.6"),sQuery(id+"F0.wireOp",EDGE,"E7.50.0.7"),sQuery(id+"F0.wireOp",EDGE,"E7.50.0.8"),sQuery(id+"F0.wireOp",EDGE,"E7.50.0.9"),sQuery(id+"F0.wireOp",EDGE,"E7.50.0.10"),sQuery(id+"F0.wireOp",EDGE,"E7.50.0.11"),sQuery(id+"F0.wireOp",EDGE,"E7.50.0.12"),sQuery(id+"F0.wireOp",EDGE,"E7.51.0.1"),sQuery(id+"F0.wireOp",EDGE,"E7.51.0.3"),sQuery(id+"F0.wireOp",EDGE,"E7.51.0.4"),sQuery(id+"F0.wireOp",EDGE,"E7.51.0.5"),sQuery(id+"F0.wireOp",EDGE,"E7.51.0.6"),sQuery(id+"F0.wireOp",EDGE,"E7.51.0.7"),sQuery(id+"F0.wireOp",EDGE,"E7.51.0.8"),sQuery(id+"F0.wireOp",EDGE,"E7.51.0.9"),sQuery(id+"F0.wireOp",EDGE,"E7.51.0.10"),sQuery(id+"F0.wireOp",EDGE,"E7.51.0.11"),sQuery(id+"F0.wireOp",EDGE,"E7.51.0.12"),sQuery(id+"F0.wireOp",EDGE,"E7.52.0.1"),sQuery(id+"F0.wireOp",EDGE,"E7.52.0.3"),sQuery(id+"F0.wireOp",EDGE,"E7.52.0.4"),sQuery(id+"F0.wireOp",EDGE,"E7.52.0.5"),sQuery(id+"F0.wireOp",EDGE,"E7.52.0.6"),sQuery(id+"F0.wireOp",EDGE,"E7.52.0.7"),sQuery(id+"F0.wireOp",EDGE,"E7.52.0.8"),sQuery(id+"F0.wireOp",EDGE,"E7.52.0.9"),sQuery(id+"F0.wireOp",EDGE,"E7.52.0.10"),sQuery(id+"F0.wireOp",EDGE,"E7.52.0.11"),sQuery(id+"F0.wireOp",EDGE,"E7.52.0.12"),sQuery(id+"F0.wireOp",EDGE,"E7.53.0.1"),sQuery(id+"F0.wireOp",EDGE,"E7.53.0.3"),sQuery(id+"F0.wireOp",EDGE,"E7.53.0.4"),sQuery(id+"F0.wireOp",EDGE,"E7.53.0.5"),sQuery(id+"F0.wireOp",EDGE,"E7.53.0.6"),sQuery(id+"F0.wireOp",EDGE,"E7.53.0.7"),sQuery(id+"F0.wireOp",EDGE,"E7.53.0.8"),sQuery(id+"F0.wireOp",EDGE,"E7.53.0.9"),sQuery(id+"F0.wireOp",EDGE,"E7.53.0.10"),sQuery(id+"F0.wireOp",EDGE,"E7.53.0.11"),sQuery(id+"F0.wireOp",EDGE,"E7.53.0.12"),sQuery(id+"F0.wireOp",EDGE,"E7.54.0.1"),sQuery(id+"F0.wireOp",EDGE,"E7.54.0.3"),sQuery(id+"F0.wireOp",EDGE,"E7.54.0.4"),sQuery(id+"F0.wireOp",EDGE,"E7.54.0.5"),sQuery(id+"F0.wireOp",EDGE,"E7.54.0.6"),sQuery(id+"F0.wireOp",EDGE,"E7.54.0.7"),sQuery(id+"F0.wireOp",EDGE,"E7.54.0.8"),sQuery(id+"F0.wireOp",EDGE,"E7.54.0.9"),sQuery(id+"F0.wireOp",EDGE,"E7.54.0.10"),sQuery(id+"F0.wireOp",EDGE,"E7.54.0.11"),sQuery(id+"F0.wireOp",EDGE,"E7.54.0.12"),sQuery(id+"F0.wireOp",EDGE,"E7.55.0.1"),sQuery(id+"F0.wireOp",EDGE,"E7.55.0.3"),sQuery(id+"F0.wireOp",EDGE,"E7.55.0.4"),sQuery(id+"F0.wireOp",EDGE,"E7.55.0.5"),sQuery(id+"F0.wireOp",EDGE,"E7.55.0.6"),sQuery(id+"F0.wireOp",EDGE,"E7.55.0.7"),sQuery(id+"F0.wireOp",EDGE,"E7.55.0.8"),sQuery(id+"F0.wireOp",EDGE,"E7.55.0.9"),sQuery(id+"F0.wireOp",EDGE,"E7.55.0.10"),sQuery(id+"F0.wireOp",EDGE,"E7.55.0.11"),sQuery(id+"F0.wireOp",EDGE,"E7.55.0.12"),sQuery(id+"F0.wireOp",EDGE,"E7.56.0.1"),sQuery(id+"F0.wireOp",EDGE,"E7.56.0.3"),sQuery(id+"F0.wireOp",EDGE,"E7.56.0.4"),sQuery(id+"F0.wireOp",EDGE,"E7.56.0.5"),sQuery(id+"F0.wireOp",EDGE,"E7.56.0.6"),sQuery(id+"F0.wireOp",EDGE,"E7.56.0.7"),sQuery(id+"F0.wireOp",EDGE,"E7.56.0.8"),sQuery(id+"F0.wireOp",EDGE,"E7.56.0.9"),sQuery(id+"F0.wireOp",EDGE,"E7.56.0.10"),sQuery(id+"F0.wireOp",EDGE,"E7.56.0.11"),sQuery(id+"F0.wireOp",EDGE,"E7.56.0.12"),sQuery(id+"F0.wireOp",EDGE,"E7.57.0.1"),sQuery(id+"F0.wireOp",EDGE,"E7.57.0.3"),sQuery(id+"F0.wireOp",EDGE,"E7.57.0.4"),sQuery(id+"F0.wireOp",EDGE,"E7.57.0.5"),sQuery(id+"F0.wireOp",EDGE,"E7.57.0.6"),sQuery(id+"F0.wireOp",EDGE,"E7.57.0.7"),sQuery(id+"F0.wireOp",EDGE,"E7.57.0.8"),sQuery(id+"F0.wireOp",EDGE,"E7.57.0.9"),sQuery(id+"F0.wireOp",EDGE,"E7.57.0.10"),sQuery(id+"F0.wireOp",EDGE,"E7.57.0.11"),sQuery(id+"F0.wireOp",EDGE,"E7.57.0.12"),sQuery(id+"F0.wireOp",EDGE,"E7.58.0.1"),sQuery(id+"F0.wireOp",EDGE,"E7.58.0.3"),sQuery(id+"F0.wireOp",EDGE,"E7.58.0.4"),sQuery(id+"F0.wireOp",EDGE,"E7.58.0.5"),sQuery(id+"F0.wireOp",EDGE,"E7.58.0.6"),sQuery(id+"F0.wireOp",EDGE,"E7.58.0.7"),sQuery(id+"F0.wireOp",EDGE,"E7.58.0.8"),sQuery(id+"F0.wireOp",EDGE,"E7.58.0.9"),sQuery(id+"F0.wireOp",EDGE,"E7.58.0.10"),sQuery(id+"F0.wireOp",EDGE,"E7.58.0.11"),sQuery(id+"F0.wireOp",EDGE,"E7.58.0.12"),sQuery(id+"F0.wireOp",EDGE,"E7.59.0.1"),sQuery(id+"F0.wireOp",EDGE,"E7.59.0.3"),sQuery(id+"F0.wireOp",EDGE,"E7.59.0.4"),sQuery(id+"F0.wireOp",EDGE,"E7.59.0.5"),sQuery(id+"F0.wireOp",EDGE,"E7.59.0.6"),sQuery(id+"F0.wireOp",EDGE,"E7.59.0.7"),sQuery(id+"F0.wireOp",EDGE,"E7.59.0.8"),sQuery(id+"F0.wireOp",EDGE,"E7.59.0.9"),sQuery(id+"F0.wireOp",EDGE,"E7.59.0.10"),sQuery(id+"F0.wireOp",EDGE,"E7.59.0.11"),sQuery(id+"F0.wireOp",EDGE,"E7.59.0.12"),sQuery(id+"F0.wireOp",EDGE,"E8.bottom"),sQuery(id+"F0.wireOp",EDGE,"E9.bottom")])],"isStart":true});
            var sketch = newSketch(context, id + "F4", { "sketchPlane" : qUnion([Q0])});
            skLineSegment(sketch, "E20.bottom", {"start": v(-5939.39, 271.76) * mm, "end": v(-5759.39, 271.76) * mm});
            skLineSegment(sketch, "E20.top", {"start": v(-5939.39, 205.85) * mm, "end": v(-5759.39, 205.85) * mm});
            skLineSegment(sketch, "E20.left", {"start": v(-5939.39, 271.76) * mm, "end": v(-5939.39, 205.85) * mm});
            skLineSegment(sketch, "E20.right", {"start": v(-5759.39, 271.76) * mm, "end": v(-5759.39, 205.85) * mm});
            skLineSegment(sketch, "E21.bottom", {"start": v(-5929.39, 261.76) * mm, "end": v(-5769.39, 261.76) * mm});
            skLineSegment(sketch, "E21.top", {"start": v(-5929.39, 215.85) * mm, "end": v(-5769.39, 215.85) * mm});
            skLineSegment(sketch, "E21.left", {"start": v(-5929.39, 261.76) * mm, "end": v(-5929.39, 215.85) * mm});
            skLineSegment(sketch, "E21.right", {"start": v(-5769.39, 261.76) * mm, "end": v(-5769.39, 215.85) * mm});
            skLineSegment(sketch, "E22.1.0.0", {"start": v(-3989.39, 261.76) * mm, "end": v(-3829.39, 261.76) * mm});
            skLineSegment(sketch, "E22.1.0.1", {"start": v(-3989.39, 215.85) * mm, "end": v(-3829.39, 215.85) * mm});
            skLineSegment(sketch, "E22.1.0.2", {"start": v(-3999.39, 205.85) * mm, "end": v(-3819.39, 205.85) * mm});
            skLineSegment(sketch, "E22.1.0.3", {"start": v(-3829.39, 261.76) * mm, "end": v(-3829.39, 215.85) * mm});
            skLineSegment(sketch, "E22.1.0.4", {"start": v(-3999.39, 271.76) * mm, "end": v(-3999.39, 205.85) * mm});
            skLineSegment(sketch, "E22.1.0.5", {"start": v(-3989.39, 261.76) * mm, "end": v(-3989.39, 215.85) * mm});
            skLineSegment(sketch, "E22.1.0.6", {"start": v(-3999.39, 271.76) * mm, "end": v(-3819.39, 271.76) * mm});
            skLineSegment(sketch, "E22.1.0.7", {"start": v(-3819.39, 271.76) * mm, "end": v(-3819.39, 205.85) * mm});
            skLineSegment(sketch, "E22.2.0.0", {"start": v(-2049.39, 261.76) * mm, "end": v(-1889.39, 261.76) * mm});
            skLineSegment(sketch, "E22.2.0.1", {"start": v(-2049.39, 215.85) * mm, "end": v(-1889.39, 215.85) * mm});
            skLineSegment(sketch, "E22.2.0.2", {"start": v(-2059.39, 205.85) * mm, "end": v(-1879.39, 205.85) * mm});
            skLineSegment(sketch, "E22.2.0.3", {"start": v(-1889.39, 261.76) * mm, "end": v(-1889.39, 215.85) * mm});
            skLineSegment(sketch, "E22.2.0.4", {"start": v(-2059.39, 271.76) * mm, "end": v(-2059.39, 205.85) * mm});
            skLineSegment(sketch, "E22.2.0.5", {"start": v(-2049.39, 261.76) * mm, "end": v(-2049.39, 215.85) * mm});
            skLineSegment(sketch, "E22.2.0.6", {"start": v(-2059.39, 271.76) * mm, "end": v(-1879.39, 271.76) * mm});
            skLineSegment(sketch, "E22.2.0.7", {"start": v(-1879.39, 271.76) * mm, "end": v(-1879.39, 205.85) * mm});
            skLineSegment(sketch, "E22.3.0.0", {"start": v(-109.39, 261.76) * mm, "end": v(50.61, 261.76) * mm});
            skLineSegment(sketch, "E22.3.0.1", {"start": v(-109.39, 215.85) * mm, "end": v(50.61, 215.85) * mm});
            skLineSegment(sketch, "E22.3.0.2", {"start": v(-119.39, 205.85) * mm, "end": v(60.61, 205.85) * mm});
            skLineSegment(sketch, "E22.3.0.3", {"start": v(50.61, 261.76) * mm, "end": v(50.61, 215.85) * mm});
            skLineSegment(sketch, "E22.3.0.4", {"start": v(-119.39, 271.76) * mm, "end": v(-119.39, 205.85) * mm});
            skLineSegment(sketch, "E22.3.0.5", {"start": v(-109.39, 261.76) * mm, "end": v(-109.39, 215.85) * mm});
            skLineSegment(sketch, "E22.3.0.6", {"start": v(-119.39, 271.76) * mm, "end": v(60.61, 271.76) * mm});
            skLineSegment(sketch, "E22.3.0.7", {"start": v(60.61, 271.76) * mm, "end": v(60.61, 205.85) * mm});
            skLineSegment(sketch, "E22.direction1", {"start": v(-5939.39, 205.85) * mm, "end": v(-3999.39, 205.85) * mm, "construction": true});
            skSolve(sketch);
        }
        {
            var Q0;
            Q0 = qSketchRegion(id + "F4", true);
            extrude(context, id + "F5", {"entities" : qUnion([Q0]), "operationType" : NewBodyOperationType.ADD, "oppositeDirection" : true, "depth" : 2500 * mm});
        }
        {
            var Q0;
            Q0=makeQuery(id+"F5.opExtrude","SWEPT_FACE",FACE,{"disambiguationData":[OSD([sQuery(id+"F4.wireOp",EDGE,"E20.bottom")])]});
            var sketch = newSketch(context, id + "F6", { "sketchPlane" : qUnion([Q0])});
            skLineSegment(sketch, "E23.bottom", {"start": v(-53.88, -8.44) * mm, "end": v(113.2, -8.44) * mm});
            skLineSegment(sketch, "E23.top", {"start": v(-53.88, -98.79) * mm, "end": v(113.2, -98.79) * mm});
            skLineSegment(sketch, "E23.left", {"start": v(-53.88, -8.44) * mm, "end": v(-53.88, -98.79) * mm});
            skLineSegment(sketch, "E23.right", {"start": v(113.2, -8.44) * mm, "end": v(113.2, -98.79) * mm});
            skLineSegment(sketch, "E24.bottom", {"start": v(1887.38, -12.4) * mm, "end": v(2054.46, -12.4) * mm});
            skLineSegment(sketch, "E24.top", {"start": v(1887.38, -102.76) * mm, "end": v(2054.46, -102.76) * mm});
            skLineSegment(sketch, "E24.left", {"start": v(1887.38, -12.4) * mm, "end": v(1887.38, -102.76) * mm});
            skLineSegment(sketch, "E24.right", {"start": v(2054.46, -12.4) * mm, "end": v(2054.46, -102.76) * mm});
            skLineSegment(sketch, "E25.bottom", {"start": v(3825, -11.62) * mm, "end": v(3992.1, -11.62) * mm});
            skLineSegment(sketch, "E25.top", {"start": v(3825, -101.97) * mm, "end": v(3992.1, -101.97) * mm});
            skLineSegment(sketch, "E25.left", {"start": v(3825, -11.62) * mm, "end": v(3825, -101.97) * mm});
            skLineSegment(sketch, "E25.right", {"start": v(3992.1, -11.62) * mm, "end": v(3992.1, -101.97) * mm});
            skLineSegment(sketch, "E26.bottom", {"start": v(5768.07, -12.66) * mm, "end": v(5935.15, -12.66) * mm});
            skLineSegment(sketch, "E26.top", {"start": v(5768.07, -103) * mm, "end": v(5935.15, -103) * mm});
            skLineSegment(sketch, "E26.left", {"start": v(5768.07, -12.66) * mm, "end": v(5768.07, -103) * mm});
            skLineSegment(sketch, "E26.right", {"start": v(5935.15, -12.66) * mm, "end": v(5935.15, -103) * mm});
            skLineSegment(sketch, "E27.bottom", {"start": v(5768.07, -2403.24) * mm, "end": v(5935.15, -2403.24) * mm});
            skLineSegment(sketch, "E27.top", {"start": v(5768.07, -2493.59) * mm, "end": v(5935.15, -2493.59) * mm});
            skLineSegment(sketch, "E27.left", {"start": v(5768.07, -2403.24) * mm, "end": v(5768.07, -2493.59) * mm});
            skLineSegment(sketch, "E27.right", {"start": v(5935.15, -2403.24) * mm, "end": v(5935.15, -2493.59) * mm});
            skLineSegment(sketch, "E28.bottom", {"start": v(3825, -2394.91) * mm, "end": v(3992.1, -2394.91) * mm});
            skLineSegment(sketch, "E28.top", {"start": v(3825, -2485.26) * mm, "end": v(3992.1, -2485.26) * mm});
            skLineSegment(sketch, "E28.left", {"start": v(3825, -2394.91) * mm, "end": v(3825, -2485.26) * mm});
            skLineSegment(sketch, "E28.right", {"start": v(3992.1, -2394.91) * mm, "end": v(3992.1, -2485.26) * mm});
            skLineSegment(sketch, "E29.bottom", {"start": v(1886.11, -2394.91) * mm, "end": v(2053.2, -2394.91) * mm});
            skLineSegment(sketch, "E29.top", {"start": v(1886.11, -2485.26) * mm, "end": v(2053.2, -2485.26) * mm});
            skLineSegment(sketch, "E29.left", {"start": v(1886.11, -2394.91) * mm, "end": v(1886.11, -2485.26) * mm});
            skLineSegment(sketch, "E29.right", {"start": v(2053.2, -2394.91) * mm, "end": v(2053.2, -2485.26) * mm});
            skLineSegment(sketch, "E30.bottom", {"start": v(-54.87, -2398.03) * mm, "end": v(112.22, -2398.03) * mm});
            skLineSegment(sketch, "E30.top", {"start": v(-54.87, -2488.38) * mm, "end": v(112.22, -2488.38) * mm});
            skLineSegment(sketch, "E30.left", {"start": v(-54.87, -2398.03) * mm, "end": v(-54.87, -2488.38) * mm});
            skLineSegment(sketch, "E30.right", {"start": v(112.22, -2398.03) * mm, "end": v(112.22, -2488.38) * mm});
            skSolve(sketch);
        }
        {
            var Q0;
            Q0 = qConstructionFilter(qBodyType(qCreatedBy(id + "F6" ,EDGE), BodyType.WIRE), ConstructionObject.NO);
            extrude(context, id + "F7", {"bodyType" : ToolBodyType.SURFACE, "surfaceEntities" : qUnion([Q0]), "depth" : 1 * mm});
        }
    });
